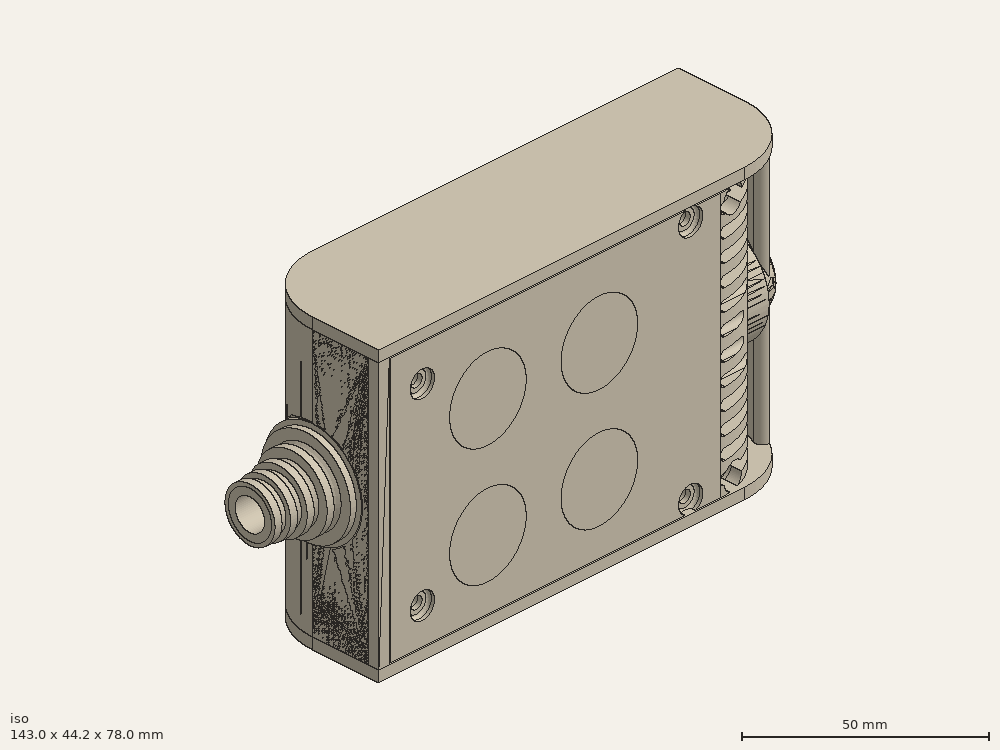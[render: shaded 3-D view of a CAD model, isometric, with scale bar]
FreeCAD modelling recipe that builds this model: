
FCSTD DOCUMENT  (FreeCAD 0.19R0.19.2)
Label: enclosure_135
License: All rights reserved
LicenseURL: http://en.wikipedia.org/wiki/All_rights_reserved
objects: Part::Feature×90, Part::Revolution×90, Part::MultiFuse×66, Sketcher::SketchObject×48, Part::Extrusion×36, Part::Cut×31, Part::Fillet×27, Part::Cylinder×24, Part::Box×17, App::MeasureDistance×4
note: 429 computed .brp shape members not serialized (recipe doc carries the construction recipe); baked Part::Feature solids carry a one-line shape summary decoded from their .brp

FEATURE [Sketcher::SketchObject] Sketch  label="topSketch"
  FullyConstrained = true
  sketch-geometry (20):
    g0: LineSegment StartX=5.21097e-06 StartY=3 StartZ=0 EndX=5.21097e-06 EndY=19 EndZ=0
    g1: ArcOfCircle CenterX=19 CenterY=19 CenterZ=0 NormalX=0 NormalY=0 NormalZ=1 AngleXU=0 Radius=19 StartAngle=1.5708 EndAngle=3.14159
    g2: ArcOfCircle CenterX=19 CenterY=19 CenterZ=0 NormalX=0 NormalY=0 NormalZ=1 AngleXU=0 Radius=16 StartAngle=1.5708 EndAngle=3.14159
    g3: LineSegment StartX=114 StartY=35 StartZ=0 EndX=19 EndY=35 EndZ=0
    g4: LineSegment StartX=5.21097e-06 StartY=3 StartZ=0 EndX=5.21097e-06 EndY=0 EndZ=0
    g5: LineSegment StartX=3 StartY=0 StartZ=0 EndX=5.21097e-06 EndY=0 EndZ=0
    g6: LineSegment StartX=3 StartY=19 StartZ=0 EndX=3 EndY=0 EndZ=0
    g7: LineSegment StartX=19 StartY=38 StartZ=0 EndX=124 EndY=38 EndZ=0
    g8: Circle CenterX=119 CenterY=35 CenterZ=0 NormalX=0 NormalY=0 NormalZ=1 AngleXU=0 Radius=1
    g9: Circle CenterX=121 CenterY=35 CenterZ=0 NormalX=0 NormalY=0 NormalZ=1 AngleXU=0 Radius=1
    g10: Circle CenterX=121 CenterY=33 CenterZ=0 NormalX=0 NormalY=0 NormalZ=1 AngleXU=0 Radius=1
    g11: BSplineCurve PolesCount=3 KnotsCount=2 Degree=2 IsPeriodic=0
    g12: GeomPoint X=119 Y=35 Z=0
    g13: GeomPoint X=121 Y=33 Z=0
    g14: LineSegment StartX=119 StartY=35 StartZ=0 EndX=114 EndY=35 EndZ=0
    g15: ArcOfCircle CenterX=105 CenterY=19 CenterZ=0 NormalX=0 NormalY=0 NormalZ=1 AngleXU=0 Radius=19 StartAngle=5.7297 EndAngle=6.28319
    g16: ArcOfCircle CenterX=105 CenterY=19 CenterZ=0 NormalX=0 NormalY=0 NormalZ=1 AngleXU=0 Radius=16 StartAngle=5.60905 EndAngle=6.28319
    g17: LineSegment StartX=121 StartY=33 StartZ=0 EndX=121 EndY=19 EndZ=0
    g18: LineSegment StartX=124 StartY=38 StartZ=0 EndX=124 EndY=19 EndZ=0
    g19: LineSegment StartX=117.5 StartY=9.01251 StartZ=0 EndX=121.163 EndY=9.0125 EndZ=0
  constraints (46):
    c: Vertical(g0)
    c: Block(g0)
    c: Coincident(g1,g0)
    c: Block(g1)
    c: Coincident(g2,g1)
    c: Block(g2)
    c: Coincident(g3,g2)
    c: Horizontal(g3)
    c: Tangent(g3,g2)
    c: Coincident(g4,g0)
    c: Distance(g4) = 3
    c: Vertical(g4)
    c: Coincident(g5,g4)
    c: Horizontal(g5)
    c: Coincident(g6,g2)
    c: Coincident(g6,g5)
    c: Vertical(g6)
    c: Horizontal(g7)
    c: Distance(g7) = 105
    c: Coincident(g7,g1)
    c: Block(g3)
    c: Weight(g8) = 1
    c: Equal(g8,g9)
    c: Equal(g8,g10)
    c: InternalAlignment(g8,g11)
    c: InternalAlignment(g9,g11)
    c: InternalAlignment(g10,g11)
    c: InternalAlignment(g12,g11)
    c: InternalAlignment(g13,g11)
    c: Block(g11)
    c: Coincident(g14,g11)
    c: Coincident(g14,g3)
    c: Horizontal(g14)
    c: Block(g15)
    c: Coincident(g16,g15)
    c: Block(g16)
    c: Coincident(g17,g11)
    c: Coincident(g17,g16)
    c: Vertical(g17)
    c: Distance(g17) = 14
    c: Coincident(g18,g7)
    c: Coincident(g18,g15)
    c: Vertical(g18)
    c: Distance(g18) = 19
    c: Coincident(g19,g16)
    c: Coincident(g19,g15)
FEATURE [Sketcher::SketchObject] Sketch001  label="bottomSketch"
  FullyConstrained = true
  sketch-geometry (32):
    g0: LineSegment StartX=3.3 StartY=-6.03275e-07 StartZ=0 EndX=98 EndY=-6.03275e-07 EndZ=0
    g1: ArcOfCircle CenterX=98 CenterY=19 CenterZ=0 NormalX=0 NormalY=0 NormalZ=1 AngleXU=0 Radius=19 StartAngle=4.71239 EndAngle=5.71103
    g2: LineSegment StartX=6.3 StartY=8 StartZ=0 EndX=3.3 EndY=8 EndZ=0
    g3: LineSegment StartX=3.3 StartY=8 StartZ=0 EndX=3.3 EndY=-6.03275e-07 EndZ=0
    g4: ArcOfCircle CenterX=8.3 CenterY=5 CenterZ=0 NormalX=0 NormalY=0 NormalZ=1 AngleXU=0 Radius=2 StartAngle=3.14159 EndAngle=4.71239
    g5: LineSegment StartX=6.3 StartY=8 StartZ=0 EndX=6.3 EndY=5 EndZ=0
    g6: ArcOfCircle CenterX=98 CenterY=19 CenterZ=0 NormalX=0 NormalY=0 NormalZ=1 AngleXU=0 Radius=12.7 StartAngle=4.71239 EndAngle=6.28319
    g7: LineSegment StartX=94.7 StartY=3 StartZ=0 EndX=8.3 EndY=3 EndZ=0
    g8-g12: Circle x5 (B-spline internal-alignment scaffolding for g13; pole/knot coordinates omitted)
    g13: BSplineCurve PolesCount=5 KnotsCount=3 Degree=3 IsPeriodic=0
    g14: GeomPoint X=98 Y=6.3 Z=0
    g15: GeomPoint X=96.3938 Y=4.71946 Z=0
    g16: GeomPoint X=94.7 Y=3 Z=0
    g17-g23: Circle x7 (B-spline internal-alignment scaffolding for g24; pole/knot coordinates omitted)
    g24: BSplineCurve PolesCount=7 KnotsCount=5 Degree=3 IsPeriodic=0
    g25-g29: GeomPoint x5 (B-spline internal-alignment scaffolding for g24; pole/knot coordinates omitted)
    g30: ArcOfCircle CenterX=98 CenterY=19 CenterZ=0 NormalX=0 NormalY=0 NormalZ=1 AngleXU=0 Radius=15.7 StartAngle=5.81226 EndAngle=6.28319
    g31: LineSegment StartX=110.7 StartY=19 StartZ=0 EndX=113.7 EndY=19 EndZ=0
  constraints (41):
    c: Horizontal(g0)
    c: Coincident(g1,g0)
    c: Block(g1)
    c: Horizontal(g2)
    c: Distance(g2) = 3
    c: Coincident(g3,g2)
    c: Vertical(g3)
    c: Coincident(g3,g0)
    c: Block(g4)
    c: Block(g2)
    c: Coincident(g5,g2)
    c: Coincident(g5,g4)
    c: Vertical(g5)
    c: Coincident(g6,g1)
    c: Block(g6)
    c: Coincident(g7,g4)
    c: Horizontal(g7)
    c: Block(g0)
    c: Block(g7)
    c: Block(g3)
    c: Coincident(g13,g6)
    c: Weight(g8) = 1
    c: Equal(g8, g9-g12) x4
    c: Coincident(g13,g7)
    c: InternalAlignment(g8-g12 -> g13) x5
    c: InternalAlignment(g14,g13)
    c: InternalAlignment(g15,g13)
    c: InternalAlignment(g16,g13)
    c: Block(g13)
    c: Weight(g17) = 1
    c: Equal(g17, g18-g23) x6
    c: Coincident(g24,g1)
    c: InternalAlignment(g17-g23 -> g24) x7
    c: InternalAlignment(g25-g29 -> g24) x5
    c: Block(g24)
    c: Coincident(g30,g24)
    c: Coincident(g31,g6)
    c: Coincident(g31,g30)
    c: Horizontal(g31)
    c: Block(g31)
    c: Block(g30)
FEATURE [Part::Extrusion] Extrude  label="top"
  Base = -> Sketch
  Dir = (0,0,1)
  DirMode = 2
  FaceMakerClass = Part::FaceMakerBullseye
  LengthFwd = 72
  LengthRev = 0
  Solid = true
  Symmetric = false
FEATURE [Part::Extrusion] Extrude001  label="bottom"
  Base = -> Sketch001
  Dir = (0,0,1)
  DirMode = 2
  FaceMakerClass = Part::FaceMakerBullseye
  LengthFwd = 71.4
  LengthRev = 0
  Placement = pos=(0,0,0.3) rot=(0,0,1;0rad)
  Solid = true
  Symmetric = false
FEATURE [Sketcher::SketchObject] Sketch002  label="topSketch001"
  FullyConstrained = true
  sketch-geometry (6):
    g0: ArcOfCircle CenterX=19 CenterY=19 CenterZ=0 NormalX=0 NormalY=0 NormalZ=1 AngleXU=0 Radius=19 StartAngle=1.5708 EndAngle=3.14159
    g1: LineSegment StartX=5.22862e-06 StartY=19 StartZ=0 EndX=5.22862e-06 EndY=1.19904e-11 EndZ=0
    g2: LineSegment StartX=19 StartY=38 StartZ=0 EndX=124 EndY=38 EndZ=0
    g3: LineSegment StartX=5.22862e-06 StartY=1.19904e-11 StartZ=0 EndX=105 EndY=1.19904e-11 EndZ=0
    g4: ArcOfCircle CenterX=105 CenterY=19 CenterZ=0 NormalX=0 NormalY=0 NormalZ=1 AngleXU=0 Radius=19 StartAngle=4.71239 EndAngle=6.28319
    g5: LineSegment StartX=124 StartY=38 StartZ=0 EndX=124 EndY=19 EndZ=0
  constraints (16):
    c: Block(g0)
    c: Coincident(g1,g0)
    c: Vertical(g1)
    c: Horizontal(g2)
    c: Distance(g2) = 105
    c: Coincident(g2,g0)
    c: Distance(g1) = 19
    c: Coincident(g3,g1)
    c: Horizontal(g3)
    c: Distance(g3) = 105
    c: Block(g4)
    c: Coincident(g4,g3)
    c: Coincident(g5,g2)
    c: Coincident(g5,g4)
    c: Vertical(g5)
    c: Distance(g5) = 19
FEATURE [Part::Extrusion] Extrude002  label="sideA"
  Base = -> Sketch002
  Dir = (0,0,1)
  DirMode = 2
  FaceMakerClass = Part::FaceMakerBullseye
  LengthFwd = 3
  LengthRev = 0
  Placement = pos=(0,0,-3) rot=(0,0,1;0rad)
  Solid = true
  Symmetric = false
FEATURE [Sketcher::SketchObject] Sketch003  label="topSketch002"
  FullyConstrained = true
  sketch-geometry (6):
    g0: LineSegment StartX=19 StartY=38 StartZ=0 EndX=117 EndY=38 EndZ=0
    g1: ArcOfCircle CenterX=19 CenterY=19 CenterZ=0 NormalX=0 NormalY=0 NormalZ=1 AngleXU=0 Radius=19 StartAngle=1.5708 EndAngle=3.14159
    g2: LineSegment StartX=117 StartY=38 StartZ=0 EndX=117 EndY=19 EndZ=0
    g3: LineSegment StartX=98 StartY=1.0161e-12 StartZ=0 EndX=5.22862e-06 EndY=1.0161e-12 EndZ=0
    g4: LineSegment StartX=5.22862e-06 StartY=19 StartZ=0 EndX=5.22862e-06 EndY=1.0161e-12 EndZ=0
    g5: ArcOfCircle CenterX=98 CenterY=19 CenterZ=0 NormalX=0 NormalY=0 NormalZ=1 AngleXU=0 Radius=19 StartAngle=4.71239 EndAngle=6.28319
  constraints (16):
    c: Horizontal(g0)
    c: Distance(g0) = 98
    c: Coincident(g1,g0)
    c: Block(g1)
    c: Coincident(g2,g0)
    c: Vertical(g2)
    c: Distance(g2) = 19
    c: Horizontal(g3)
    c: Coincident(g4,g1)
    c: Vertical(g4)
    c: Coincident(g3,g4)
    c: Block(g3)
    c: Coincident(g5,g2)
    c: Coincident(g5,g3)
    c: Block(g0)
    c: Block(g5)
FEATURE [Sketcher::SketchObject] Sketch004
  FullyConstrained = true
  MapMode = 3
  Placement = pos=(0,0,0) rot=(1,0,0;1.5708rad)
  Support = -> [Extrude]
  sketch-geometry (8):
    g0: Circle CenterX=80.351 CenterY=-67.6202 CenterZ=0 NormalX=0 NormalY=0 NormalZ=1 AngleXU=0 Radius=2
    g1: Circle CenterX=80.351 CenterY=-67.6202 CenterZ=0 NormalX=0 NormalY=0 NormalZ=1 AngleXU=0 Radius=3
    g2: Circle CenterX=80.351 CenterY=-4.92017 CenterZ=0 NormalX=0 NormalY=0 NormalZ=1 AngleXU=0 Radius=2
    g3: Circle CenterX=80.351 CenterY=-4.92017 CenterZ=0 NormalX=0 NormalY=0 NormalZ=1 AngleXU=0 Radius=3
    g4: Circle CenterX=23.851 CenterY=-4.92017 CenterZ=0 NormalX=0 NormalY=0 NormalZ=1 AngleXU=0 Radius=2
    g5: Circle CenterX=23.851 CenterY=-4.92017 CenterZ=0 NormalX=0 NormalY=0 NormalZ=1 AngleXU=0 Radius=3
    g6: Circle CenterX=23.851 CenterY=-67.6202 CenterZ=0 NormalX=0 NormalY=0 NormalZ=1 AngleXU=0 Radius=2
    g7: Circle CenterX=23.851 CenterY=-67.6202 CenterZ=0 NormalX=0 NormalY=0 NormalZ=1 AngleXU=0 Radius=3
  constraints (8):
    c: Block(g3)
    c: Block(g2)
    c: Block(g1)
    c: Block(g0)
    c: Block(g6)
    c: Block(g7)
    c: Block(g4)
    c: Block(g5)
FEATURE [Part::Extrusion] Extrude004
  Base = -> Sketch004
  Dir = (0,-1,2e-16)
  DirMode = 2
  FaceMakerClass = Part::FaceMakerBullseye
  LengthFwd = 6
  LengthRev = 0
  Placement = pos=(0,9,0) rot=(0,0,1;0rad)
  Solid = true
  Symmetric = false
FEATURE [Sketcher::SketchObject] Sketch005
  FullyConstrained = true
  MapMode = 3
  Placement = pos=(0,0,0) rot=(1,0,0;1.5708rad)
  Support = -> [Extrude]
  sketch-geometry (8):
    g0: Circle CenterX=80.351 CenterY=-67.6202 CenterZ=0 NormalX=0 NormalY=0 NormalZ=1 AngleXU=0 Radius=3
    g1: Circle CenterX=80.351 CenterY=-4.92017 CenterZ=0 NormalX=0 NormalY=0 NormalZ=1 AngleXU=0 Radius=3
    g2: Circle CenterX=23.851 CenterY=-4.92017 CenterZ=0 NormalX=0 NormalY=0 NormalZ=1 AngleXU=0 Radius=3
    g3: Circle CenterX=23.851 CenterY=-67.6202 CenterZ=0 NormalX=0 NormalY=0 NormalZ=1 AngleXU=0 Radius=3
    g4: Circle CenterX=23.851 CenterY=-67.6202 CenterZ=0 NormalX=0 NormalY=0 NormalZ=1 AngleXU=0 Radius=5
    g5: Circle CenterX=80.351 CenterY=-67.6202 CenterZ=0 NormalX=0 NormalY=0 NormalZ=1 AngleXU=0 Radius=5
    g6: Circle CenterX=23.851 CenterY=-4.92017 CenterZ=0 NormalX=0 NormalY=0 NormalZ=1 AngleXU=0 Radius=5
    g7: Circle CenterX=80.351 CenterY=-4.92017 CenterZ=0 NormalX=0 NormalY=0 NormalZ=1 AngleXU=0 Radius=5
  constraints (8):
    c: Block(g1)
    c: Block(g0)
    c: Block(g3)
    c: Block(g2)
    c: Block(g5)
    c: Block(g4)
    c: Block(g6)
    c: Block(g7)
FEATURE [Part::Extrusion] Extrude005
  Base = -> Sketch005
  Dir = (0,-1,2e-16)
  DirMode = 2
  FaceMakerClass = Part::FaceMakerBullseye
  LengthFwd = 2
  LengthRev = 0
  Solid = true
  Symmetric = false
FEATURE [Sketcher::SketchObject] Sketch006
  FullyConstrained = true
  MapMode = 3
  Placement = pos=(0,0,0) rot=(1,0,0;1.5708rad)
  sketch-geometry (8):
    g0: Circle CenterX=80.351 CenterY=-67.6202 CenterZ=0 NormalX=0 NormalY=0 NormalZ=1 AngleXU=0 Radius=3
    g1: Circle CenterX=80.351 CenterY=-4.92017 CenterZ=0 NormalX=0 NormalY=0 NormalZ=1 AngleXU=0 Radius=3
    g2: Circle CenterX=23.851 CenterY=-4.92017 CenterZ=0 NormalX=0 NormalY=0 NormalZ=1 AngleXU=0 Radius=3
    g3: Circle CenterX=23.851 CenterY=-67.6202 CenterZ=0 NormalX=0 NormalY=0 NormalZ=1 AngleXU=0 Radius=3
    g4: Circle CenterX=23.851 CenterY=-67.6202 CenterZ=0 NormalX=0 NormalY=0 NormalZ=1 AngleXU=0 Radius=5
    g5: Circle CenterX=80.351 CenterY=-67.6202 CenterZ=0 NormalX=0 NormalY=0 NormalZ=1 AngleXU=0 Radius=5
    g6: Circle CenterX=23.851 CenterY=-4.92017 CenterZ=0 NormalX=0 NormalY=0 NormalZ=1 AngleXU=0 Radius=5
    g7: Circle CenterX=80.351 CenterY=-4.92017 CenterZ=0 NormalX=0 NormalY=0 NormalZ=1 AngleXU=0 Radius=5
  constraints (8):
    c: Block(g1)
    c: Block(g0)
    c: Block(g3)
    c: Block(g2)
    c: Block(g5)
    c: Block(g4)
    c: Block(g6)
    c: Block(g7)
FEATURE [Part::Extrusion] Extrude007
  Base = -> Sketch006
  Dir = (0,-1,2e-16)
  DirMode = 2
  FaceMakerClass = Part::FaceMakerBullseye
  LengthFwd = 2
  LengthRev = 0
  Solid = true
  Symmetric = false
FEATURE [Part::Fillet] Fillet
  Base = -> Extrude007
  Edges = 4 edges r=1.99: [Edge6,Edge12,Edge18,Edge24]
FEATURE [Part::Cut] Cut
  Base = -> Extrude005
  Placement = pos=(0,5,0) rot=(0,0,1;0rad)
  Tool = -> Fillet
FEATURE [Part::MultiFuse] Fusion  label="pCBScrews"
  Placement = pos=(-2.5,0,72.3) rot=(0,0,1;0rad)
  Shapes = -> [Extrude004,Cut]
FEATURE [App::MeasureDistance] Distance  label="Distance: 0.69 mm"
  Distance = 0.685967
  P1 = (24.0138,2.9647,0.3)
  P2 = (23.8901,3,-0.373787)
FEATURE [App::MeasureDistance] Distance001  label="Distance: 0.53 mm"
  Distance = 0.533607
  P1 = (80.2939,3,72.2334)
  P2 = (80.281,2.99661,71.7)
FEATURE [Part::Fillet] Fillet001
  Base = -> Extrude001
  Edges = 1 edges r=2.4: [Edge17]
FEATURE [Part::Fillet] Fillet002  label="bottom001"
  Base = -> Fillet001
  Edges = 1 edges r=2.4: [Edge36]
FEATURE [Part::Fillet] Fillet003  label="top001"
  Base = -> Extrude
  Edges = 1 edges r=2: [Edge1]
FEATURE [Sketcher::SketchObject] Sketch007
  FullyConstrained = true
  sketch-geometry (16):
    g0: LineSegment StartX=4 StartY=0 StartZ=0 EndX=4 EndY=2.4 EndZ=0
    g1: LineSegment StartX=4 StartY=2.4 StartZ=0 EndX=7 EndY=2.4 EndZ=0
    g2: LineSegment StartX=4 StartY=0 StartZ=0 EndX=5.7 EndY=0 EndZ=0
    g3: LineSegment StartX=5.7 StartY=0 StartZ=0 EndX=5.7 EndY=-5.6 EndZ=0
    g4-g8: Circle x5 (B-spline internal-alignment scaffolding for g9; pole/knot coordinates omitted)
    g9: BSplineCurve PolesCount=5 KnotsCount=3 Degree=3 IsPeriodic=0
    g10: GeomPoint X=7 Y=2.4 Z=0
    g11: GeomPoint X=10.4582 Y=-1.55472 Z=0
    g12: GeomPoint X=14 Y=-5.6 Z=0
    g13: LineSegment StartX=14 StartY=-5.6 StartZ=0 EndX=14 EndY=-14.1 EndZ=0
    g14: LineSegment StartX=14 StartY=-14.1 StartZ=0 EndX=6.5 EndY=-14.1 EndZ=0
    g15: LineSegment StartX=5.7 StartY=-5.6 StartZ=0 EndX=6.5 EndY=-14.1 EndZ=0
  constraints (28):
    c: Distance(g0) = 2.4
    c: Vertical(g0)
    c: Block(g0)
    c: Coincident(g1,g0)
    c: Horizontal(g1)
    c: Distance(g1) = 3
    c: Coincident(g2,g0)
    c: Horizontal(g2)
    c: Distance(g2) = 1.7
    c: Coincident(g3,g2)
    c: Vertical(g3)
    c: Distance(g3) = 5.6
    c: Coincident(g9,g1)
    c: Weight(g4) = 1
    c: Equal(g4, g5-g8) x4
    c: InternalAlignment(g4-g8 -> g9) x5
    c: InternalAlignment(g10,g9)
    c: InternalAlignment(g11,g9)
    c: InternalAlignment(g12,g9)
    c: Block(g9)
    c: Coincident(g13,g9)
    c: Vertical(g13)
    c: Distance(g13) = 8.5
    c: Coincident(g14,g13)
    c: Horizontal(g14)
    c: Distance(g14) = 7.5
    c: Coincident(g15,g3)
    c: Coincident(g15,g14)
FEATURE [Part::Feature] Face
  shape: bbox 10 x 16.5 x 2e-07 mm, 1 faces, 0 solids (baked)
FEATURE [Part::Revolution] Revolve  label="plugHousing"
  Angle = 360
  Axis = (0,1,0)
  Base = (0,0,0)
  FaceMakerClass = Part::FaceMakerBullseye
  Placement = pos=(0,0,36.15) rot=(0,0,1;0rad)
  Solid = false
  Source = -> Face
  Symmetric = false
FEATURE [Part::Feature] Face001
  shape: bbox 10 x 16.5 x 2e-07 mm, 1 faces, 0 solids (baked)
FEATURE [Part::Revolution] Revolve001  label="plugHousing001"
  Angle = 360
  Axis = (0,1,0)
  Base = (0,0,0)
  FaceMakerClass = Part::FaceMakerBullseye
  Placement = pos=(0,0,36.15) rot=(0,0,1;0rad)
  Solid = false
  Source = -> Face001
  Symmetric = false
FEATURE [Part::MultiFuse] Fusion001  label="plugHousing002"
  Placement = pos=(0,0,0) rot=(0,0,1;1.5708rad)
  Shapes = -> [Revolve001,Revolve]
FEATURE [Part::Feature] Face002
  shape: bbox 10 x 16.5 x 2e-07 mm, 1 faces, 0 solids (baked)
FEATURE [Part::Revolution] Revolve003  label="plugHousing005"
  Angle = 360
  Axis = (0,1,0)
  Base = (0,0,0)
  FaceMakerClass = Part::FaceMakerBullseye
  Placement = pos=(0,0,36.15) rot=(0,0,1;0rad)
  Solid = false
  Source = -> Face002
  Symmetric = false
FEATURE [Part::Feature] Face003
  shape: bbox 10 x 16.5 x 2e-07 mm, 1 faces, 0 solids (baked)
FEATURE [Part::Revolution] Revolve002  label="plugHousing003"
  Angle = 360
  Axis = (0,1,0)
  Base = (0,0,0)
  FaceMakerClass = Part::FaceMakerBullseye
  Placement = pos=(0,0,36.15) rot=(0,0,1;0rad)
  Solid = false
  Source = -> Face003
  Symmetric = false
FEATURE [Part::MultiFuse] Fusion002  label="plugHousing004"
  Placement = pos=(0,0,0) rot=(0,0,1;1.5708rad)
  Shapes = -> [Revolve002,Revolve003]
FEATURE [Part::MultiFuse] Fusion003  label="plugHousing006"
  Placement = pos=(0,19,0) rot=(0,0,1;3.14159rad)
  Shapes = -> [Fusion002,Fusion001]
FEATURE [Part::Feature] Face004
  shape: bbox 10 x 16.5 x 2e-07 mm, 1 faces, 0 solids (baked)
FEATURE [Part::Revolution] Revolve006  label="plugHousing010"
  Angle = 360
  Axis = (0,1,0)
  Base = (0,0,0)
  FaceMakerClass = Part::FaceMakerBullseye
  Placement = pos=(0,0,36.15) rot=(0,0,1;0rad)
  Solid = false
  Source = -> Face004
  Symmetric = false
FEATURE [Part::Feature] Face005
  shape: bbox 10 x 16.5 x 2e-07 mm, 1 faces, 0 solids (baked)
FEATURE [Part::Revolution] Revolve007  label="plugHousing011"
  Angle = 360
  Axis = (0,1,0)
  Base = (0,0,0)
  FaceMakerClass = Part::FaceMakerBullseye
  Placement = pos=(0,0,36.15) rot=(0,0,1;0rad)
  Solid = false
  Source = -> Face005
  Symmetric = false
FEATURE [Part::Feature] Face006
  shape: bbox 10 x 16.5 x 2e-07 mm, 1 faces, 0 solids (baked)
FEATURE [Part::Revolution] Revolve004  label="plugHousing007"
  Angle = 360
  Axis = (0,1,0)
  Base = (0,0,0)
  FaceMakerClass = Part::FaceMakerBullseye
  Placement = pos=(0,0,36.15) rot=(0,0,1;0rad)
  Solid = false
  Source = -> Face006
  Symmetric = false
FEATURE [Part::MultiFuse] Fusion004  label="plugHousing009"
  Placement = pos=(0,0,0) rot=(0,0,1;1.5708rad)
  Shapes = -> [Revolve004,Revolve007]
FEATURE [Part::Feature] Face007
  shape: bbox 10 x 16.5 x 2e-07 mm, 1 faces, 0 solids (baked)
FEATURE [Part::Revolution] Revolve005  label="plugHousing008"
  Angle = 360
  Axis = (0,1,0)
  Base = (0,0,0)
  FaceMakerClass = Part::FaceMakerBullseye
  Placement = pos=(0,0,36.15) rot=(0,0,1;0rad)
  Solid = false
  Source = -> Face007
  Symmetric = false
FEATURE [Part::MultiFuse] Fusion005  label="plugHousing012"
  Placement = pos=(0,0,0) rot=(0,0,1;1.5708rad)
  Shapes = -> [Revolve006,Revolve005]
FEATURE [Part::MultiFuse] Fusion006  label="plugHousing013"
  Placement = pos=(0,19,0) rot=(0,0,1;3.14159rad)
  Shapes = -> [Fusion005,Fusion004]
FEATURE [Part::MultiFuse] Fusion007  label="plugHousing014"
  Placement = pos=(122.621,0,-0.15) rot=(0,0,1;0rad)
  Shapes = -> [Fusion003,Fusion006]
FEATURE [Part::Cylinder] Cylinder002
  Angle = 360
  AttacherType = Attacher::AttachEngine3D
  Height = 20
  Placement = pos=(0,0,36.15) rot=(0,0,1;0rad)
  Radius = 4
FEATURE [Part::Cylinder] Cylinder003
  Angle = 360
  AttacherType = Attacher::AttachEngine3D
  Height = 10
  Placement = pos=(0,0,36.15) rot=(0,0,1;0rad)
  Radius = 4
FEATURE [Part::MultiFuse] Fusion009  label="removeToCreateHoleForPlugHousing"
  Placement = pos=(70,19,36.15) rot=(0,1,0;1.5708rad)
  Shapes = -> [Cylinder002,Cylinder003]
FEATURE [Part::Cylinder] Cylinder004
  Angle = 360
  AttacherType = Attacher::AttachEngine3D
  Height = 20
  Placement = pos=(0,0,36.15) rot=(0,0,1;0rad)
  Radius = 4
FEATURE [Part::Cylinder] Cylinder005
  Angle = 360
  AttacherType = Attacher::AttachEngine3D
  Height = 10
  Placement = pos=(0,0,36.15) rot=(0,0,1;0rad)
  Radius = 4
FEATURE [Part::MultiFuse] Fusion010  label="removeToCreateHoleForPlugHousing001"
  Placement = pos=(70,19,36.15) rot=(0,1,0;1.5708rad)
  Shapes = -> [Cylinder004,Cylinder005]
FEATURE [Part::Cut] Cut001
  Base = -> Fillet003
  Tool = -> Fusion010
FEATURE [Part::Cut] Cut002  label="Bottom"
  Base = -> Fillet002
  Tool = -> Fusion009
FEATURE [Part::Feature] Face008
  shape: bbox 10 x 16.5 x 2e-07 mm, 1 faces, 0 solids (baked)
FEATURE [Part::Revolution] Revolve011  label="plugHousing021"
  Angle = 360
  Axis = (0,1,0)
  Base = (0,0,0)
  FaceMakerClass = Part::FaceMakerBullseye
  Placement = pos=(0,0,36.15) rot=(0,0,1;0rad)
  Solid = false
  Source = -> Face008
  Symmetric = false
FEATURE [Part::Feature] Face009
  shape: bbox 10 x 16.5 x 2e-07 mm, 1 faces, 0 solids (baked)
FEATURE [Part::Revolution] Revolve012  label="plugHousing022"
  Angle = 360
  Axis = (0,1,0)
  Base = (0,0,0)
  FaceMakerClass = Part::FaceMakerBullseye
  Placement = pos=(0,0,36.15) rot=(0,0,1;0rad)
  Solid = false
  Source = -> Face009
  Symmetric = false
FEATURE [Part::Feature] Face010 .. Face013  x4 (patterned run collapsed; names and placements below)
  shape: bbox 10 x 16.5 x 2e-07 mm, 1 faces, 0 solids (baked)
FEATURE [Part::Revolution] Revolve015  label="plugHousing027"
  Angle = 360
  Axis = (0,1,0)
  Base = (0,0,0)
  FaceMakerClass = Part::FaceMakerBullseye
  Placement = pos=(0,0,36.15) rot=(0,0,1;0rad)
  Solid = false
  Source = -> Face013
  Symmetric = false
FEATURE [Part::Feature] Face014
  shape: bbox 10 x 16.5 x 2e-07 mm, 1 faces, 0 solids (baked)
FEATURE [Part::Feature] Face015
  shape: bbox 10 x 16.5 x 2e-07 mm, 1 faces, 0 solids (baked)
FEATURE [Part::Feature] Face016
  shape: bbox 10 x 16.5 x 2e-07 mm, 1 faces, 0 solids (baked)
FEATURE [Part::Revolution] Revolve019  label="plugHousing033"
  Angle = 360
  Axis = (0,1,0)
  Base = (0,0,0)
  FaceMakerClass = Part::FaceMakerBullseye
  Placement = pos=(0,0,36.15) rot=(0,0,1;0rad)
  Solid = false
  Source = -> Face016
  Symmetric = false
FEATURE [Part::Feature] Face017
  shape: bbox 10 x 16.5 x 2e-07 mm, 1 faces, 0 solids (baked)
FEATURE [Part::Revolution] Revolve020  label="plugHousing034"
  Angle = 360
  Axis = (0,1,0)
  Base = (0,0,0)
  FaceMakerClass = Part::FaceMakerBullseye
  Placement = pos=(0,0,36.15) rot=(0,0,1;0rad)
  Solid = false
  Source = -> Face017
  Symmetric = false
FEATURE [Part::Feature] Face018
  shape: bbox 10 x 16.5 x 2e-07 mm, 1 faces, 0 solids (baked)
FEATURE [Part::Revolution] Revolve016  label="plugHousing030"
  Angle = 360
  Axis = (0,1,0)
  Base = (0,0,0)
  FaceMakerClass = Part::FaceMakerBullseye
  Placement = pos=(0,0,36.15) rot=(0,0,1;0rad)
  Solid = false
  Source = -> Face018
  Symmetric = false
FEATURE [Part::MultiFuse] Fusion020  label="plugHousing038"
  Placement = pos=(0,0,0) rot=(0,0,1;1.5708rad)
  Shapes = -> [Revolve016,Revolve020]
FEATURE [Part::Feature] Face019
  shape: bbox 10 x 16.5 x 2e-07 mm, 1 faces, 0 solids (baked)
FEATURE [Part::Feature] Face020
  shape: bbox 10 x 16.5 x 2e-07 mm, 1 faces, 0 solids (baked)
FEATURE [Part::Revolution] Revolve017  label="plugHousing031"
  Angle = 360
  Axis = (0,1,0)
  Base = (0,0,0)
  FaceMakerClass = Part::FaceMakerBullseye
  Placement = pos=(0,0,36.15) rot=(0,0,1;0rad)
  Solid = false
  Source = -> Face020
  Symmetric = false
FEATURE [Part::MultiFuse] Fusion021  label="plugHousing039"
  Placement = pos=(0,0,0) rot=(0,0,1;1.5708rad)
  Shapes = -> [Revolve019,Revolve017]
FEATURE [Part::MultiFuse] Fusion023  label="plugHousing041"
  Placement = pos=(0,19,0) rot=(0,0,1;3.14159rad)
  Shapes = -> [Fusion021,Fusion020]
FEATURE [Part::Revolution] Revolve022  label="plugHousing043"
  Angle = 360
  Axis = (0,1,0)
  Base = (0,0,0)
  FaceMakerClass = Part::FaceMakerBullseye
  Placement = pos=(0,0,36.15) rot=(0,0,1;0rad)
  Solid = false
  Source = -> Face019
  Symmetric = false
FEATURE [Part::Feature] Face021
  shape: bbox 10 x 16.5 x 2e-07 mm, 1 faces, 0 solids (baked)
FEATURE [Part::Revolution] Revolve023  label="plugHousing044"
  Angle = 360
  Axis = (0,1,0)
  Base = (0,0,0)
  FaceMakerClass = Part::FaceMakerBullseye
  Placement = pos=(0,0,36.15) rot=(0,0,1;0rad)
  Solid = false
  Source = -> Face021
  Symmetric = false
FEATURE [Part::Feature] Face022
  shape: bbox 10 x 16.5 x 2e-07 mm, 1 faces, 0 solids (baked)
FEATURE [Part::Revolution] Revolve018  label="plugHousing032"
  Angle = 360
  Axis = (0,1,0)
  Base = (0,0,0)
  FaceMakerClass = Part::FaceMakerBullseye
  Placement = pos=(0,0,36.15) rot=(0,0,1;0rad)
  Solid = false
  Source = -> Face022
  Symmetric = false
FEATURE [Part::MultiFuse] Fusion022  label="plugHousing040"
  Placement = pos=(0,0,0) rot=(0,0,1;1.5708rad)
  Shapes = -> [Revolve018,Revolve023]
FEATURE [Part::Feature] Face023
  shape: bbox 10 x 16.5 x 2e-07 mm, 1 faces, 0 solids (baked)
FEATURE [Part::Revolution] Revolve021  label="plugHousing035"
  Angle = 360
  Axis = (0,1,0)
  Base = (0,0,0)
  FaceMakerClass = Part::FaceMakerBullseye
  Placement = pos=(0,0,36.15) rot=(0,0,1;0rad)
  Solid = false
  Source = -> Face023
  Symmetric = false
FEATURE [Part::MultiFuse] Fusion018  label="plugHousing036"
  Placement = pos=(0,0,0) rot=(0,0,1;1.5708rad)
  Shapes = -> [Revolve022,Revolve021]
FEATURE [Part::MultiFuse] Fusion019  label="plugHousing037"
  Placement = pos=(0,19,0) rot=(0,0,1;3.14159rad)
  Shapes = -> [Fusion018,Fusion022]
FEATURE [Part::MultiFuse] Fusion024  label="plugHousing042"
  Placement = pos=(122.621,0,-0.15) rot=(0,0,1;0rad)
  Shapes = -> [Fusion023,Fusion019]
FEATURE [Part::Cylinder] Cylinder006
  Angle = 360
  AttacherType = Attacher::AttachEngine3D
  Height = 20
  Placement = pos=(0,0,36.15) rot=(0,0,1;0rad)
  Radius = 14.3
FEATURE [Part::Cylinder] Cylinder007
  Angle = 360
  AttacherType = Attacher::AttachEngine3D
  Height = 10
  Placement = pos=(0,0,36.15) rot=(0,0,1;0rad)
  Radius = 4
FEATURE [Part::MultiFuse] Fusion026  label="removeToCreteHoleForPlugHousing"
  Placement = pos=(70,19,36) rot=(0,1,0;1.5708rad)
  Shapes = -> [Cylinder006,Cylinder007]
FEATURE [Part::Box] Box001  label="Cube001"
  AttacherType = Attacher::AttachEngine3D
  Height = 28
  Length = 3
  Placement = pos=(110.7,19,22) rot=(0,0,1;0rad)
  Width = 15.7
FEATURE [Part::Cut] Cut003  label="top002"
  Base = -> Cut001
  Tool = -> Fusion007
FEATURE [Part::Revolution] Revolve008  label="plugHousing015"
  Angle = 360
  Axis = (0,1,0)
  Base = (0,0,0)
  FaceMakerClass = Part::FaceMakerBullseye
  Placement = pos=(0,0,36.15) rot=(0,0,1;0rad)
  Solid = false
  Source = -> Face010
  Symmetric = false
FEATURE [Part::MultiFuse] Fusion013  label="plugHousing020"
  Placement = pos=(0,0,0) rot=(0,0,1;1.5708rad)
  Shapes = -> [Revolve008,Revolve012]
FEATURE [Part::Cut] Cut004  label="top003"
  Base = -> Cut003
  Placement = pos=(1,0,0) rot=(0,0,1;0rad)
  Tool = -> Fusion026
FEATURE [Part::Cylinder] Cylinder008
  Angle = 360
  AttacherType = Attacher::AttachEngine3D
  Height = 20
  Placement = pos=(0,0,36.15) rot=(0,0,1;0rad)
  Radius = 10.3
FEATURE [Part::Cylinder] Cylinder009
  Angle = 360
  AttacherType = Attacher::AttachEngine3D
  Height = 10
  Placement = pos=(0,0,36.15) rot=(0,0,1;0rad)
  Radius = 4
FEATURE [Part::MultiFuse] Fusion027  label="removeToCreteHoleForPlugHousing001"
  Placement = pos=(70,19,36) rot=(0,1,0;1.5708rad)
  Shapes = -> [Cylinder008,Cylinder009]
FEATURE [Part::Cut] Cut005  label="plugHousingTab"
  Base = -> Box001
  Tool = -> Fusion027
FEATURE [Part::MultiFuse] Fusion028  label="plugHousing045"
  Shapes = -> [Fusion024,Cut005]
FEATURE [Part::Box] Box002  label="Cube002"
  AttacherType = Attacher::AttachEngine3D
  Height = 28.8
  Length = 3
  Placement = pos=(107.3,28,21.6) rot=(0,0,1;0rad)
  Width = 7
FEATURE [Part::Box] Box003  label="Cube003"
  AttacherType = Attacher::AttachEngine3D
  Height = 3
  Length = 6.4
  Placement = pos=(107.3,28,18.6) rot=(0,0,1;0rad)
  Width = 7
FEATURE [Part::Box] Box004  label="Cube004"
  AttacherType = Attacher::AttachEngine3D
  Height = 3
  Length = 6.4
  Placement = pos=(107.3,28,50.4) rot=(0,0,1;0rad)
  Width = 7
FEATURE [Part::MultiFuse] Fusion029  label="plugHousingBracketHolder"
  Shapes = -> [Box004,Box002,Box003]
FEATURE [Part::Cylinder] Cylinder010
  Angle = 360
  AttacherType = Attacher::AttachEngine3D
  Height = 20
  Placement = pos=(0,0,36.15) rot=(0,0,1;0rad)
  Radius = 14.3
FEATURE [Part::Cylinder] Cylinder011
  Angle = 360
  AttacherType = Attacher::AttachEngine3D
  Height = 10
  Placement = pos=(0,0,36.15) rot=(0,0,1;0rad)
  Radius = 4
FEATURE [Part::MultiFuse] Fusion030  label="removeToCreteHoleForPlugHousing002"
  Placement = pos=(70,19,36) rot=(0,1,0;1.5708rad)
  Shapes = -> [Cylinder010,Cylinder011]
FEATURE [Part::Cut] Cut006  label="plugHousingBracketHolder001"
  Base = -> Fusion029
  Tool = -> Fusion030
FEATURE [Part::Cylinder] Cylinder012
  Angle = 360
  AttacherType = Attacher::AttachEngine3D
  Height = 20
  Placement = pos=(0,0,36.15) rot=(0,0,1;0rad)
  Radius = 7
FEATURE [Part::Cylinder] Cylinder013
  Angle = 360
  AttacherType = Attacher::AttachEngine3D
  Height = 10
  Placement = pos=(0,0,36.15) rot=(0,0,1;0rad)
  Radius = 4
FEATURE [Part::MultiFuse] Fusion032  label="removeToCreteHoleForPlugHousing003"
  Placement = pos=(70,19,36) rot=(0,1,0;1.5708rad)
  Shapes = -> [Cylinder012,Cylinder013]
FEATURE [Part::Cut] Cut007  label="bottom002"
  Base = -> Cut002
  Tool = -> Fusion032
FEATURE [Sketcher::SketchObject] Sketch008
  FullyConstrained = true
  sketch-geometry (54):
    g0: LineSegment StartX=-4.2 StartY=0 StartZ=0 EndX=-6.2 EndY=0 EndZ=0
    g1: LineSegment StartX=-14 StartY=-18 StartZ=0 EndX=-14 EndY=-26.5 EndZ=0
    g2: LineSegment StartX=-4.2 StartY=0 StartZ=0 EndX=-4.2 EndY=-13.4877 EndZ=0
    g3: Circle CenterX=-4.2 CenterY=-13.4877 CenterZ=0 NormalX=0 NormalY=0 NormalZ=1 AngleXU=0 Radius=1
    g4: Circle CenterX=-4.2 CenterY=-26.5 CenterZ=0 NormalX=0 NormalY=0 NormalZ=1 AngleXU=0 Radius=1
    g5: Circle CenterX=-8.2 CenterY=-26.5 CenterZ=0 NormalX=0 NormalY=0 NormalZ=1 AngleXU=0 Radius=1
    g6: BSplineCurve PolesCount=3 KnotsCount=2 Degree=2 IsPeriodic=0
    g7: GeomPoint X=-4.2 Y=-13.4877 Z=0
    g8: GeomPoint X=-8.2 Y=-26.5 Z=0
    g9: LineSegment StartX=-14 StartY=-26.5 StartZ=0 EndX=-8.2 EndY=-26.5 EndZ=0
    g10: LineSegment StartX=-10.15 StartY=-12 StartZ=0 EndX=-10.15 EndY=-14 EndZ=0
    g11: LineSegment StartX=-12.8401 StartY=-16 StartZ=0 EndX=-10.1571 EndY=-16 EndZ=0
    g12: LineSegment StartX=-10.15 StartY=-14 StartZ=0 EndX=-8.70761 EndY=-14 EndZ=0
    g13: LineSegment StartX=-12.8401 StartY=-16 StartZ=0 EndX=-12.8401 EndY=-17.6958 EndZ=0
    g14: LineSegment StartX=-10.15 StartY=-12 StartZ=0 EndX=-7.79258 EndY=-12 EndZ=0
    g15: Circle CenterX=-6.2215 CenterY=-2 CenterZ=0 NormalX=0 NormalY=0 NormalZ=1 AngleXU=0 Radius=1
    g16: Circle CenterX=-6.22762 CenterY=-2.58724 CenterZ=0 NormalX=0 NormalY=0 NormalZ=1 AngleXU=0 Radius=1
    g17: Circle CenterX=-6.32538 CenterY=-4 CenterZ=0 NormalX=0 NormalY=0 NormalZ=1 AngleXU=0 Radius=1
    g18: BSplineCurve PolesCount=3 KnotsCount=2 Degree=2 IsPeriodic=0
    g19: GeomPoint X=-6.2215 Y=-2 Z=0
    g20: GeomPoint X=-6.32538 Y=-4 Z=0
    g21: Circle CenterX=-6.48644 CenterY=-5.99526 CenterZ=0 NormalX=0 NormalY=0 NormalZ=1 AngleXU=0 Radius=1
    g22: Circle CenterX=-6.58486 CenterY=-6.99526 CenterZ=0 NormalX=0 NormalY=0 NormalZ=1 AngleXU=0 Radius=1
    g23: Circle CenterX=-6.77343 CenterY=-8 CenterZ=0 NormalX=0 NormalY=0 NormalZ=1 AngleXU=0 Radius=1
    g24: BSplineCurve PolesCount=3 KnotsCount=2 Degree=2 IsPeriodic=0
    g25: GeomPoint X=-6.48644 Y=-5.99526 Z=0
    g26: GeomPoint X=-6.77343 Y=-8 Z=0
    g27: Circle CenterX=-7.19003 CenterY=-10 CenterZ=0 NormalX=0 NormalY=0 NormalZ=1 AngleXU=0 Radius=1
    g28: Circle CenterX=-7.44407 CenterY=-11.0915 CenterZ=0 NormalX=0 NormalY=0 NormalZ=1 AngleXU=0 Radius=1
    g29: Circle CenterX=-7.79258 CenterY=-12 CenterZ=0 NormalX=0 NormalY=0 NormalZ=1 AngleXU=0 Radius=1
    g30: BSplineCurve PolesCount=3 KnotsCount=2 Degree=2 IsPeriodic=0
    g31: GeomPoint X=-7.19003 Y=-10 Z=0
    g32: GeomPoint X=-7.79258 Y=-12 Z=0
    g33: Circle CenterX=-8.70761 CenterY=-14 CenterZ=0 NormalX=0 NormalY=0 NormalZ=1 AngleXU=0 Radius=1
    g34: Circle CenterX=-9.33087 CenterY=-15.1837 CenterZ=0 NormalX=0 NormalY=0 NormalZ=1 AngleXU=0 Radius=1
    g35: Circle CenterX=-10.1571 CenterY=-16 CenterZ=0 NormalX=0 NormalY=0 NormalZ=1 AngleXU=0 Radius=1
    g36: BSplineCurve PolesCount=3 KnotsCount=2 Degree=2 IsPeriodic=0
    g37: GeomPoint X=-8.70761 Y=-14 Z=0
    g38: GeomPoint X=-10.1571 Y=-16 Z=0
    g39: Circle CenterX=-12.8401 CenterY=-17.6958 CenterZ=0 NormalX=0 NormalY=0 NormalZ=1 AngleXU=0 Radius=1
    g40: Circle CenterX=-13.3521 CenterY=-17.9027 CenterZ=0 NormalX=0 NormalY=0 NormalZ=1 AngleXU=0 Radius=1
    g41: Circle CenterX=-14 CenterY=-18 CenterZ=0 NormalX=0 NormalY=0 NormalZ=1 AngleXU=0 Radius=1
    g42: BSplineCurve PolesCount=3 KnotsCount=2 Degree=2 IsPeriodic=0
    g43: GeomPoint X=-12.8401 Y=-17.6958 Z=0
    g44: GeomPoint X=-14 Y=-18 Z=0
    g45: LineSegment StartX=-6.2 StartY=0 StartZ=0 EndX=-7.2 EndY=0 EndZ=0
    g46: LineSegment StartX=-7.2 StartY=0 StartZ=0 EndX=-7.2 EndY=-2 EndZ=0
    g47: LineSegment StartX=-7.2 StartY=-2 StartZ=0 EndX=-6.2215 EndY=-2 EndZ=0
    g48: LineSegment StartX=-6.32538 StartY=-4 StartZ=0 EndX=-7.65538 EndY=-4 EndZ=0
    g49: LineSegment StartX=-7.65538 StartY=-4 StartZ=0 EndX=-7.65538 EndY=-5.99526 EndZ=0
    g50: LineSegment StartX=-7.65538 StartY=-5.99526 StartZ=0 EndX=-6.48644 EndY=-5.99526 EndZ=0
    g51: LineSegment StartX=-6.77343 StartY=-8 StartZ=0 EndX=-8.43343 EndY=-8 EndZ=0
    g52: LineSegment StartX=-8.43343 StartY=-8 StartZ=0 EndX=-8.43343 EndY=-10 EndZ=0
    g53: LineSegment StartX=-8.43343 StartY=-10 StartZ=0 EndX=-7.19003 EndY=-10 EndZ=0
  constraints (112):
    c: Horizontal(g0)
    c: Distance(g0) = 2
    c: Block(g0)
    c: Vertical(g1)
    c: Coincident(g2,g0)
    c: Vertical(g2)
    c: Block(g2)
    c: Coincident(g6,g2)
    c: Weight(g3) = 1
    c: Equal(g3,g4)
    c: Equal(g3,g5)
    c: InternalAlignment(g3,g6)
    c: InternalAlignment(g4,g6)
    c: InternalAlignment(g5,g6)
    c: InternalAlignment(g7,g6)
    c: InternalAlignment(g8,g6)
    c: Block(g6)
    c: Coincident(g9,g1)
    c: Coincident(g9,g6)
    c: Horizontal(g9)
    c: Vertical(g10)
    c: Block(g10)
    c: Horizontal(g11)
    c: Block(g11)
    c: Coincident(g12,g10)
    c: Horizontal(g12)
    c: Block(g12)
    c: Coincident(g13,g11)
    c: Vertical(g13)
    c: Block(g13)
    c: Coincident(g14,g10)
    c: Horizontal(g14)
    c: Block(g14)
    c: Block(g9)
    c: Block(g1)
    c: Weight(g15) = 1
    c: Equal(g15,g16)
    c: Equal(g15,g17)
    c: InternalAlignment(g15,g18)
    c: InternalAlignment(g16,g18)
    c: InternalAlignment(g17,g18)
    c: InternalAlignment(g19,g18)
    c: InternalAlignment(g20,g18)
    c: Weight(g21) = 1
    c: Equal(g21,g22)
    c: Equal(g21,g23)
    c: InternalAlignment(g21,g24)
    c: InternalAlignment(g22,g24)
    c: InternalAlignment(g23,g24)
    c: InternalAlignment(g25,g24)
    c: InternalAlignment(g26,g24)
    c: Weight(g27) = 1
    c: Equal(g27,g28)
    c: Equal(g27,g29)
    c: Coincident(g30,g14)
    c: InternalAlignment(g27,g30)
    c: InternalAlignment(g28,g30)
    c: InternalAlignment(g29,g30)
    c: InternalAlignment(g31,g30)
    c: InternalAlignment(g32,g30)
    c: Coincident(g36,g12)
    c: Weight(g33) = 1
    c: Equal(g33,g34)
    c: Equal(g33,g35)
    c: Coincident(g36,g11)
    c: InternalAlignment(g33,g36)
    c: InternalAlignment(g34,g36)
    c: InternalAlignment(g35,g36)
    c: InternalAlignment(g37,g36)
    c: InternalAlignment(g38,g36)
    c: Coincident(g42,g13)
    c: Weight(g39) = 1
    c: Equal(g39,g40)
    c: Equal(g39,g41)
    c: Coincident(g42,g1)
    c: InternalAlignment(g39,g42)
    c: InternalAlignment(g40,g42)
    c: InternalAlignment(g41,g42)
    c: InternalAlignment(g43,g42)
    c: InternalAlignment(g44,g42)
    c: Block(g18)
    c: Block(g24)
    c: Block(g30)
    c: Block(g36)
    c: Block(g42)
    c: Horizontal(g45)
    c: Coincident(g45,g0)
    c: Vertical(g46)
    c: Coincident(g46,g45)
    c: Coincident(g47,g46)
    c: Coincident(g47,g18)
    c: Horizontal(g47)
    c: Block(g46)
    c: Coincident(g48,g18)
    c: Horizontal(g48)
    c: Distance(g48) = 1.33
    c: Vertical(g49)
    c: Coincident(g49,g48)
    c: Coincident(g50,g49)
    c: Coincident(g50,g24)
    c: Horizontal(g50)
    c: Tangent(g50,g22)
    c: Horizontal(g51)
    c: Coincident(g51,g24)
    c: Block(g51)
    c: Vertical(g52)
    c: Block(g52)
    c: Coincident(g52,g51)
    c: Coincident(g53,g52)
    c: Coincident(g53,g30)
    c: Horizontal(g53)
    c: Distance(g1) = 8.5
FEATURE [Part::Feature] Face024
  shape: bbox 9.8 x 26.5 x 2e-07 mm, 1 faces, 0 solids (baked)
FEATURE [Part::Revolution] Revolve024
  Angle = 360
  Axis = (0,1,0)
  Base = (0,0,0)
  FaceMakerClass = Part::FaceMakerBullseye
  Placement = pos=(0,0,0) rot=(0,0,1;1.5708rad)
  Solid = false
  Source = -> Face024
  Symmetric = false
FEATURE [Part::Feature] Face025
  shape: bbox 9.8 x 26.5 x 2e-07 mm, 1 faces, 0 solids (baked)
FEATURE [Part::Revolution] Revolve025
  Angle = 360
  Axis = (0,1,0)
  Base = (0,0,0)
  FaceMakerClass = Part::FaceMakerBullseye
  Placement = pos=(0,0,0) rot=(0,0,1;1.5708rad)
  Solid = false
  Source = -> Face025
  Symmetric = false
FEATURE [Part::MultiFuse] Fusion033
  Placement = pos=(-18,19,36) rot=(0,0,1;0rad)
  Shapes = -> [Revolve025,Revolve024]
FEATURE [Part::Cylinder] Cylinder014
  Angle = 360
  AttacherType = Attacher::AttachEngine3D
  Height = 20
  Placement = pos=(0,0,36.15) rot=(0,0,1;0rad)
  Radius = 14.3
FEATURE [Part::Cylinder] Cylinder015
  Angle = 360
  AttacherType = Attacher::AttachEngine3D
  Height = 10
  Placement = pos=(0,0,36.15) rot=(0,0,1;0rad)
  Radius = 4
FEATURE [Part::MultiFuse] Fusion034  label="removeToCreteHoleForPlugHousing004"
  Placement = pos=(-42,19,36) rot=(0,1,0;1.5708rad)
  Shapes = -> [Cylinder014,Cylinder015]
FEATURE [Part::Cut] Cut008  label="top004"
  Base = -> Cut004
  Placement = pos=(-1,0,0) rot=(0,0,1;0rad)
  Tool = -> Fusion034
FEATURE [Part::Box] Box005  label="Cube005"
  AttacherType = Attacher::AttachEngine3D
  Height = 28
  Length = 3
  Placement = pos=(110.7,19,22) rot=(0,0,1;0rad)
  Width = 15.7
FEATURE [Part::Cylinder] Cylinder016
  Angle = 360
  AttacherType = Attacher::AttachEngine3D
  Height = 10
  Placement = pos=(0,0,36.15) rot=(0,0,1;0rad)
  Radius = 4
FEATURE [Part::Cylinder] Cylinder017
  Angle = 360
  AttacherType = Attacher::AttachEngine3D
  Height = 20
  Placement = pos=(0,0,36.15) rot=(0,0,1;0rad)
  Radius = 10.3
FEATURE [Part::MultiFuse] Fusion035  label="removeToCreteHoleForPlugHousing005"
  Placement = pos=(70,19,36) rot=(0,1,0;1.5708rad)
  Shapes = -> [Cylinder017,Cylinder016]
FEATURE [Part::Cut] Cut009  label="plugHousingTab001"
  Base = -> Box005
  Placement = pos=(-107.4,-14,0) rot=(0,0,1;0rad)
  Tool = -> Fusion035
FEATURE [Part::Box] Box006  label="Cube006"
  AttacherType = Attacher::AttachEngine3D
  Height = 28
  Length = 3
  Placement = pos=(110.7,19,22) rot=(0,0,1;0rad)
  Width = 15.7
FEATURE [Part::Cylinder] Cylinder018
  Angle = 360
  AttacherType = Attacher::AttachEngine3D
  Height = 10
  Placement = pos=(0,0,36.15) rot=(0,0,1;0rad)
  Radius = 4
FEATURE [Part::Cylinder] Cylinder019
  Angle = 360
  AttacherType = Attacher::AttachEngine3D
  Height = 20
  Placement = pos=(0,0,36.15) rot=(0,0,1;0rad)
  Radius = 10.3
FEATURE [Part::MultiFuse] Fusion036  label="removeToCreteHoleForPlugHousing006"
  Placement = pos=(70,19,36) rot=(0,1,0;1.5708rad)
  Shapes = -> [Cylinder019,Cylinder018]
FEATURE [Part::Cut] Cut010  label="plugHousingTab002"
  Base = -> Box006
  Placement = pos=(-107.4,-14,0) rot=(0,0,1;0rad)
  Tool = -> Fusion036
FEATURE [Part::MultiFuse] Fusion037
  Placement = pos=(9.6,23,0) rot=(0,0,1;3.14159rad)
  Shapes = -> [Cut009,Cut010]
FEATURE [Part::Box] Box  label="Cube"
  AttacherType = Attacher::AttachEngine3D
  Height = 10
  Length = 3
  Placement = pos=(3.3,4,12) rot=(0,0,1;0rad)
  Width = 10
FEATURE [Part::Fillet] Fillet004
  Base = -> Fusion028
  Edges = 1 edges r=2: [Edge25]
FEATURE [Part::Fillet] Fillet005  label="plugHousing046"
  Base = -> Fillet004
  Edges = 1 edges r=2: [Edge8]
FEATURE [Part::Fillet] Fillet006
  Base = -> Box
  Edges = 1 edges r=2: [Edge11]
FEATURE [Part::Box] Box007  label="Cube007"
  AttacherType = Attacher::AttachEngine3D
  Height = 10
  Length = 3
  Placement = pos=(3.3,4,50) rot=(0,0,1;0rad)
  Width = 10
FEATURE [Part::Fillet] Fillet007
  Base = -> Box007
  Edges = 1 edges r=2: [Edge12]
FEATURE [Part::Box] Box008  label="Cube008"
  AttacherType = Attacher::AttachEngine3D
  Height = 28
  Length = 4
  Placement = pos=(5,0,22) rot=(0,0,1;0rad)
  Width = 10
FEATURE [Part::Fillet] Fillet008
  Base = -> Box008
  Edges = 1 edges r=1: [Edge7]
FEATURE [Part::Fillet] Fillet009
  Base = -> Fillet008
  Edges = 1 edges r=2: [Edge5]
FEATURE [Part::Fillet] Fillet010
  Base = -> Fillet009
  Edges = 1 edges r=2: [Edge2]
FEATURE [Sketcher::SketchObject] Sketch009  label="topSketch003"
  FullyConstrained = true
  sketch-geometry (4):
    g0: LineSegment StartX=16.8446 StartY=31.512 StartZ=0 EndX=16.3251 EndY=34.4666 EndZ=0
    g1: ArcOfCircle CenterX=19 CenterY=19.2524 CenterZ=0 NormalX=0 NormalY=0 NormalZ=1 AngleXU=0 Radius=15.4476 StartAngle=1.74483 EndAngle=2.72717
    g2: ArcOfCircle CenterX=19 CenterY=19.2524 CenterZ=0 NormalX=0 NormalY=0 NormalZ=1 AngleXU=0 Radius=12.4476 StartAngle=1.74483 EndAngle=2.73189
    g3: LineSegment StartX=4.86004 StartY=25.4725 StartZ=0 EndX=7.58253 EndY=24.2107 EndZ=0
  constraints (7):
    c: Block(g0)
    c: Coincident(g1,g0)
    c: Coincident(g2,g0)
    c: Coincident(g3,g1)
    c: Coincident(g3,g2)
    c: Block(g1)
    c: Block(g2)
FEATURE [Part::Extrusion] Extrude008
  Base = -> Sketch009
  Dir = (0,0,1)
  DirMode = 2
  FaceMakerClass = Part::FaceMakerBullseye
  LengthFwd = 10
  LengthRev = 0
  Placement = pos=(0,0,31) rot=(0,0,1;0rad)
  Solid = true
  Symmetric = false
FEATURE [Part::Cylinder] Cylinder020
  Angle = 360
  AttacherType = Attacher::AttachEngine3D
  Height = 20
  Placement = pos=(0,0,36.15) rot=(0,0,1;0rad)
  Radius = 8.2
FEATURE [Part::Cylinder] Cylinder021
  Angle = 360
  AttacherType = Attacher::AttachEngine3D
  Height = 10
  Placement = pos=(0,0,36.15) rot=(0,0,1;0rad)
  Radius = 4
FEATURE [Part::MultiFuse] Fusion038  label="removeToCreteHoleForPlugHousing007"
  Placement = pos=(-42,19,36) rot=(0,1,0;1.5708rad)
  Shapes = -> [Cylinder020,Cylinder021]
FEATURE [Part::Cut] Cut011
  Base = -> Extrude008
  Tool = -> Fusion038
FEATURE [Part::Fillet] Fillet011
  Base = -> Cut011
  Edges = 1 edges r=2: [Edge1]
FEATURE [Part::Fillet] Fillet012
  Base = -> Fillet011
  Edges = 1 edges r=2.5: [Edge1]
FEATURE [Part::Fillet] Fillet013
  Base = -> Fillet012
  Edges = 1 edges r=2.5: [Edge2]
FEATURE [Part::Box] Box010  label="Cube010"
  AttacherType = Attacher::AttachEngine3D
  Height = 16
  Length = 8
  Placement = pos=(12.7,31.52,28) rot=(0,0,1;0rad)
  Width = 4
FEATURE [Sketcher::SketchObject] Sketch010  label="topSketch004"
  FullyConstrained = true
  sketch-geometry (4):
    g0: LineSegment StartX=16.8446 StartY=31.512 StartZ=0 EndX=16.3251 EndY=34.4666 EndZ=0
    g1: ArcOfCircle CenterX=19 CenterY=19.2524 CenterZ=0 NormalX=0 NormalY=0 NormalZ=1 AngleXU=0 Radius=15.4476 StartAngle=1.74483 EndAngle=2.72717
    g2: ArcOfCircle CenterX=19 CenterY=19.2524 CenterZ=0 NormalX=0 NormalY=0 NormalZ=1 AngleXU=0 Radius=12.4476 StartAngle=1.74483 EndAngle=2.73189
    g3: LineSegment StartX=4.86004 StartY=25.4725 StartZ=0 EndX=7.58253 EndY=24.2107 EndZ=0
  constraints (7):
    c: Block(g0)
    c: Coincident(g1,g0)
    c: Coincident(g2,g0)
    c: Coincident(g3,g1)
    c: Coincident(g3,g2)
    c: Block(g1)
    c: Block(g2)
FEATURE [Part::Cylinder] Cylinder022
  Angle = 360
  AttacherType = Attacher::AttachEngine3D
  Height = 10
  Placement = pos=(0,0,36.15) rot=(0,0,1;0rad)
  Radius = 4
FEATURE [Sketcher::SketchObject] Sketch011  label="topSketch005"
  FullyConstrained = true
  sketch-geometry (4):
    g0: LineSegment StartX=16.8446 StartY=31.512 StartZ=0 EndX=16.3251 EndY=34.4666 EndZ=0
    g1: ArcOfCircle CenterX=19 CenterY=19.2524 CenterZ=0 NormalX=0 NormalY=0 NormalZ=1 AngleXU=0 Radius=15.4476 StartAngle=1.74483 EndAngle=2.72717
    g2: ArcOfCircle CenterX=19 CenterY=19.2524 CenterZ=0 NormalX=0 NormalY=0 NormalZ=1 AngleXU=0 Radius=12.4476 StartAngle=1.74483 EndAngle=2.73189
    g3: LineSegment StartX=4.86004 StartY=25.4725 StartZ=0 EndX=7.58253 EndY=24.2107 EndZ=0
  constraints (7):
    c: Block(g0)
    c: Coincident(g1,g0)
    c: Coincident(g2,g0)
    c: Coincident(g3,g1)
    c: Coincident(g3,g2)
    c: Block(g1)
    c: Block(g2)
FEATURE [Part::Extrusion] Extrude010
  Base = -> Sketch011
  Dir = (0,0,1)
  DirMode = 2
  FaceMakerClass = Part::FaceMakerBullseye
  LengthFwd = 10.6
  LengthRev = 0
  Placement = pos=(0,0,31) rot=(0,0,1;0rad)
  Solid = true
  Symmetric = false
FEATURE [Part::Cylinder] Cylinder023
  Angle = 360
  AttacherType = Attacher::AttachEngine3D
  Height = 20
  Placement = pos=(0,0,36.15) rot=(0,0,1;0rad)
  Radius = 8.2
FEATURE [Part::MultiFuse] Fusion039  label="removeToCreteHoleForPlugHousing008"
  Placement = pos=(-42,19,36) rot=(0,1,0;1.5708rad)
  Shapes = -> [Cylinder023,Cylinder022]
FEATURE [Part::Cut] Cut012
  Base = -> Extrude010
  Placement = pos=(0,0,-0.3) rot=(0,0,1;0rad)
  Tool = -> Fusion039
FEATURE [Part::Cut] Cut013
  Base = -> Box010
  Tool = -> Cut012
FEATURE [Part::Fillet] Fillet014
  Base = -> Cut013
  Edges = 1 edges r=0.7: [Edge13]
FEATURE [Part::Fillet] Fillet015
  Base = -> Fillet014
  Edges = 1 edges r=0.7: [Edge13]
FEATURE [Part::Fillet] Fillet016
  Base = -> Fillet015
  Edges = 1 edges r=0.7: [Edge16]
FEATURE [Part::Fillet] Fillet017
  Base = -> Fillet016
  Edges = 1 edges r=0.7: [Edge11]
FEATURE [Part::Fillet] Fillet018
  Base = -> Fillet017
  Edges = 1 edges r=0.7: [Edge10]
FEATURE [Part::Fillet] Fillet019
  Base = -> Fillet018
  Edges = 1 edges r=1.2: [Edge5]
FEATURE [Part::Fillet] Fillet020
  Base = -> Fillet019
  Edges = 1 edges r=1.2: [Edge12]
FEATURE [Part::Fillet] Fillet021
  Base = -> Fillet020
  Edges = 1 edges r=2: [Edge1]
  Placement = pos=(0.3,0,0) rot=(0,0,1;0rad)
FEATURE [Part::MultiFuse] Fusion040  label="top005"
  Shapes = -> [Cut008,Fillet021]
FEATURE [Part::MultiFuse] Fusion041  label="wireHolder"
  Shapes = -> [Fusion033,Fillet013]
FEATURE [Part::MultiFuse] Fusion042
  Shapes = -> [Fillet007,Fusion041]
FEATURE [Part::MultiFuse] Fusion043  label="wireHolder001"
  Shapes = -> [Fusion042,Fillet010]
FEATURE [Part::MultiFuse] Fusion044  label="wireHolder002"
  Shapes = -> [Fillet006,Fusion037,Fusion043]
FEATURE [Part::Feature] Face026
  shape: bbox 11 x 6 x 2e-07 mm, 1 faces, 0 solids (baked)
FEATURE [Part::Revolution] Revolve026
  Angle = 360
  Axis = (0,1,0)
  Base = (0,0,0)
  FaceMakerClass = Part::FaceMakerBullseye
  Placement = pos=(30.3,-1,19.7) rot=(0,0,1;0rad)
  Solid = false
  Source = -> Face026
  Symmetric = false
FEATURE [Sketcher::SketchObject] Sketch013  label="topSketch006"
  FullyConstrained = true
  sketch-geometry (13):
    g0: LineSegment StartX=117 StartY=19 StartZ=0 EndX=117 EndY=38 EndZ=0
    g1: ArcOfCircle CenterX=98 CenterY=19 CenterZ=0 NormalX=0 NormalY=0 NormalZ=1 AngleXU=0 Radius=19 StartAngle=5.7297 EndAngle=6.28319
    g2: LineSegment StartX=0 StartY=3 StartZ=0 EndX=0 EndY=19 EndZ=0
    g3: LineSegment StartX=19 StartY=38 StartZ=0 EndX=117 EndY=38 EndZ=0
    g4: ArcOfCircle CenterX=19 CenterY=19 CenterZ=0 NormalX=0 NormalY=0 NormalZ=1 AngleXU=0 Radius=19 StartAngle=1.5708 EndAngle=3.14159
    g5: ArcOfCircle CenterX=19 CenterY=19 CenterZ=0 NormalX=0 NormalY=0 NormalZ=1 AngleXU=0 Radius=16 StartAngle=1.5708 EndAngle=3.14159
    g6: ArcOfCircle CenterX=98 CenterY=19 CenterZ=0 NormalX=0 NormalY=0 NormalZ=1 AngleXU=0 Radius=16 StartAngle=5.60905 EndAngle=6.28319
    g7: LineSegment StartX=114 StartY=19 StartZ=0 EndX=114 EndY=35 EndZ=0
    g8: LineSegment StartX=110.5 StartY=9.01251 StartZ=0 EndX=114.163 EndY=9.01251 EndZ=0
    g9: LineSegment StartX=114 StartY=35 StartZ=0 EndX=19 EndY=35 EndZ=0
    g10: LineSegment StartX=0 StartY=3 StartZ=0 EndX=0 EndY=0 EndZ=0
    g11: LineSegment StartX=3 StartY=0 StartZ=0 EndX=0 EndY=0 EndZ=0
    g12: LineSegment StartX=3 StartY=19 StartZ=0 EndX=3 EndY=0 EndZ=0
  constraints (33):
    c: Vertical(g0)
    c: Distance(g0) = 19
    c: Block(g0)
    c: Coincident(g1,g0)
    c: Block(g1)
    c: Vertical(g2)
    c: Block(g2)
    c: Coincident(g3,g0)
    c: Horizontal(g3)
    c: Distance(g3) = 98
    c: Coincident(g4,g3)
    c: Coincident(g4,g2)
    c: Block(g4)
    c: Coincident(g5,g4)
    c: Coincident(g6,g1)
    c: Block(g6)
    c: Block(g5)
    c: Coincident(g7,g6)
    c: Vertical(g7)
    c: Coincident(g8,g6)
    c: Coincident(g8,g1)
    c: Coincident(g9,g7)
    c: Coincident(g9,g5)
    c: Horizontal(g9)
    c: Tangent(g9,g5)
    c: Coincident(g10,g2)
    c: Distance(g10) = 3
    c: Vertical(g10)
    c: Coincident(g11,g10)
    c: Horizontal(g11)
    c: Coincident(g12,g5)
    c: Coincident(g12,g11)
    c: Vertical(g12)
FEATURE [Part::Extrusion] Extrude011  label="top006"
  Base = -> Sketch013
  Dir = (0,0,1)
  DirMode = 2
  FaceMakerClass = Part::FaceMakerBullseye
  LengthFwd = 72
  LengthRev = 0
  Solid = true
  Symmetric = false
FEATURE [Sketcher::SketchObject] Sketch014
  FullyConstrained = true
  MapMode = 3
  Placement = pos=(0,0,0) rot=(1,0,0;1.5708rad)
  Support = -> [Extrude011]
  sketch-geometry (8):
    g0: Circle CenterX=80.351 CenterY=-67.6202 CenterZ=0 NormalX=0 NormalY=0 NormalZ=1 AngleXU=0 Radius=2
    g1: Circle CenterX=80.351 CenterY=-67.6202 CenterZ=0 NormalX=0 NormalY=0 NormalZ=1 AngleXU=0 Radius=3
    g2: Circle CenterX=80.351 CenterY=-4.92017 CenterZ=0 NormalX=0 NormalY=0 NormalZ=1 AngleXU=0 Radius=2
    g3: Circle CenterX=80.351 CenterY=-4.92017 CenterZ=0 NormalX=0 NormalY=0 NormalZ=1 AngleXU=0 Radius=3
    g4: Circle CenterX=23.851 CenterY=-4.92017 CenterZ=0 NormalX=0 NormalY=0 NormalZ=1 AngleXU=0 Radius=2
    g5: Circle CenterX=23.851 CenterY=-4.92017 CenterZ=0 NormalX=0 NormalY=0 NormalZ=1 AngleXU=0 Radius=3
    g6: Circle CenterX=23.851 CenterY=-67.6202 CenterZ=0 NormalX=0 NormalY=0 NormalZ=1 AngleXU=0 Radius=2
    g7: Circle CenterX=23.851 CenterY=-67.6202 CenterZ=0 NormalX=0 NormalY=0 NormalZ=1 AngleXU=0 Radius=3
  constraints (8):
    c: Block(g3)
    c: Block(g2)
    c: Block(g1)
    c: Block(g0)
    c: Block(g6)
    c: Block(g7)
    c: Block(g4)
    c: Block(g5)
FEATURE [Part::Feature] Face027
  shape: bbox 11 x 6 x 2e-07 mm, 1 faces, 0 solids (baked)
FEATURE [Part::Revolution] Revolve027
  Angle = 360
  Axis = (0,1,0)
  Base = (0,0,0)
  FaceMakerClass = Part::FaceMakerBullseye
  Placement = pos=(30.3,-1,51.7) rot=(0,0,1;0rad)
  Solid = false
  Source = -> Face027
  Symmetric = false
FEATURE [Part::Feature] Face028
  shape: bbox 11 x 6 x 2e-07 mm, 1 faces, 0 solids (baked)
FEATURE [Part::Revolution] Revolve028
  Angle = 360
  Axis = (0,1,0)
  Base = (0,0,0)
  FaceMakerClass = Part::FaceMakerBullseye
  Placement = pos=(62.3,-1,19.7) rot=(0,0,1;0rad)
  Solid = false
  Source = -> Face028
  Symmetric = false
FEATURE [Part::Feature] Face029
  shape: bbox 11 x 6 x 2e-07 mm, 1 faces, 0 solids (baked)
FEATURE [Part::Revolution] Revolve029
  Angle = 360
  Axis = (0,1,0)
  Base = (0,0,0)
  FaceMakerClass = Part::FaceMakerBullseye
  Placement = pos=(62.3,-1,51.7) rot=(0,0,1;0rad)
  Solid = false
  Source = -> Face029
  Symmetric = false
FEATURE [Part::Feature] Wire
  shape: bbox 11 x 5.2 x 2e-07 mm, 0 faces, 0 solids (baked)
FEATURE [Part::Revolution] Revolve030
  Angle = 360
  Axis = (0,1,0)
  Base = (0,0,0)
  FaceMakerClass = Part::FaceMakerBullseye
  Placement = pos=(30.3,38,19.7) rot=(0,0,1;0rad)
  Solid = true
  Source = -> Wire
  Symmetric = false
FEATURE [Part::Feature] Wire001
  shape: bbox 11 x 5.2 x 2e-07 mm, 0 faces, 0 solids (baked)
FEATURE [Part::Revolution] Revolve031
  Angle = 360
  Axis = (0,1,0)
  Base = (0,0,0)
  FaceMakerClass = Part::FaceMakerBullseye
  Placement = pos=(30.3,38,51.7) rot=(0,0,1;0rad)
  Solid = true
  Source = -> Wire001
  Symmetric = false
FEATURE [Part::Feature] Wire002
  shape: bbox 11 x 5.2 x 2e-07 mm, 0 faces, 0 solids (baked)
FEATURE [Part::Revolution] Revolve032
  Angle = 360
  Axis = (0,1,0)
  Base = (0,0,0)
  FaceMakerClass = Part::FaceMakerBullseye
  Placement = pos=(62.3,38,51.7) rot=(0,0,1;0rad)
  Solid = true
  Source = -> Wire002
  Symmetric = false
FEATURE [Part::Feature] Wire003
  shape: bbox 11 x 5.2 x 2e-07 mm, 0 faces, 0 solids (baked)
FEATURE [Part::Revolution] Revolve033
  Angle = 360
  Axis = (0,1,0)
  Base = (0,0,0)
  FaceMakerClass = Part::FaceMakerBullseye
  Placement = pos=(62.3,38,19.7) rot=(0,0,1;0rad)
  Solid = true
  Source = -> Wire003
  Symmetric = false
FEATURE [Part::MultiFuse] Fusion045  label="altRandScrewHousing"
  Shapes = -> [Revolve029,Revolve027,Revolve028,Revolve026]
FEATURE [Part::MultiFuse] Fusion046  label="fanScrewHousing"
  Shapes = -> [Revolve033,Revolve032,Revolve031,Revolve030]
FEATURE [Sketcher::SketchObject] Sketch015
  FullyConstrained = true
  sketch-geometry (17):
    g0: Circle CenterX=-3.5 CenterY=23.5 CenterZ=0 NormalX=0 NormalY=0 NormalZ=1 AngleXU=0 Radius=1
    g1: Circle CenterX=-1 CenterY=15.25 CenterZ=0 NormalX=0 NormalY=0 NormalZ=1 AngleXU=0 Radius=1
    g2: Circle CenterX=-3.5 CenterY=7 CenterZ=0 NormalX=0 NormalY=0 NormalZ=1 AngleXU=0 Radius=1
    g3: BSplineCurve PolesCount=3 KnotsCount=2 Degree=2 IsPeriodic=0
    g4: GeomPoint X=-3.5 Y=23.5 Z=0
    g5: GeomPoint X=-3.5 Y=7 Z=0
    g6: Circle CenterX=-4.8 CenterY=30.5 CenterZ=0 NormalX=0 NormalY=0 NormalZ=1 AngleXU=0 Radius=1
    g7: Circle CenterX=-3.5 CenterY=30.5 CenterZ=0 NormalX=0 NormalY=0 NormalZ=1 AngleXU=0 Radius=1
    g8: Circle CenterX=-3.5 CenterY=29.2 CenterZ=0 NormalX=0 NormalY=0 NormalZ=1 AngleXU=0 Radius=1
    g9: BSplineCurve PolesCount=3 KnotsCount=2 Degree=2 IsPeriodic=0
    g10: GeomPoint X=-4.8 Y=30.5 Z=0
    g11: GeomPoint X=-3.5 Y=29.2 Z=0
    g12: LineSegment StartX=-3.5 StartY=29.2 StartZ=0 EndX=-3.5 EndY=23.5 EndZ=0
    g13: LineSegment StartX=-4.8 StartY=30.5 StartZ=0 EndX=0 EndY=30.5 EndZ=0
    g14: LineSegment StartX=-3.5 StartY=0.3 StartZ=0 EndX=0 EndY=0.3 EndZ=0
    g15: LineSegment StartX=-3.5 StartY=0.3 StartZ=0 EndX=-3.5 EndY=7 EndZ=0
    g16: LineSegment StartX=0 StartY=0.3 StartZ=0 EndX=0 EndY=30.5 EndZ=0
  constraints (33):
    c: Weight(g0) = 1
    c: Equal(g0,g1)
    c: Equal(g0,g2)
    c: InternalAlignment(g0,g3)
    c: InternalAlignment(g1,g3)
    c: InternalAlignment(g2,g3)
    c: InternalAlignment(g4,g3)
    c: InternalAlignment(g5,g3)
    c: Block(g3)
    c: Weight(g6) = 1
    c: Equal(g6,g7)
    c: Equal(g6,g8)
    c: InternalAlignment(g6,g9)
    c: InternalAlignment(g7,g9)
    c: InternalAlignment(g8,g9)
    c: InternalAlignment(g10,g9)
    c: InternalAlignment(g11,g9)
    c: Block(g9)
    c: Coincident(g12,g9)
    c: Coincident(g12,g3)
    c: Vertical(g12)
    c: Coincident(g13,g9)
    c: Horizontal(g13)
    c: Distance(g13) = 4.8
    c: Horizontal(g14)
    c: Block(g14)
    c: Coincident(g15,g14)
    c: Coincident(g15,g3)
    c: Vertical(g15)
    c: Coincident(g16,g14)
    c: Coincident(g16,g13)
    c: Vertical(g16)
    c: Tangent(g16,g1)
FEATURE [Sketcher::SketchObject] Sketch016
  FullyConstrained = true
  sketch-geometry (16):
    g0: Circle CenterX=-3.5 CenterY=23.5 CenterZ=0 NormalX=0 NormalY=0 NormalZ=1 AngleXU=0 Radius=1
    g1: Circle CenterX=-1 CenterY=15.25 CenterZ=0 NormalX=0 NormalY=0 NormalZ=1 AngleXU=0 Radius=1
    g2: Circle CenterX=-3.5 CenterY=7 CenterZ=0 NormalX=0 NormalY=0 NormalZ=1 AngleXU=0 Radius=1
    g3: BSplineCurve PolesCount=3 KnotsCount=2 Degree=2 IsPeriodic=0
    g4: GeomPoint X=-3.5 Y=23.5 Z=0
    g5: GeomPoint X=-3.5 Y=7 Z=0
    g6: LineSegment StartX=-3.5 StartY=28.2 StartZ=0 EndX=-3.5 EndY=23.5 EndZ=0
    g7: LineSegment StartX=0 StartY=29.5 StartZ=0 EndX=0 EndY=30 EndZ=0
    g8: LineSegment StartX=-3.5 StartY=28.2 StartZ=0 EndX=-3.5 EndY=30 EndZ=0
    g9: LineSegment StartX=0 StartY=30 StartZ=0 EndX=0 EndY=30.5 EndZ=0
    g10: LineSegment StartX=0 StartY=30.5 StartZ=0 EndX=-3.5 EndY=30.5 EndZ=0
    g11: LineSegment StartX=-3.5 StartY=30.5 StartZ=0 EndX=-3.5 EndY=30 EndZ=0
    g12: LineSegment StartX=0 StartY=29.5 StartZ=0 EndX=0 EndY=5 EndZ=0
    g13: LineSegment StartX=-3.5 StartY=0.3 StartZ=0 EndX=-3.5 EndY=7 EndZ=0
    g14: LineSegment StartX=-3.5 StartY=0.3 StartZ=0 EndX=0 EndY=0.3 EndZ=0
    g15: LineSegment StartX=0 StartY=5 StartZ=0 EndX=0 EndY=0.3 EndZ=0
  constraints (39):
    c: Weight(g0) = 1
    c: Equal(g0,g1)
    c: Equal(g0,g2)
    c: InternalAlignment(g0,g3)
    c: InternalAlignment(g1,g3)
    c: InternalAlignment(g2,g3)
    c: InternalAlignment(g4,g3)
    c: InternalAlignment(g5,g3)
    c: Block(g3)
    c: Coincident(g6,g3)
    c: Vertical(g6)
    c: Vertical(g7)
    c: Distance(g7) = 0.5
    c: Coincident(g8,g6)
    c: Vertical(g8)
    c: Block(g6)
    c: Block(g7)
    c: Vertical(g9)
    c: Equal(g7,g9) = 0.5
    c: Block(g9)
    c: Coincident(g9,g7)
    c: Horizontal(g10)
    c: Coincident(g10,g9)
    c: Coincident(g11,g10)
    c: Coincident(g11,g8)
    c: Vertical(g11)
    c: Block(g11)
    c: Coincident(g12,g7)
    c: Vertical(g12)
    c: Coincident(g13,g3)
    c: Vertical(g13)
    c: Distance(g13) = 6.7
    c: Coincident(g14,g13)
    c: Horizontal(g14)
    c: Block(g14)
    c: Coincident(g15,g12)
    c: Coincident(g15,g14)
    c: Vertical(g15)
    c: Block(g15)
FEATURE [Sketcher::SketchObject] Sketch017
  FullyConstrained = true
  sketch-geometry (11):
    g0: LineSegment StartX=-3.5 StartY=1e-16 StartZ=0 EndX=-1.6 EndY=1e-16 EndZ=0
    g1: LineSegment StartX=-1.6 StartY=1e-16 StartZ=0 EndX=-1.6 EndY=1.5 EndZ=0
    g2: LineSegment StartX=-3.5 StartY=1.5 StartZ=0 EndX=-1.6 EndY=1.5 EndZ=0
    g3: LineSegment StartX=-3.5 StartY=1e-16 StartZ=0 EndX=-4.8 EndY=1e-16 EndZ=0
    g4: Circle CenterX=-3.5 CenterY=1.3 CenterZ=0 NormalX=0 NormalY=0 NormalZ=1 AngleXU=0 Radius=1
    g5: Circle CenterX=-3.5 CenterY=1e-16 CenterZ=0 NormalX=0 NormalY=0 NormalZ=1 AngleXU=0 Radius=1
    g6: Circle CenterX=-4.8 CenterY=1e-16 CenterZ=0 NormalX=0 NormalY=0 NormalZ=1 AngleXU=0 Radius=1
    g7: BSplineCurve PolesCount=3 KnotsCount=2 Degree=2 IsPeriodic=0
    g8: GeomPoint X=-3.5 Y=1.3 Z=0
    g9: GeomPoint X=-4.8 Y=1e-16 Z=0
    g10: LineSegment StartX=-3.5 StartY=1.3 StartZ=0 EndX=-3.5 EndY=1.5 EndZ=0
  constraints (24):
    c: Horizontal(g0)
    c: Distance(g0) = 1.9
    c: Block(g0)
    c: Coincident(g1,g0)
    c: Vertical(g1)
    c: Coincident(g2,g1)
    c: Horizontal(g2)
    c: Coincident(g3,g0)
    c: Horizontal(g3)
    c: Distance(g3) = 1.3
    c: Weight(g4) = 1
    c: Equal(g4,g5)
    c: Coincident(g5,g0)
    c: Equal(g4,g6)
    c: Coincident(g7,g3)
    c: InternalAlignment(g4,g7)
    c: InternalAlignment(g5,g7)
    c: InternalAlignment(g6,g7)
    c: InternalAlignment(g8,g7)
    c: InternalAlignment(g9,g7)
    c: Coincident(g10,g7)
    c: Coincident(g10,g2)
    c: Vertical(g10)
    c: Block(g10)
FEATURE [Part::Feature] Face035
  shape: bbox 3.2 x 1.5 x 2e-07 mm, 1 faces, 0 solids (baked)
FEATURE [Part::Revolution] Revolve039  label="backCaseScrewRetainer"
  Angle = 360
  Axis = (0,1,0)
  Base = (0,0,0)
  FaceMakerClass = Part::FaceMakerBullseye
  Placement = pos=(12.5,3,62) rot=(0,0,1;0rad)
  Solid = false
  Source = -> Face035
  Symmetric = false
FEATURE [Part::Feature] Face036
  shape: bbox 3.2 x 1.5 x 2e-07 mm, 1 faces, 0 solids (baked)
FEATURE [Part::Feature] Face039
  shape: bbox 4.8 x 30.2 x 2e-07 mm, 1 faces, 0 solids (baked)
FEATURE [Part::Revolution] Revolve043  label="frontCaseScrewPost002"
  Angle = 360
  Axis = (0,1,0)
  Base = (0,0,0)
  FaceMakerClass = Part::FaceMakerBullseye
  Placement = pos=(89.5,4.5,3.5) rot=(0,0,1;0rad)
  Solid = false
  Source = -> Face039
  Symmetric = false
FEATURE [Part::Feature] Face042
  shape: bbox 4.8 x 30.2 x 2e-07 mm, 1 faces, 0 solids (baked)
FEATURE [Part::Revolution] Revolve046  label="frontCaseScrewPost003"
  Angle = 360
  Axis = (0,1,0)
  Base = (0,0,0)
  FaceMakerClass = Part::FaceMakerBullseye
  Placement = pos=(89.5,4.5,68.5) rot=(0,0,1;0rad)
  Solid = false
  Source = -> Face042
  Symmetric = false
FEATURE [Part::Feature] Face043
  shape: bbox 3.2 x 1.5 x 2e-07 mm, 1 faces, 0 solids (baked)
FEATURE [Part::Revolution] Revolve047  label="frontCaseScrewRetainer002"
  Angle = 360
  Axis = (0,1,0)
  Base = (0,0,0)
  FaceMakerClass = Part::FaceMakerBullseye
  Placement = pos=(89.5,3,68.5) rot=(0,0,1;0rad)
  Solid = false
  Source = -> Face043
  Symmetric = false
FEATURE [Part::Feature] Face044
  shape: bbox 3.2 x 1.5 x 2e-07 mm, 1 faces, 0 solids (baked)
FEATURE [Part::Revolution] Revolve048  label="frontCaseScrewRetainer003"
  Angle = 360
  Axis = (0,1,0)
  Base = (0,0,0)
  FaceMakerClass = Part::FaceMakerBullseye
  Placement = pos=(89.5,3,3.5) rot=(0,0,1;0rad)
  Solid = false
  Source = -> Face044
  Symmetric = false
FEATURE [App::MeasureDistance] Distance002  label="Distance: 1.67 mm"
  Distance = 1.66921
  P1 = (99.2361,4.7524,71.7)
  P2 = (99.2347,6.42161,71.7)
FEATURE [Sketcher::SketchObject] Sketch018
  FullyConstrained = true
  sketch-geometry (7):
    g0: LineSegment StartX=0 StartY=0 StartZ=0 EndX=0 EndY=6 EndZ=0
    g1: Circle CenterX=0 CenterY=0 CenterZ=0 NormalX=0 NormalY=0 NormalZ=1 AngleXU=0 Radius=1
    g2: Circle CenterX=8 CenterY=6 CenterZ=0 NormalX=0 NormalY=0 NormalZ=1 AngleXU=0 Radius=1
    g3: BSplineCurve PolesCount=3 KnotsCount=2 Degree=2 IsPeriodic=0
    g4: GeomPoint X=0 Y=0 Z=0
    g5: GeomPoint X=8 Y=6 Z=0
    g6: LineSegment StartX=0 StartY=6 StartZ=0 EndX=8 EndY=6 EndZ=0
  constraints (14):
    c: Coincident(g0,g-1)
    c: Distance(g0) = 6
    c: Vertical(g0)
    c: Coincident(g3,g0)
    c: Weight(g1) = 1
    c: Equal(g1,g2)
    c: InternalAlignment(g1,g3)
    c: InternalAlignment(g2,g3)
    c: InternalAlignment(g4,g3)
    c: InternalAlignment(g5,g3)
    c: Block(g3)
    c: Coincident(g6,g0)
    c: Coincident(g6,g3)
    c: Horizontal(g6)
FEATURE [Part::Extrusion] Extrude012  label="caseScrewPillarBracket"
  Base = -> Sketch018
  Dir = (0,0,1)
  DirMode = 2
  FaceMakerClass = Part::FaceMakerBullseye
  LengthFwd = 2.4
  LengthRev = 0
  Placement = pos=(15.76,29,8.8) rot=(0,1,0;0rad)
  Solid = true
  Symmetric = false
FEATURE [Sketcher::SketchObject] Sketch019
  FullyConstrained = true
  sketch-geometry (7):
    g0: LineSegment StartX=0 StartY=0 StartZ=0 EndX=0 EndY=6 EndZ=0
    g1: Circle CenterX=0 CenterY=0 CenterZ=0 NormalX=0 NormalY=0 NormalZ=1 AngleXU=0 Radius=1
    g2: Circle CenterX=8 CenterY=6 CenterZ=0 NormalX=0 NormalY=0 NormalZ=1 AngleXU=0 Radius=1
    g3: BSplineCurve PolesCount=3 KnotsCount=2 Degree=2 IsPeriodic=0
    g4: GeomPoint X=0 Y=0 Z=0
    g5: GeomPoint X=8 Y=6 Z=0
    g6: LineSegment StartX=0 StartY=6 StartZ=0 EndX=8 EndY=6 EndZ=0
  constraints (14):
    c: Coincident(g0,g-1)
    c: Distance(g0) = 6
    c: Vertical(g0)
    c: Coincident(g3,g0)
    c: Weight(g1) = 1
    c: Equal(g1,g2)
    c: InternalAlignment(g1,g3)
    c: InternalAlignment(g2,g3)
    c: InternalAlignment(g4,g3)
    c: InternalAlignment(g5,g3)
    c: Block(g3)
    c: Coincident(g6,g0)
    c: Coincident(g6,g3)
    c: Horizontal(g6)
FEATURE [Part::Extrusion] Extrude013  label="caseScrewPillarBracket001"
  Base = -> Sketch019
  Dir = (0,0,1)
  DirMode = 2
  FaceMakerClass = Part::FaceMakerBullseye
  LengthFwd = 2.4
  LengthRev = 0
  Placement = pos=(15.76,29,60.8) rot=(0,0,1;0rad)
  Solid = true
  Symmetric = false
FEATURE [Sketcher::SketchObject] Sketch020
  FullyConstrained = true
  sketch-geometry (7):
    g0: LineSegment StartX=0 StartY=0 StartZ=0 EndX=0 EndY=6 EndZ=0
    g1: Circle CenterX=0 CenterY=0 CenterZ=0 NormalX=0 NormalY=0 NormalZ=1 AngleXU=0 Radius=1
    g2: Circle CenterX=8 CenterY=6 CenterZ=0 NormalX=0 NormalY=0 NormalZ=1 AngleXU=0 Radius=1
    g3: BSplineCurve PolesCount=3 KnotsCount=2 Degree=2 IsPeriodic=0
    g4: GeomPoint X=0 Y=0 Z=0
    g5: GeomPoint X=8 Y=6 Z=0
    g6: LineSegment StartX=0 StartY=6 StartZ=0 EndX=8 EndY=6 EndZ=0
  constraints (14):
    c: Coincident(g0,g-1)
    c: Distance(g0) = 6
    c: Vertical(g0)
    c: Coincident(g3,g0)
    c: Weight(g1) = 1
    c: Equal(g1,g2)
    c: InternalAlignment(g1,g3)
    c: InternalAlignment(g2,g3)
    c: InternalAlignment(g4,g3)
    c: InternalAlignment(g5,g3)
    c: Block(g3)
    c: Coincident(g6,g0)
    c: Coincident(g6,g3)
    c: Horizontal(g6)
FEATURE [Part::Extrusion] Extrude014  label="caseScrewPillarBracket002"
  Base = -> Sketch020
  Dir = (0,0,1)
  DirMode = 2
  FaceMakerClass = Part::FaceMakerBullseye
  LengthFwd = 2.4
  LengthRev = 0
  Placement = pos=(13.7,29,13.26) rot=(0,-1,0;1.5708rad)
  Solid = true
  Symmetric = false
FEATURE [Sketcher::SketchObject] Sketch021
  FullyConstrained = true
  sketch-geometry (7):
    g0: LineSegment StartX=0 StartY=0 StartZ=0 EndX=0 EndY=6 EndZ=0
    g1: Circle CenterX=0 CenterY=0 CenterZ=0 NormalX=0 NormalY=0 NormalZ=1 AngleXU=0 Radius=1
    g2: Circle CenterX=8 CenterY=6 CenterZ=0 NormalX=0 NormalY=0 NormalZ=1 AngleXU=0 Radius=1
    g3: BSplineCurve PolesCount=3 KnotsCount=2 Degree=2 IsPeriodic=0
    g4: GeomPoint X=0 Y=0 Z=0
    g5: GeomPoint X=8 Y=6 Z=0
    g6: LineSegment StartX=0 StartY=6 StartZ=0 EndX=8 EndY=6 EndZ=0
  constraints (14):
    c: Coincident(g0,g-1)
    c: Distance(g0) = 6
    c: Vertical(g0)
    c: Coincident(g3,g0)
    c: Weight(g1) = 1
    c: Equal(g1,g2)
    c: InternalAlignment(g1,g3)
    c: InternalAlignment(g2,g3)
    c: InternalAlignment(g4,g3)
    c: InternalAlignment(g5,g3)
    c: Block(g3)
    c: Coincident(g6,g0)
    c: Coincident(g6,g3)
    c: Horizontal(g6)
FEATURE [Part::Extrusion] Extrude015  label="caseScrewPillarBracket003"
  Base = -> Sketch021
  Dir = (0,0,1)
  DirMode = 2
  FaceMakerClass = Part::FaceMakerBullseye
  LengthFwd = 2.4
  LengthRev = 0
  Placement = pos=(11.3,29,58.74) rot=(0,1,0;1.5708rad)
  Solid = true
  Symmetric = false
FEATURE [Sketcher::SketchObject] Sketch022
  FullyConstrained = true
  sketch-geometry (7):
    g0: LineSegment StartX=0 StartY=0 StartZ=0 EndX=0 EndY=6 EndZ=0
    g1: Circle CenterX=0 CenterY=0 CenterZ=0 NormalX=0 NormalY=0 NormalZ=1 AngleXU=0 Radius=1
    g2: Circle CenterX=8 CenterY=6 CenterZ=0 NormalX=0 NormalY=0 NormalZ=1 AngleXU=0 Radius=1
    g3: BSplineCurve PolesCount=3 KnotsCount=2 Degree=2 IsPeriodic=0
    g4: GeomPoint X=0 Y=0 Z=0
    g5: GeomPoint X=8 Y=6 Z=0
    g6: LineSegment StartX=0 StartY=6 StartZ=0 EndX=8 EndY=6 EndZ=0
  constraints (14):
    c: Coincident(g0,g-1)
    c: Distance(g0) = 6
    c: Vertical(g0)
    c: Coincident(g3,g0)
    c: Weight(g1) = 1
    c: Equal(g1,g2)
    c: InternalAlignment(g1,g3)
    c: InternalAlignment(g2,g3)
    c: InternalAlignment(g4,g3)
    c: InternalAlignment(g5,g3)
    c: Block(g3)
    c: Coincident(g6,g0)
    c: Coincident(g6,g3)
    c: Horizontal(g6)
FEATURE [Part::Extrusion] Extrude016  label="caseScrewPillarBracket004"
  Base = -> Sketch022
  Dir = (0,0,1)
  DirMode = 2
  FaceMakerClass = Part::FaceMakerBullseye
  LengthFwd = 2.4
  LengthRev = 0
  Placement = pos=(88.3,29,65.23) rot=(0,1,0;1.5708rad)
  Solid = true
  Symmetric = false
FEATURE [Sketcher::SketchObject] Sketch023
  FullyConstrained = true
  sketch-geometry (7):
    g0: LineSegment StartX=0 StartY=0 StartZ=0 EndX=0 EndY=6 EndZ=0
    g1: Circle CenterX=0 CenterY=0 CenterZ=0 NormalX=0 NormalY=0 NormalZ=1 AngleXU=0 Radius=1
    g2: Circle CenterX=8 CenterY=6 CenterZ=0 NormalX=0 NormalY=0 NormalZ=1 AngleXU=0 Radius=1
    g3: BSplineCurve PolesCount=3 KnotsCount=2 Degree=2 IsPeriodic=0
    g4: GeomPoint X=0 Y=0 Z=0
    g5: GeomPoint X=8 Y=6 Z=0
    g6: LineSegment StartX=0 StartY=6 StartZ=0 EndX=8 EndY=6 EndZ=0
  constraints (14):
    c: Coincident(g0,g-1)
    c: Distance(g0) = 6
    c: Vertical(g0)
    c: Coincident(g3,g0)
    c: Weight(g1) = 1
    c: Equal(g1,g2)
    c: InternalAlignment(g1,g3)
    c: InternalAlignment(g2,g3)
    c: InternalAlignment(g4,g3)
    c: InternalAlignment(g5,g3)
    c: Block(g3)
    c: Coincident(g6,g0)
    c: Coincident(g6,g3)
    c: Horizontal(g6)
FEATURE [Part::Extrusion] Extrude017  label="caseScrewPillarBracket005"
  Base = -> Sketch023
  Dir = (0,0,1)
  DirMode = 2
  FaceMakerClass = Part::FaceMakerBullseye
  LengthFwd = 2.4
  LengthRev = 0
  Placement = pos=(90.7,29,6.77) rot=(0,-1,0;1.5708rad)
  Solid = true
  Symmetric = false
FEATURE [Sketcher::SketchObject] Sketch024
  FullyConstrained = true
  sketch-geometry (7):
    g0: LineSegment StartX=0 StartY=0 StartZ=0 EndX=0 EndY=6 EndZ=0
    g1: Circle CenterX=0 CenterY=0 CenterZ=0 NormalX=0 NormalY=0 NormalZ=1 AngleXU=0 Radius=1
    g2: Circle CenterX=8 CenterY=6 CenterZ=0 NormalX=0 NormalY=0 NormalZ=1 AngleXU=0 Radius=1
    g3: BSplineCurve PolesCount=3 KnotsCount=2 Degree=2 IsPeriodic=0
    g4: GeomPoint X=0 Y=0 Z=0
    g5: GeomPoint X=8 Y=6 Z=0
    g6: LineSegment StartX=0 StartY=6 StartZ=0 EndX=8 EndY=6 EndZ=0
  constraints (14):
    c: Coincident(g0,g-1)
    c: Distance(g0) = 6
    c: Vertical(g0)
    c: Coincident(g3,g0)
    c: Weight(g1) = 1
    c: Equal(g1,g2)
    c: InternalAlignment(g1,g3)
    c: InternalAlignment(g2,g3)
    c: InternalAlignment(g4,g3)
    c: InternalAlignment(g5,g3)
    c: Block(g3)
    c: Coincident(g6,g0)
    c: Coincident(g6,g3)
    c: Horizontal(g6)
FEATURE [Part::Extrusion] Extrude018  label="caseScrewPillarBracket006"
  Base = -> Sketch024
  Dir = (0,0,1)
  DirMode = 2
  FaceMakerClass = Part::FaceMakerBullseye
  LengthFwd = 2.4
  LengthRev = 0
  Placement = pos=(103.7,29,6.77) rot=(0,-1,0;1.5708rad)
  Solid = true
  Symmetric = false
FEATURE [Sketcher::SketchObject] Sketch025
  FullyConstrained = true
  sketch-geometry (7):
    g0: LineSegment StartX=0 StartY=0 StartZ=0 EndX=0 EndY=6 EndZ=0
    g1: Circle CenterX=0 CenterY=0 CenterZ=0 NormalX=0 NormalY=0 NormalZ=1 AngleXU=0 Radius=1
    g2: Circle CenterX=8 CenterY=6 CenterZ=0 NormalX=0 NormalY=0 NormalZ=1 AngleXU=0 Radius=1
    g3: BSplineCurve PolesCount=3 KnotsCount=2 Degree=2 IsPeriodic=0
    g4: GeomPoint X=0 Y=0 Z=0
    g5: GeomPoint X=8 Y=6 Z=0
    g6: LineSegment StartX=0 StartY=6 StartZ=0 EndX=8 EndY=6 EndZ=0
  constraints (14):
    c: Coincident(g0,g-1)
    c: Distance(g0) = 6
    c: Vertical(g0)
    c: Coincident(g3,g0)
    c: Weight(g1) = 1
    c: Equal(g1,g2)
    c: InternalAlignment(g1,g3)
    c: InternalAlignment(g2,g3)
    c: InternalAlignment(g4,g3)
    c: InternalAlignment(g5,g3)
    c: Block(g3)
    c: Coincident(g6,g0)
    c: Coincident(g6,g3)
    c: Horizontal(g6)
FEATURE [Part::Extrusion] Extrude019  label="caseScrewPillarBracket007"
  Base = -> Sketch025
  Dir = (0,0,1)
  DirMode = 2
  FaceMakerClass = Part::FaceMakerBullseye
  LengthFwd = 2.4
  LengthRev = 0
  Placement = pos=(101.3,29,65.23) rot=(0,1,0;1.5708rad)
  Solid = true
  Symmetric = false
FEATURE [Part::Box] Box011  label="frontCaseScrewPillarBracket"
  AttacherType = Attacher::AttachEngine3D
  Height = 2.4
  Length = 16
  Placement = pos=(87,28,2.3) rot=(0,0,1;0rad)
  Width = 7
FEATURE [Part::Box] Box012  label="frontCaseScrewPillarBracket001"
  AttacherType = Attacher::AttachEngine3D
  Height = 2.4
  Length = 16
  Placement = pos=(87,28,67.3) rot=(0,0,1;0rad)
  Width = 7
FEATURE [Sketcher::SketchObject] Sketch026
  FullyConstrained = true
  sketch-geometry (17):
    g0: Circle CenterX=-3.5 CenterY=23.5 CenterZ=0 NormalX=0 NormalY=0 NormalZ=1 AngleXU=0 Radius=1
    g1: Circle CenterX=-1 CenterY=15.25 CenterZ=0 NormalX=0 NormalY=0 NormalZ=1 AngleXU=0 Radius=1
    g2: Circle CenterX=-3.5 CenterY=7 CenterZ=0 NormalX=0 NormalY=0 NormalZ=1 AngleXU=0 Radius=1
    g3: BSplineCurve PolesCount=3 KnotsCount=2 Degree=2 IsPeriodic=0
    g4: GeomPoint X=-3.5 Y=23.5 Z=0
    g5: GeomPoint X=-3.5 Y=7 Z=0
    g6: Circle CenterX=-4.8 CenterY=30.5 CenterZ=0 NormalX=0 NormalY=0 NormalZ=1 AngleXU=0 Radius=1
    g7: Circle CenterX=-3.5 CenterY=30.5 CenterZ=0 NormalX=0 NormalY=0 NormalZ=1 AngleXU=0 Radius=1
    g8: Circle CenterX=-3.5 CenterY=29.2 CenterZ=0 NormalX=0 NormalY=0 NormalZ=1 AngleXU=0 Radius=1
    g9: BSplineCurve PolesCount=3 KnotsCount=2 Degree=2 IsPeriodic=0
    g10: GeomPoint X=-4.8 Y=30.5 Z=0
    g11: GeomPoint X=-3.5 Y=29.2 Z=0
    g12: LineSegment StartX=-3.5 StartY=29.2 StartZ=0 EndX=-3.5 EndY=23.5 EndZ=0
    g13: LineSegment StartX=-4.8 StartY=30.5 StartZ=0 EndX=0 EndY=30.5 EndZ=0
    g14: LineSegment StartX=-3.5 StartY=5 StartZ=0 EndX=-3.5 EndY=7 EndZ=0
    g15: LineSegment StartX=0 StartY=5 StartZ=0 EndX=0 EndY=30.5 EndZ=0
    g16: LineSegment StartX=-3.5 StartY=5 StartZ=0 EndX=0 EndY=5 EndZ=0
  constraints (33):
    c: Weight(g0) = 1
    c: Equal(g0,g1)
    c: Equal(g0,g2)
    c: InternalAlignment(g0,g3)
    c: InternalAlignment(g1,g3)
    c: InternalAlignment(g2,g3)
    c: InternalAlignment(g4,g3)
    c: InternalAlignment(g5,g3)
    c: Block(g3)
    c: Weight(g6) = 1
    c: Equal(g6,g7)
    c: Equal(g6,g8)
    c: InternalAlignment(g6,g9)
    c: InternalAlignment(g7,g9)
    c: InternalAlignment(g8,g9)
    c: InternalAlignment(g10,g9)
    c: InternalAlignment(g11,g9)
    c: Block(g9)
    c: Coincident(g12,g9)
    c: Coincident(g12,g3)
    c: Vertical(g12)
    c: Coincident(g13,g9)
    c: Horizontal(g13)
    c: Distance(g13) = 4.8
    c: Coincident(g14,g3)
    c: Vertical(g14)
    c: Coincident(g15,g13)
    c: Vertical(g15)
    c: Tangent(g15,g1)
    c: Distance(g14) = 2
    c: Coincident(g16,g14)
    c: Horizontal(g16)
    c: Coincident(g15,g16)
FEATURE [Part::Feature] Face050
  shape: bbox 4.8 x 25.5 x 2e-07 mm, 1 faces, 0 solids (baked)
FEATURE [Part::Revolution] Revolve054  label="moreFrontCaseScrewPost001"
  Angle = 360
  Axis = (0,1,0)
  Base = (0,0,0)
  FaceMakerClass = Part::FaceMakerBullseye
  Placement = pos=(102.5,4.5,3.5) rot=(0,0,1;0rad)
  Solid = false
  Source = -> Face050
  Symmetric = false
FEATURE [Part::Feature] Face051
  shape: bbox 4.8 x 25.5 x 2e-07 mm, 1 faces, 0 solids (baked)
FEATURE [Part::Revolution] Revolve055  label="moreFrontCaseScrewPost002"
  Angle = 360
  Axis = (0,1,0)
  Base = (0,0,0)
  FaceMakerClass = Part::FaceMakerBullseye
  Placement = pos=(102.5,4.5,68.5) rot=(0,0,1;0rad)
  Solid = false
  Source = -> Face051
  Symmetric = false
FEATURE [Sketcher::SketchObject] Sketch027
  FullyConstrained = true
  sketch-geometry (10):
    g0: LineSegment StartX=-1.6 StartY=4.7 StartZ=0 EndX=-1.6 EndY=1.7 EndZ=0
    g1: LineSegment StartX=-3.5 StartY=4.7 StartZ=0 EndX=-1.6 EndY=4.7 EndZ=0
    g2: LineSegment StartX=-1.6 StartY=1.7 StartZ=0 EndX=-1.6 EndY=1.5 EndZ=0
    g3: LineSegment StartX=-1.6 StartY=1.5 StartZ=0 EndX=-5.2 EndY=1.5 EndZ=0
    g4: Circle CenterX=-3.5 CenterY=4.7 CenterZ=0 NormalX=0 NormalY=0 NormalZ=1 AngleXU=0 Radius=1
    g5: Circle CenterX=-3.59627 CenterY=2.99743 CenterZ=0 NormalX=0 NormalY=0 NormalZ=1 AngleXU=0 Radius=1
    g6: Circle CenterX=-5.2 CenterY=1.5 CenterZ=0 NormalX=0 NormalY=0 NormalZ=1 AngleXU=0 Radius=1
    g7: BSplineCurve PolesCount=3 KnotsCount=2 Degree=2 IsPeriodic=0
    g8: GeomPoint X=-3.5 Y=4.7 Z=0
    g9: GeomPoint X=-5.2 Y=1.5 Z=0
  constraints (23):
    c: Vertical(g0)
    c: Distance(g0) = 3
    c: Coincident(g1,g0)
    c: Horizontal(g1)
    c: Block(g0)
    c: Block(g1)
    c: Coincident(g2,g0)
    c: Vertical(g2)
    c: Distance(g2) = 0.2
    c: Coincident(g3,g2)
    c: Horizontal(g3)
    c: Block(g3)
    c: Coincident(g7,g1)
    c: Weight(g4) = 1
    c: Equal(g4,g5)
    c: Equal(g4,g6)
    c: Coincident(g7,g3)
    c: InternalAlignment(g4,g7)
    c: InternalAlignment(g5,g7)
    c: InternalAlignment(g6,g7)
    c: InternalAlignment(g8,g7)
    c: InternalAlignment(g9,g7)
    c: Block(g7)
FEATURE [Sketcher::SketchObject] Sketch028
  FullyConstrained = true
  sketch-geometry (18):
    g0: LineSegment StartX=0 StartY=3e-16 StartZ=0 EndX=0 EndY=1.7 EndZ=0
    g1: LineSegment StartX=-3.5 StartY=0 StartZ=0 EndX=-3.5 EndY=0.9 EndZ=0
    g2: Circle CenterX=-2.7 CenterY=1.7 CenterZ=0 NormalX=0 NormalY=0 NormalZ=1 AngleXU=0 Radius=1
    g3: Circle CenterX=-3.5 CenterY=1.7 CenterZ=0 NormalX=0 NormalY=0 NormalZ=1 AngleXU=0 Radius=1
    g4: Circle CenterX=-3.5 CenterY=0.9 CenterZ=0 NormalX=0 NormalY=0 NormalZ=1 AngleXU=0 Radius=1
    g5: BSplineCurve PolesCount=3 KnotsCount=2 Degree=2 IsPeriodic=0
    g6: GeomPoint X=-2.7 Y=1.7 Z=0
    g7: GeomPoint X=-3.5 Y=0.9 Z=0
    g8: LineSegment StartX=-3.5 StartY=0 StartZ=0 EndX=-3.5 EndY=-7 EndZ=0
    g9: LineSegment StartX=0 StartY=3e-16 StartZ=0 EndX=0 EndY=-7 EndZ=0
    g10: LineSegment StartX=-3.5 StartY=-7 StartZ=0 EndX=0 EndY=-7 EndZ=0
    g11: LineSegment StartX=-2.7 StartY=1.7 StartZ=0 EndX=-1.6 EndY=1.7 EndZ=0
    g12: LineSegment StartX=0 StartY=1.7 StartZ=0 EndX=0 EndY=4.5 EndZ=0
    g13: LineSegment StartX=0 StartY=4.5 StartZ=0 EndX=0 EndY=10.8 EndZ=0
    g14: LineSegment StartX=0 StartY=10.8 StartZ=0 EndX=-2 EndY=10.8 EndZ=0
    g15: LineSegment StartX=-1.6 StartY=4.7 StartZ=0 EndX=-1.6 EndY=1.7 EndZ=0
    g16: LineSegment StartX=-1.6 StartY=4.7 StartZ=0 EndX=-2 EndY=4.7 EndZ=0
    g17: LineSegment StartX=-2 StartY=4.7 StartZ=0 EndX=-2 EndY=10.8 EndZ=0
  constraints (44):
    c: Vertical(g0)
    c: Vertical(g1)
    c: Distance(g1) = 0.9
    c: Block(g0)
    c: Distance(g0) = 1.7
    c: Weight(g2) = 1
    c: Equal(g2,g3)
    c: Equal(g2,g4)
    c: Coincident(g5,g1)
    c: InternalAlignment(g2,g5)
    c: InternalAlignment(g3,g5)
    c: InternalAlignment(g4,g5)
    c: InternalAlignment(g6,g5)
    c: InternalAlignment(g7,g5)
    c: Block(g5)
    c: Coincident(g8,g1)
    c: Vertical(g8)
    c: Distance(g8) = 7
    c: Vertical(g9)
    c: Equal(g8,g9) = 7
    c: Coincident(g9,g0)
    c: Coincident(g10,g8)
    c: Coincident(g10,g9)
    c: Horizontal(g10)
    c: Coincident(g11,g5)
    c: Horizontal(g11)
    c: Coincident(g12,g0)
    c: Vertical(g12)
    c: Distance(g12) = 2.8
    c: Coincident(g13,g12)
    c: Vertical(g13)
    c: Distance(g13) = 6.3
    c: Coincident(g14,g13)
    c: Horizontal(g14)
    c: Distance(g14) = 2
    c: Vertical(g15)
    c: Distance(g15) = 3
    c: Block(g11)
    c: Coincident(g15,g11)
    c: Coincident(g16,g15)
    c: Horizontal(g16)
    c: Coincident(g17,g16)
    c: Coincident(g17,g14)
    c: Vertical(g17)
FEATURE [Part::Revolution] Revolve040  label="backCaseScrewRetainer001"
  Angle = 360
  Axis = (0,1,0)
  Base = (0,0,0)
  FaceMakerClass = Part::FaceMakerBullseye
  Placement = pos=(12.5,3,10) rot=(0,0,1;0rad)
  Solid = false
  Source = -> Face036
  Symmetric = false
FEATURE [Part::Feature] Face055
  shape: bbox 3.5 x 30.2 x 2e-07 mm, 1 faces, 0 solids (baked)
FEATURE [Part::Revolution] Revolve059  label="backCaseScrewPost"
  Angle = 360
  Axis = (0,1,0)
  Base = (0,0,0)
  FaceMakerClass = Part::FaceMakerBullseye
  Placement = pos=(12.5,4.5,10) rot=(0,0,1;0rad)
  Solid = false
  Source = -> Face055
  Symmetric = false
FEATURE [Part::Feature] Face056
  shape: bbox 3.5 x 30.2 x 2e-07 mm, 1 faces, 0 solids (baked)
FEATURE [Part::Revolution] Revolve060  label="backCaseScrewPost001"
  Angle = 360
  Axis = (0,1,0)
  Base = (0,0,0)
  FaceMakerClass = Part::FaceMakerBullseye
  Placement = pos=(12.5,4.5,62) rot=(0,0,1;0rad)
  Solid = false
  Source = -> Face056
  Symmetric = false
FEATURE [Part::Feature] Face057
  shape: bbox 3.5 x 17.8 x 2e-07 mm, 1 faces, 0 solids (baked)
FEATURE [Part::Revolution] Revolve061  label="removeToCreateScrewAndThreadedInsertHole"
  Angle = 360
  Axis = (0,1,0)
  Base = (0,0,0)
  FaceMakerClass = Part::FaceMakerBullseye
  Placement = pos=(12.5,0,10) rot=(0,0,1;0rad)
  Solid = false
  Source = -> Face057
  Symmetric = false
FEATURE [Part::Feature] Face058
  shape: bbox 3.5 x 17.8 x 2e-07 mm, 1 faces, 0 solids (baked)
FEATURE [Part::Revolution] Revolve062  label="removeToCreateScrewAndThreadedInsertHole001"
  Angle = 360
  Axis = (0,1,0)
  Base = (0,0,0)
  FaceMakerClass = Part::FaceMakerBullseye
  Placement = pos=(12.5,0,62) rot=(0,0,1;0rad)
  Solid = false
  Source = -> Face058
  Symmetric = false
FEATURE [Part::Feature] Face059
  shape: bbox 3.5 x 17.8 x 2e-07 mm, 1 faces, 0 solids (baked)
FEATURE [Part::Revolution] Revolve063  label="removeToCreateScrewAndThreadedInsertHole002"
  Angle = 360
  Axis = (0,1,0)
  Base = (0,0,0)
  FaceMakerClass = Part::FaceMakerBullseye
  Placement = pos=(89.5,0,68.5) rot=(0,0,1;0rad)
  Solid = false
  Source = -> Face059
  Symmetric = false
FEATURE [Part::Feature] Face060
  shape: bbox 3.5 x 17.8 x 2e-07 mm, 1 faces, 0 solids (baked)
FEATURE [Part::Revolution] Revolve064  label="removeToCreateScrewAndThreadedInsertHole003"
  Angle = 360
  Axis = (0,1,0)
  Base = (0,0,0)
  FaceMakerClass = Part::FaceMakerBullseye
  Placement = pos=(89.5,0,3.5) rot=(0,0,1;0rad)
  Solid = false
  Source = -> Face060
  Symmetric = false
FEATURE [Part::Feature] Face061
  shape: bbox 3.5 x 17.8 x 2e-07 mm, 1 faces, 0 solids (baked)
FEATURE [Part::Revolution] Revolve065  label="removeToCreateScrewAndThreadedInsertHole004"
  Angle = 360
  Axis = (0,1,0)
  Base = (0,0,0)
  FaceMakerClass = Part::FaceMakerBullseye
  Placement = pos=(102.5,4.7,3.5) rot=(0,0,1;0rad)
  Solid = false
  Source = -> Face061
  Symmetric = false
FEATURE [Part::Feature] Face062
  shape: bbox 3.5 x 17.8 x 2e-07 mm, 1 faces, 0 solids (baked)
FEATURE [Part::Revolution] Revolve066  label="removeToCreateScrewAndThreadedInsertHole005"
  Angle = 360
  Axis = (0,1,0)
  Base = (0,0,0)
  FaceMakerClass = Part::FaceMakerBullseye
  Placement = pos=(102.5,4.7,68.5) rot=(0,0,1;0rad)
  Solid = false
  Source = -> Face062
  Symmetric = false
FEATURE [Part::MultiFuse] Fusion047  label="makeHoles"
  Shapes = -> [Revolve066,Revolve065,Revolve064,Revolve063,Revolve062,Revolve061]
FEATURE [Part::Feature] Face063
  shape: bbox 3.6 x 3.2 x 2e-07 mm, 1 faces, 0 solids (baked)
FEATURE [Part::Revolution] Revolve067  label="moreFrontCaseScrewRetainer002"
  Angle = 360
  Axis = (0,1,0)
  Base = (0,0,0)
  FaceMakerClass = Part::FaceMakerBullseye
  Placement = pos=(102.5,4.5,68.5) rot=(0,0,1;0rad)
  Solid = false
  Source = -> Face063
  Symmetric = false
FEATURE [Part::Feature] Face064
  shape: bbox 3.6 x 3.2 x 2e-07 mm, 1 faces, 0 solids (baked)
FEATURE [Part::Revolution] Revolve068  label="moreFrontCaseScrewRetainer003"
  Angle = 360
  Axis = (0,1,0)
  Base = (0,0,0)
  FaceMakerClass = Part::FaceMakerBullseye
  Placement = pos=(102.5,4.5,3.5) rot=(0,0,1;0rad)
  Solid = false
  Source = -> Face064
  Symmetric = false
FEATURE [Part::Feature] Face065
  shape: bbox 3.5 x 17.8 x 2e-07 mm, 1 faces, 0 solids (baked)
FEATURE [Part::Revolution] Revolve069  label="removeToCreateScrewAndThreadedInsertHole006"
  Angle = 360
  Axis = (0,1,0)
  Base = (0,0,0)
  FaceMakerClass = Part::FaceMakerBullseye
  Placement = pos=(12.5,0,10) rot=(0,0,1;0rad)
  Solid = false
  Source = -> Face065
  Symmetric = false
FEATURE [Part::Feature] Face066
  shape: bbox 3.5 x 17.8 x 2e-07 mm, 1 faces, 0 solids (baked)
FEATURE [Part::Revolution] Revolve070  label="removeToCreateScrewAndThreadedInsertHole007"
  Angle = 360
  Axis = (0,1,0)
  Base = (0,0,0)
  FaceMakerClass = Part::FaceMakerBullseye
  Placement = pos=(12.5,0,62) rot=(0,0,1;0rad)
  Solid = false
  Source = -> Face066
  Symmetric = false
FEATURE [Part::Feature] Face067
  shape: bbox 3.5 x 17.8 x 2e-07 mm, 1 faces, 0 solids (baked)
FEATURE [Part::Revolution] Revolve071  label="removeToCreateScrewAndThreadedInsertHole008"
  Angle = 360
  Axis = (0,1,0)
  Base = (0,0,0)
  FaceMakerClass = Part::FaceMakerBullseye
  Placement = pos=(89.5,0,68.5) rot=(0,0,1;0rad)
  Solid = false
  Source = -> Face067
  Symmetric = false
FEATURE [Part::Feature] Face068
  shape: bbox 3.5 x 17.8 x 2e-07 mm, 1 faces, 0 solids (baked)
FEATURE [Part::Revolution] Revolve072  label="removeToCreateScrewAndThreadedInsertHole009"
  Angle = 360
  Axis = (0,1,0)
  Base = (0,0,0)
  FaceMakerClass = Part::FaceMakerBullseye
  Placement = pos=(89.5,0,3.5) rot=(0,0,1;0rad)
  Solid = false
  Source = -> Face068
  Symmetric = false
FEATURE [Part::Feature] Face069
  shape: bbox 3.5 x 17.8 x 2e-07 mm, 1 faces, 0 solids (baked)
FEATURE [Part::Feature] Face070
  shape: bbox 3.5 x 17.8 x 2e-07 mm, 1 faces, 0 solids (baked)
FEATURE [Part::Revolution] Revolve073  label="removeToCreateScrewAndThreadedInsertHole010"
  Angle = 360
  Axis = (0,1,0)
  Base = (0,0,0)
  FaceMakerClass = Part::FaceMakerBullseye
  Placement = pos=(102.5,4.7,3.5) rot=(0,0,1;0rad)
  Solid = false
  Source = -> Face069
  Symmetric = false
FEATURE [Part::Revolution] Revolve074  label="removeToCreateScrewAndThreadedInsertHole011"
  Angle = 360
  Axis = (0,1,0)
  Base = (0,0,0)
  FaceMakerClass = Part::FaceMakerBullseye
  Placement = pos=(102.5,4.7,68.5) rot=(0,0,1;0rad)
  Solid = false
  Source = -> Face070
  Symmetric = false
FEATURE [Part::MultiFuse] Fusion048  label="makeHoles001"
  Shapes = -> [Revolve074,Revolve073,Revolve072,Revolve071,Revolve070,Revolve069]
FEATURE [Part::MultiFuse] Fusion049  label="caseScrewRetainers"
  Shapes = -> [Revolve067,Revolve068,Revolve048,Revolve047,Revolve039,Revolve040]
FEATURE [Part::Cut] Cut015  label="caseScrewRetainers001"
  Base = -> Fusion049
  Tool = -> Fusion048
FEATURE [Part::MultiFuse] Fusion050  label="casePillars"
  Shapes = -> [Revolve055,Revolve054,Revolve043,Revolve046,Revolve059,Revolve060]
FEATURE [Part::Feature] Face071 .. Face076  x6 (patterned run collapsed; names and placements below)
  shape: bbox 3.5 x 17.8 x 2e-07 mm, 1 faces, 0 solids (baked)
FEATURE [Part::Revolution] Revolve075  label="removeToCreateScrewAndThreadedInsertHole012"
  Angle = 360
  Axis = (0,1,0)
  Base = (0,0,0)
  FaceMakerClass = Part::FaceMakerBullseye
  Placement = pos=(12.5,0,10) rot=(0,0,1;0rad)
  Solid = false
  Source = -> Face071
  Symmetric = false
FEATURE [Part::Revolution] Revolve076  label="removeToCreateScrewAndThreadedInsertHole013"
  Angle = 360
  Axis = (0,1,0)
  Base = (0,0,0)
  FaceMakerClass = Part::FaceMakerBullseye
  Placement = pos=(12.5,0,62) rot=(0,0,1;0rad)
  Solid = false
  Source = -> Face072
  Symmetric = false
FEATURE [Part::Revolution] Revolve077  label="removeToCreateScrewAndThreadedInsertHole014"
  Angle = 360
  Axis = (0,1,0)
  Base = (0,0,0)
  FaceMakerClass = Part::FaceMakerBullseye
  Placement = pos=(89.5,0,68.5) rot=(0,0,1;0rad)
  Solid = false
  Source = -> Face073
  Symmetric = false
FEATURE [Part::Revolution] Revolve078  label="removeToCreateScrewAndThreadedInsertHole015"
  Angle = 360
  Axis = (0,1,0)
  Base = (0,0,0)
  FaceMakerClass = Part::FaceMakerBullseye
  Placement = pos=(89.5,0,3.5) rot=(0,0,1;0rad)
  Solid = false
  Source = -> Face074
  Symmetric = false
FEATURE [Part::Revolution] Revolve079  label="removeToCreateScrewAndThreadedInsertHole016"
  Angle = 360
  Axis = (0,1,0)
  Base = (0,0,0)
  FaceMakerClass = Part::FaceMakerBullseye
  Placement = pos=(102.5,4.7,3.5) rot=(0,0,1;0rad)
  Solid = false
  Source = -> Face075
  Symmetric = false
FEATURE [Part::Revolution] Revolve080  label="removeToCreateScrewAndThreadedInsertHole017"
  Angle = 360
  Axis = (0,1,0)
  Base = (0,0,0)
  FaceMakerClass = Part::FaceMakerBullseye
  Placement = pos=(102.5,4.7,68.5) rot=(0,0,1;0rad)
  Solid = false
  Source = -> Face076
  Symmetric = false
FEATURE [Part::MultiFuse] Fusion051  label="makeHoles002"
  Shapes = -> [Revolve080,Revolve079,Revolve078,Revolve077,Revolve076,Revolve075]
FEATURE [Part::Cut] Cut016  label="caesPillars"
  Base = -> Fusion050
  Tool = -> Fusion051
FEATURE [Part::Revolution] Revolve009  label="plugHousing016"
  Angle = 360
  Axis = (0,1,0)
  Base = (0,0,0)
  FaceMakerClass = Part::FaceMakerBullseye
  Placement = pos=(0,0,36.15) rot=(0,0,1;0rad)
  Solid = false
  Source = -> Face012
  Symmetric = false
FEATURE [Part::MultiFuse] Fusion014  label="plugHousing023"
  Placement = pos=(0,0,0) rot=(0,0,1;1.5708rad)
  Shapes = -> [Revolve011,Revolve009]
FEATURE [Part::Revolution] Revolve010  label="plugHousing017"
  Angle = 360
  Axis = (0,1,0)
  Base = (0,0,0)
  FaceMakerClass = Part::FaceMakerBullseye
  Placement = pos=(0,0,36.15) rot=(0,0,1;0rad)
  Solid = false
  Source = -> Face014
  Symmetric = false
FEATURE [Part::MultiFuse] Fusion015  label="plugHousing024"
  Placement = pos=(0,0,0) rot=(0,0,1;1.5708rad)
  Shapes = -> [Revolve010,Revolve015]
FEATURE [Part::Revolution] Revolve014  label="plugHousing026"
  Angle = 360
  Axis = (0,1,0)
  Base = (0,0,0)
  FaceMakerClass = Part::FaceMakerBullseye
  Placement = pos=(0,0,36.15) rot=(0,0,1;0rad)
  Solid = false
  Source = -> Face011
  Symmetric = false
FEATURE [Part::Revolution] Revolve013  label="plugHousing025"
  Angle = 360
  Axis = (0,1,0)
  Base = (0,0,0)
  FaceMakerClass = Part::FaceMakerBullseye
  Placement = pos=(0,0,36.15) rot=(0,0,1;0rad)
  Solid = false
  Source = -> Face015
  Symmetric = false
FEATURE [Part::MultiFuse] Fusion016  label="plugHousing028"
  Placement = pos=(0,19,0) rot=(0,0,1;3.14159rad)
  Shapes = -> [Fusion014,Fusion013]
FEATURE [Part::MultiFuse] Fusion011  label="plugHousing018"
  Placement = pos=(0,0,0) rot=(0,0,1;1.5708rad)
  Shapes = -> [Revolve014,Revolve013]
FEATURE [Part::MultiFuse] Fusion012  label="plugHousing019"
  Placement = pos=(0,19,0) rot=(0,0,1;3.14159rad)
  Shapes = -> [Fusion011,Fusion015]
FEATURE [Part::MultiFuse] Fusion017  label="plugHousing029"
  Placement = pos=(122.621,0,-0.15) rot=(0,0,1;0rad)
  Shapes = -> [Fusion016,Fusion012]
FEATURE [Part::MultiFuse] Fusion052  label="casePillarRetainers"
  Shapes = -> [Extrude012,Extrude013,Extrude014,Extrude015,Extrude016,Extrude017,Extrude018,Extrude019,Box011,Box012]
FEATURE [Part::Feature] Face077
  shape: bbox 3.5 x 17.8 x 2e-07 mm, 1 faces, 0 solids (baked)
FEATURE [Part::Revolution] Revolve081  label="removeToCreateScrewAndThreadedInsertHole018"
  Angle = 360
  Axis = (0,1,0)
  Base = (0,0,0)
  FaceMakerClass = Part::FaceMakerBullseye
  Placement = pos=(62.3,30.3,19.7) rot=(0,0,1;0rad)
  Solid = false
  Source = -> Face077
  Symmetric = false
FEATURE [Part::Feature] Face078
  shape: bbox 3.5 x 17.8 x 2e-07 mm, 1 faces, 0 solids (baked)
FEATURE [Part::Revolution] Revolve082  label="removeToCreateScrewAndThreadedInsertHole019"
  Angle = 360
  Axis = (0,1,0)
  Base = (0,0,0)
  FaceMakerClass = Part::FaceMakerBullseye
  Placement = pos=(62.3,30.3,51.7) rot=(0,0,1;0rad)
  Solid = false
  Source = -> Face078
  Symmetric = false
FEATURE [Part::Feature] Face079
  shape: bbox 3.5 x 17.8 x 2e-07 mm, 1 faces, 0 solids (baked)
FEATURE [Part::Revolution] Revolve083  label="removeToCreateScrewAndThreadedInsertHole020"
  Angle = 360
  Axis = (0,1,0)
  Base = (0,0,0)
  FaceMakerClass = Part::FaceMakerBullseye
  Placement = pos=(30.3,30.3,19.7) rot=(0,0,1;0rad)
  Solid = false
  Source = -> Face079
  Symmetric = false
FEATURE [Part::Feature] Face080
  shape: bbox 3.5 x 17.8 x 2e-07 mm, 1 faces, 0 solids (baked)
FEATURE [Part::Revolution] Revolve084  label="removeToCreateScrewAndThreadedInsertHole021"
  Angle = 360
  Axis = (0,1,0)
  Base = (0,0,0)
  FaceMakerClass = Part::FaceMakerBullseye
  Placement = pos=(30.3,30.3,51.7) rot=(0,0,1;0rad)
  Solid = false
  Source = -> Face080
  Symmetric = false
FEATURE [Part::MultiFuse] Fusion053  label="createThreadedInsertHolesForFan"
  Shapes = -> [Revolve081,Revolve082,Revolve083,Revolve084]
FEATURE [Part::Cut] Cut017  label="fanScrewHousing001"
  Base = -> Fusion046
  Tool = -> Fusion053
FEATURE [Part::Feature] Face081
  shape: bbox 3.5 x 17.8 x 2e-07 mm, 1 faces, 0 solids (baked)
FEATURE [Part::Revolution] Revolve085  label="removeToCreateScrewAndThreadedInsertHole022"
  Angle = 360
  Axis = (0,1,0)
  Base = (0,0,0)
  FaceMakerClass = Part::FaceMakerBullseye
  Placement = pos=(62.3,30.3,19.7) rot=(0,0,1;0rad)
  Solid = false
  Source = -> Face081
  Symmetric = false
FEATURE [Part::Feature] Face082
  shape: bbox 3.5 x 17.8 x 2e-07 mm, 1 faces, 0 solids (baked)
FEATURE [Part::Revolution] Revolve086  label="removeToCreateScrewAndThreadedInsertHole023"
  Angle = 360
  Axis = (0,1,0)
  Base = (0,0,0)
  FaceMakerClass = Part::FaceMakerBullseye
  Placement = pos=(62.3,30.3,51.7) rot=(0,0,1;0rad)
  Solid = false
  Source = -> Face082
  Symmetric = false
FEATURE [Part::Feature] Face083
  shape: bbox 3.5 x 17.8 x 2e-07 mm, 1 faces, 0 solids (baked)
FEATURE [Part::Revolution] Revolve087  label="removeToCreateScrewAndThreadedInsertHole024"
  Angle = 360
  Axis = (0,1,0)
  Base = (0,0,0)
  FaceMakerClass = Part::FaceMakerBullseye
  Placement = pos=(30.3,30.3,19.7) rot=(0,0,1;0rad)
  Solid = false
  Source = -> Face083
  Symmetric = false
FEATURE [Part::Feature] Face084
  shape: bbox 3.5 x 17.8 x 2e-07 mm, 1 faces, 0 solids (baked)
FEATURE [Part::Revolution] Revolve088  label="removeToCreateScrewAndThreadedInsertHole025"
  Angle = 360
  Axis = (0,1,0)
  Base = (0,0,0)
  FaceMakerClass = Part::FaceMakerBullseye
  Placement = pos=(30.3,30.3,51.7) rot=(0,0,1;0rad)
  Solid = false
  Source = -> Face084
  Symmetric = false
FEATURE [Part::MultiFuse] Fusion054  label="createThreadedInsertHolesForFan001"
  Shapes = -> [Revolve085,Revolve086,Revolve087,Revolve088]
FEATURE [Part::Cut] Cut018  label="top007"
  Base = -> Fusion040
  Tool = -> Fusion054
FEATURE [Sketcher::SketchObject] Sketch029
  FullyConstrained = false
  Placement = pos=(0,0,0) rot=(1,0,0;1.5708rad)
  sketch-geometry (24):
    g0: ArcOfCircle CenterX=-4 CenterY=-10.5 CenterZ=0 NormalX=0 NormalY=0 NormalZ=1 AngleXU=0 Radius=1.5 StartAngle=6e-16 EndAngle=3.14159
    g1: ArcOfCircle CenterX=-34.2 CenterY=-10.5 CenterZ=0 NormalX=0 NormalY=0 NormalZ=1 AngleXU=0 Radius=1.5 StartAngle=0 EndAngle=3.14159
    g2: ArcOfCircle CenterX=-34.2 CenterY=-27.7 CenterZ=0 NormalX=0 NormalY=0 NormalZ=1 AngleXU=0 Radius=1.5 StartAngle=3.14159 EndAngle=6.28319
    g3: ArcOfCircle CenterX=-4 CenterY=-27.7 CenterZ=0 NormalX=0 NormalY=0 NormalZ=1 AngleXU=0 Radius=1.5 StartAngle=3.1416 EndAngle=6.28319
    g4: ArcOfCircle CenterX=-10 CenterY=-4.3 CenterZ=0 NormalX=0 NormalY=0 NormalZ=1 AngleXU=0 Radius=1.5 StartAngle=2e-16 EndAngle=3.14159
    g5: ArcOfCircle CenterX=-16.1 CenterY=-1.8 CenterZ=0 NormalX=0 NormalY=0 NormalZ=1 AngleXU=0 Radius=1.5 StartAngle=5e-16 EndAngle=3.14159
    g6: ArcOfCircle CenterX=-22.1 CenterY=-1.8 CenterZ=0 NormalX=0 NormalY=0 NormalZ=1 AngleXU=0 Radius=1.5 StartAngle=5e-16 EndAngle=3.14159
    g7: ArcOfCircle CenterX=-28.2 CenterY=-4.3 CenterZ=0 NormalX=0 NormalY=0 NormalZ=1 AngleXU=0 Radius=1.5 StartAngle=2e-16 EndAngle=3.14159
    g8: ArcOfCircle CenterX=-10 CenterY=-33.9 CenterZ=0 NormalX=0 NormalY=0 NormalZ=1 AngleXU=0 Radius=1.5 StartAngle=3.14159 EndAngle=6.28319
    g9: ArcOfCircle CenterX=-16.1 CenterY=-36.4 CenterZ=0 NormalX=0 NormalY=0 NormalZ=1 AngleXU=0 Radius=1.5 StartAngle=3.14159 EndAngle=6.28319
    g10: ArcOfCircle CenterX=-22.1 CenterY=-36.4 CenterZ=0 NormalX=0 NormalY=0 NormalZ=1 AngleXU=0 Radius=1.5 StartAngle=3.14159 EndAngle=6.28319
    g11: ArcOfCircle CenterX=-28.2 CenterY=-33.9 CenterZ=0 NormalX=0 NormalY=0 NormalZ=1 AngleXU=0 Radius=1.5 StartAngle=3.14159 EndAngle=6.28319
    g12: LineSegment StartX=-35.7 StartY=-10.5 StartZ=0 EndX=-35.7 EndY=-27.7 EndZ=0
    g13: LineSegment StartX=-32.7 StartY=-10.5 StartZ=0 EndX=-32.7 EndY=-27.7 EndZ=0
    g14: LineSegment StartX=-29.7 StartY=-33.9 StartZ=0 EndX=-29.7 EndY=-4.3 EndZ=0
    g15: LineSegment StartX=-26.7 StartY=-33.9 StartZ=0 EndX=-26.7 EndY=-4.3 EndZ=0
    g16: LineSegment StartX=-2.5 StartY=-10.5 StartZ=0 EndX=-2.5 EndY=-27.7 EndZ=0
    g17: LineSegment StartX=-8.5 StartY=-4.3 StartZ=0 EndX=-8.5 EndY=-33.9 EndZ=0
    g18: LineSegment StartX=-5.5 StartY=-10.5 StartZ=0 EndX=-5.5 EndY=-27.7 EndZ=0
    g19: LineSegment StartX=-11.5 StartY=-4.3 StartZ=0 EndX=-11.5 EndY=-33.9 EndZ=0
    g20: LineSegment StartX=-14.6 StartY=-1.8 StartZ=0 EndX=-14.6 EndY=-36.4 EndZ=0
    g21: LineSegment StartX=-17.6 StartY=-1.8 StartZ=0 EndX=-17.6 EndY=-36.4 EndZ=0
    g22: LineSegment StartX=-20.6 StartY=-36.4 StartZ=0 EndX=-20.6 EndY=-1.8 EndZ=0
    g23: LineSegment StartX=-23.6 StartY=-1.8 StartZ=0 EndX=-23.6 EndY=-36.4 EndZ=0
  constraints (48):
    c: Block(g0)
    c: Block(g1)
    c: Block(g2)
    c: Block(g3)
    c: Block(g4)
    c: Block(g5)
    c: Block(g6)
    c: Block(g7)
    c: Block(g8)
    c: Block(g9)
    c: Block(g10)
    c: Block(g11)
    c: Coincident(g12,g1)
    c: Coincident(g12,g2)
    c: Vertical(g12)
    c: Coincident(g13,g1)
    c: Coincident(g13,g2)
    c: Vertical(g13)
    c: Coincident(g14,g11)
    c: Coincident(g14,g7)
    c: Vertical(g14)
    c: Coincident(g15,g11)
    c: Coincident(g15,g7)
    c: Vertical(g15)
    c: Coincident(g16,g0)
    c: Coincident(g16,g3)
    c: Vertical(g16)
    c: Coincident(g17,g4)
    c: Coincident(g17,g8)
    c: Vertical(g17)
    c: Coincident(g18,g0)
    c: Coincident(g18,g3)
    c: Vertical(g18)
    c: Coincident(g19,g4)
    c: Coincident(g19,g8)
    c: Vertical(g19)
    c: Coincident(g20,g5)
    c: Coincident(g20,g9)
    c: Vertical(g20)
    c: Coincident(g21,g5)
    c: Coincident(g21,g9)
    c: Vertical(g21)
    c: Coincident(g22,g10)
    c: Coincident(g22,g6)
    c: Vertical(g22)
    c: Coincident(g23,g6)
    c: Coincident(g23,g10)
    c: Vertical(g23)
FEATURE [Part::Extrusion] Extrude020  label="removeToCreateFanGrillHoles"
  Base = -> Sketch029
  Dir = (0,-1,6e-16)
  DirMode = 2
  FaceMakerClass = Part::FaceMakerBullseye
  LengthFwd = 10
  LengthRev = 0
  Placement = pos=(65.4,44,54.82) rot=(0,0,1;0rad)
  Solid = true
  Symmetric = false
FEATURE [Part::MultiFuse] Fusion055  label="top008"
  Shapes = -> [Cut017,Cut018]
FEATURE [Part::Cut] Cut019  label="top009"
  Base = -> Fusion055
  Tool = -> Extrude020
FEATURE [App::MeasureDistance] Distance003  label="Distance: 71.95 mm"
  Distance = 71.9513
  P1 = (117,38,72)
  P2 = (117,38,0.0487319)
FEATURE [Sketcher::SketchObject] Sketch030
  FullyConstrained = true
  Placement = pos=(117,19,0) rot=(0.57735,0.57735,0.57735;2.0944rad)
  sketch-geometry (48):
    g0: LineSegment StartX=-49.19 StartY=69.25 StartZ=0 EndX=-49.19 EndY=66.25 EndZ=0
    g1: LineSegment StartX=-49.19 StartY=63.5 StartZ=0 EndX=-49.19 EndY=60.5 EndZ=0
    g2: LineSegment StartX=-49.19 StartY=57.75 StartZ=0 EndX=-49.19 EndY=54.75 EndZ=0
    g3: LineSegment StartX=-49.19 StartY=52 StartZ=0 EndX=-49.19 EndY=49 EndZ=0
    g4: LineSegment StartX=-49.19 StartY=46.25 StartZ=0 EndX=-49.19 EndY=43.25 EndZ=0
    g5: LineSegment StartX=-49.19 StartY=40.5 StartZ=0 EndX=-49.19 EndY=37.5 EndZ=0
    g6: LineSegment StartX=-49.19 StartY=34.5 StartZ=0 EndX=-49.19 EndY=31.5 EndZ=0
    g7: LineSegment StartX=-49.19 StartY=28.75 StartZ=0 EndX=-49.19 EndY=25.75 EndZ=0
    g8: LineSegment StartX=-49.19 StartY=23 StartZ=0 EndX=-49.19 EndY=20 EndZ=0
    g9: LineSegment StartX=-49.19 StartY=17.25 StartZ=0 EndX=-49.19 EndY=14.25 EndZ=0
    g10: LineSegment StartX=-49.19 StartY=11.5 StartZ=0 EndX=-49.19 EndY=8.5 EndZ=0
    g11: LineSegment StartX=-49.19 StartY=5.75 StartZ=0 EndX=-49.19 EndY=2.75 EndZ=0
    g12: ArcOfCircle CenterX=-1.5 CenterY=67.75 CenterZ=0 NormalX=0 NormalY=0 NormalZ=1 AngleXU=0 Radius=1.5 StartAngle=4.71239 EndAngle=7.85398
    g13: ArcOfCircle CenterX=-1.5 CenterY=62 CenterZ=0 NormalX=0 NormalY=0 NormalZ=1 AngleXU=0 Radius=1.5 StartAngle=4.71239 EndAngle=7.85398
    g14: ArcOfCircle CenterX=-1.5 CenterY=56.25 CenterZ=0 NormalX=0 NormalY=0 NormalZ=1 AngleXU=0 Radius=1.5 StartAngle=4.71239 EndAngle=7.85398
    g15: ArcOfCircle CenterX=-11.49 CenterY=50.5 CenterZ=0 NormalX=0 NormalY=0 NormalZ=1 AngleXU=0 Radius=1.5 StartAngle=4.71239 EndAngle=7.85398
    g16: ArcOfCircle CenterX=-16.28 CenterY=44.75 CenterZ=0 NormalX=0 NormalY=0 NormalZ=1 AngleXU=0 Radius=1.5 StartAngle=4.71239 EndAngle=7.85398
    g17: ArcOfCircle CenterX=-18.2337 CenterY=39 CenterZ=0 NormalX=0 NormalY=0 NormalZ=1 AngleXU=0 Radius=1.5 StartAngle=4.71485 EndAngle=7.85398
    g18: ArcOfCircle CenterX=-16.2837 CenterY=27.25 CenterZ=0 NormalX=0 NormalY=0 NormalZ=1 AngleXU=0 Radius=1.5 StartAngle=4.71485 EndAngle=7.85398
    g19: ArcOfCircle CenterX=-18.2337 CenterY=33 CenterZ=0 NormalX=0 NormalY=0 NormalZ=1 AngleXU=0 Radius=1.5 StartAngle=4.71485 EndAngle=7.85398
    g20: ArcOfCircle CenterX=-11.49 CenterY=21.5 CenterZ=0 NormalX=0 NormalY=0 NormalZ=1 AngleXU=0 Radius=1.5 StartAngle=4.71239 EndAngle=7.85398
    g21: ArcOfCircle CenterX=-1.5 CenterY=4.25 CenterZ=0 NormalX=0 NormalY=0 NormalZ=1 AngleXU=0 Radius=1.5 StartAngle=4.71239 EndAngle=7.85398
    g22: ArcOfCircle CenterX=-1.5 CenterY=10 CenterZ=0 NormalX=0 NormalY=0 NormalZ=1 AngleXU=0 Radius=1.5 StartAngle=4.71239 EndAngle=7.85398
    g23: ArcOfCircle CenterX=-1.5 CenterY=15.75 CenterZ=0 NormalX=0 NormalY=0 NormalZ=1 AngleXU=0 Radius=1.5 StartAngle=4.71239 EndAngle=7.85398
    g24: LineSegment StartX=-49.19 StartY=69.25 StartZ=0 EndX=-1.5 EndY=69.25 EndZ=0
    g25: LineSegment StartX=-49.19 StartY=66.25 StartZ=0 EndX=-1.5 EndY=66.25 EndZ=0
    g26: LineSegment StartX=-49.19 StartY=63.5 StartZ=0 EndX=-1.5 EndY=63.5 EndZ=0
    g27: LineSegment StartX=-49.19 StartY=60.5 StartZ=0 EndX=-1.5 EndY=60.5 EndZ=0
    g28: LineSegment StartX=-49.19 StartY=57.75 StartZ=0 EndX=-1.5 EndY=57.75 EndZ=0
    g29: LineSegment StartX=-49.19 StartY=54.75 StartZ=0 EndX=-1.5 EndY=54.75 EndZ=0
    g30: LineSegment StartX=-49.19 StartY=52 StartZ=0 EndX=-11.49 EndY=52 EndZ=0
    g31: LineSegment StartX=-49.19 StartY=49 StartZ=0 EndX=-11.49 EndY=49 EndZ=0
    g32: LineSegment StartX=-49.19 StartY=46.25 StartZ=0 EndX=-16.28 EndY=46.25 EndZ=0
    g33: LineSegment StartX=-49.19 StartY=43.25 StartZ=0 EndX=-16.28 EndY=43.25 EndZ=0
    g34: LineSegment StartX=-49.19 StartY=40.5 StartZ=0 EndX=-18.2337 EndY=40.5 EndZ=0
    g35: LineSegment StartX=-49.19 StartY=37.5 StartZ=0 EndX=-18.23 EndY=37.5 EndZ=0
    g36: LineSegment StartX=-49.19 StartY=34.5 StartZ=0 EndX=-18.2337 EndY=34.5 EndZ=0
    g37: LineSegment StartX=-49.19 StartY=31.5 StartZ=0 EndX=-18.23 EndY=31.5 EndZ=0
    g38: LineSegment StartX=-49.19 StartY=28.75 StartZ=0 EndX=-16.2837 EndY=28.75 EndZ=0
    g39: LineSegment StartX=-49.19 StartY=25.75 StartZ=0 EndX=-16.28 EndY=25.75 EndZ=0
    g40: LineSegment StartX=-49.19 StartY=23 StartZ=0 EndX=-11.49 EndY=23 EndZ=0
    g41: LineSegment StartX=-49.19 StartY=20 StartZ=0 EndX=-11.49 EndY=20 EndZ=0
    g42: LineSegment StartX=-49.19 StartY=17.25 StartZ=0 EndX=-1.5 EndY=17.25 EndZ=0
    g43: LineSegment StartX=-49.19 StartY=14.25 StartZ=0 EndX=-1.5 EndY=14.25 EndZ=0
    g44: LineSegment StartX=-49.19 StartY=11.5 StartZ=0 EndX=-1.5 EndY=11.5 EndZ=0
    g45: LineSegment StartX=-49.19 StartY=8.5 StartZ=0 EndX=-1.5 EndY=8.5 EndZ=0
    g46: LineSegment StartX=-49.19 StartY=5.75 StartZ=0 EndX=-1.5 EndY=5.75 EndZ=0
    g47: LineSegment StartX=-49.19 StartY=2.75 StartZ=0 EndX=-1.5 EndY=2.75 EndZ=0
  constraints (120):
    c: Vertical(g0)
    c: Distance(g0) = 3
    c: Block(g0)
    c: Vertical(g1)
    c: Distance(g1) = 3
    c: Vertical(g2)
    c: Equal(g0,g2) = 3
    c: Block(g2)
    c: Vertical(g3)
    c: Equal(g1,g3) = 3
    c: Vertical(g4)
    c: Equal(g0,g4) = 3
    c: Block(g4)
    c: Vertical(g5)
    c: Equal(g1,g5) = 3
    c: Vertical(g6)
    c: Equal(g0,g6) = 3
    c: Block(g6)
    c: Vertical(g7)
    c: Equal(g1,g7) = 3
    c: Vertical(g8)
    c: Equal(g0,g8) = 3
    c: Block(g8)
    c: Vertical(g9)
    c: Equal(g1,g9) = 3
    c: Vertical(g10)
    c: Equal(g0,g10) = 3
    c: Block(g10)
    c: Vertical(g11)
    c: Equal(g1,g11) = 3
    c: Block(g12)
    c: Block(g13)
    c: Block(g14)
    c: Block(g15)
    c: Block(g16)
    c: Block(g17)
    c: Block(g18)
    c: Block(g19)
    c: Block(g20)
    c: Block(g21)
    c: Block(g22)
    c: Block(g23)
    c: Block(g11)
    c: Block(g9)
    c: Block(g7)
    c: Block(g5)
    c: Block(g3)
    c: Block(g1)
    c: Coincident(g24,g0)
    c: Coincident(g24,g12)
    c: Horizontal(g24)
    c: Coincident(g25,g0)
    c: Coincident(g25,g12)
    c: Horizontal(g25)
    c: Coincident(g26,g1)
    c: Coincident(g26,g13)
    c: Horizontal(g26)
    c: Coincident(g27,g1)
    c: Coincident(g27,g13)
    c: Horizontal(g27)
    c: Coincident(g28,g2)
    c: Coincident(g28,g14)
    c: Horizontal(g28)
    c: Coincident(g29,g2)
    c: Coincident(g29,g14)
    c: Horizontal(g29)
    c: Coincident(g30,g3)
    c: Coincident(g30,g15)
    c: Horizontal(g30)
    c: Coincident(g31,g3)
    c: Coincident(g31,g15)
    c: Horizontal(g31)
    c: Coincident(g32,g4)
    c: Coincident(g32,g16)
    c: Horizontal(g32)
    c: Coincident(g33,g4)
    c: Coincident(g33,g16)
    c: Horizontal(g33)
    c: Coincident(g34,g5)
    c: Coincident(g34,g17)
    c: Horizontal(g34)
    c: Coincident(g35,g5)
    c: Coincident(g35,g17)
    c: Horizontal(g35)
    c: Coincident(g36,g6)
    c: Coincident(g36,g19)
    c: Horizontal(g36)
    c: Coincident(g37,g6)
    c: Coincident(g37,g19)
    c: Horizontal(g37)
    c: Coincident(g38,g7)
    c: Coincident(g38,g18)
    c: Horizontal(g38)
    c: Coincident(g39,g7)
    c: Coincident(g39,g18)
    c: Horizontal(g39)
    c: Coincident(g40,g8)
    c: Coincident(g40,g20)
    c: Horizontal(g40)
    c: Coincident(g41,g8)
    c: Coincident(g41,g20)
    c: Horizontal(g41)
    c: Coincident(g42,g9)
    c: Coincident(g42,g23)
    c: Horizontal(g42)
    c: Coincident(g43,g9)
    c: Coincident(g43,g23)
    c: Horizontal(g43)
    c: Coincident(g44,g10)
    c: Coincident(g44,g22)
    c: Horizontal(g44)
    c: Coincident(g45,g10)
    c: Coincident(g45,g22)
    c: Horizontal(g45)
    c: Coincident(g46,g11)
    c: Coincident(g46,g21)
    c: Horizontal(g46)
    c: Coincident(g47,g11)
    c: Coincident(g47,g21)
    c: Horizontal(g47)
FEATURE [Sketcher::SketchObject] Sketch031
  FullyConstrained = true
  Placement = pos=(117,19,0) rot=(0.57735,0.57735,0.57735;2.0944rad)
  sketch-geometry (24):
    g0: ArcOfCircle CenterX=-49.19 CenterY=67.75 CenterZ=0 NormalX=0 NormalY=0 NormalZ=1 AngleXU=0 Radius=1.5 StartAngle=1.5708 EndAngle=4.71239
    g1: ArcOfCircle CenterX=-49.19 CenterY=62 CenterZ=0 NormalX=0 NormalY=0 NormalZ=1 AngleXU=0 Radius=1.5 StartAngle=1.5708 EndAngle=4.71239
    g2: ArcOfCircle CenterX=-49.19 CenterY=56.25 CenterZ=0 NormalX=0 NormalY=0 NormalZ=1 AngleXU=0 Radius=1.5 StartAngle=1.5708 EndAngle=4.71239
    g3: ArcOfCircle CenterX=-49.19 CenterY=50.5 CenterZ=0 NormalX=0 NormalY=0 NormalZ=1 AngleXU=0 Radius=1.5 StartAngle=1.5708 EndAngle=4.71239
    g4: ArcOfCircle CenterX=-49.19 CenterY=44.75 CenterZ=0 NormalX=0 NormalY=0 NormalZ=1 AngleXU=0 Radius=1.5 StartAngle=1.5708 EndAngle=4.71239
    g5: ArcOfCircle CenterX=-49.19 CenterY=39 CenterZ=0 NormalX=0 NormalY=0 NormalZ=1 AngleXU=0 Radius=1.5 StartAngle=1.5708 EndAngle=4.71239
    g6: ArcOfCircle CenterX=-49.19 CenterY=33 CenterZ=0 NormalX=0 NormalY=0 NormalZ=1 AngleXU=0 Radius=1.5 StartAngle=1.5708 EndAngle=4.71239
    g7: ArcOfCircle CenterX=-49.19 CenterY=27.25 CenterZ=0 NormalX=0 NormalY=0 NormalZ=1 AngleXU=0 Radius=1.5 StartAngle=1.5708 EndAngle=4.71239
    g8: ArcOfCircle CenterX=-49.19 CenterY=21.5 CenterZ=0 NormalX=0 NormalY=0 NormalZ=1 AngleXU=0 Radius=1.5 StartAngle=1.5708 EndAngle=4.71239
    g9: ArcOfCircle CenterX=-49.19 CenterY=15.75 CenterZ=0 NormalX=0 NormalY=0 NormalZ=1 AngleXU=0 Radius=1.5 StartAngle=1.5708 EndAngle=4.71239
    g10: ArcOfCircle CenterX=-49.19 CenterY=10 CenterZ=0 NormalX=0 NormalY=0 NormalZ=1 AngleXU=0 Radius=1.5 StartAngle=1.5708 EndAngle=4.71239
    g11: ArcOfCircle CenterX=-49.19 CenterY=4.25 CenterZ=0 NormalX=0 NormalY=0 NormalZ=1 AngleXU=0 Radius=1.5 StartAngle=1.5708 EndAngle=4.71239
    g12: LineSegment StartX=-49.19 StartY=69.25 StartZ=0 EndX=-49.19 EndY=66.25 EndZ=0
    g13: LineSegment StartX=-49.19 StartY=63.5 StartZ=0 EndX=-49.19 EndY=60.5 EndZ=0
    g14: LineSegment StartX=-49.19 StartY=57.75 StartZ=0 EndX=-49.19 EndY=54.75 EndZ=0
    g15: LineSegment StartX=-49.19 StartY=52 StartZ=0 EndX=-49.19 EndY=49 EndZ=0
    g16: LineSegment StartX=-49.19 StartY=46.25 StartZ=0 EndX=-49.19 EndY=43.25 EndZ=0
    g17: LineSegment StartX=-49.19 StartY=40.5 StartZ=0 EndX=-49.19 EndY=37.5 EndZ=0
    g18: LineSegment StartX=-49.19 StartY=34.5 StartZ=0 EndX=-49.19 EndY=31.5 EndZ=0
    g19: LineSegment StartX=-49.19 StartY=28.75 StartZ=0 EndX=-49.19 EndY=25.75 EndZ=0
    g20: LineSegment StartX=-49.19 StartY=23 StartZ=0 EndX=-49.19 EndY=20 EndZ=0
    g21: LineSegment StartX=-49.19 StartY=17.25 StartZ=0 EndX=-49.19 EndY=14.25 EndZ=0
    g22: LineSegment StartX=-49.19 StartY=11.5 StartZ=0 EndX=-49.19 EndY=8.5 EndZ=0
    g23: LineSegment StartX=-49.19 StartY=5.75 StartZ=0 EndX=-49.19 EndY=2.75 EndZ=0
  constraints (48):
    c: Block(g0)
    c: Block(g1)
    c: Block(g2)
    c: Block(g3)
    c: Block(g4)
    c: Block(g5)
    c: Block(g6)
    c: Block(g7)
    c: Block(g8)
    c: Block(g9)
    c: Block(g10)
    c: Block(g11)
    c: Coincident(g12,g0)
    c: Coincident(g12,g0)
    c: Vertical(g12)
    c: Vertical(g13)
    c: Coincident(g13,g1)
    c: Vertical(g14)
    c: Coincident(g14,g2)
    c: Vertical(g15)
    c: Coincident(g15,g3)
    c: Vertical(g16)
    c: Coincident(g16,g4)
    c: Vertical(g17)
    c: Coincident(g17,g5)
    c: Vertical(g18)
    c: Coincident(g18,g6)
    c: Vertical(g19)
    c: Coincident(g19,g7)
    c: Vertical(g20)
    c: Coincident(g20,g8)
    c: Vertical(g21)
    c: Coincident(g21,g9)
    c: Vertical(g22)
    c: Coincident(g22,g10)
    c: Vertical(g23)
    c: Coincident(g23,g11)
    c: Block(g23)
    c: Block(g22)
    c: Block(g21)
    c: Block(g20)
    c: Block(g13)
    c: Block(g14)
    c: Block(g15)
    c: Block(g16)
    c: Block(g17)
    c: Block(g18)
    c: Block(g19)
FEATURE [Part::Extrusion] Extrude022
  Base = -> Sketch030
  Dir = (1,-2e-16,2e-16)
  DirMode = 2
  FaceMakerClass = Part::FaceMakerBullseye
  LengthFwd = 19
  LengthRev = 0
  Placement = pos=(-19,0,0) rot=(0,0,1;0rad)
  Solid = true
  Symmetric = false
FEATURE [Part::Fillet] Fillet022
  Base = -> Extrude022
  Edges = 24 edges r=1.49: [Edge6,Edge11,Edge18,Edge23,Edge30,Edge35,Edge42,Edge47,Edge54,Edge59,Edge66,Edge71,Edge78,Edge83,Edge90,Edge95,Edge102,Edge107,Edge114,Edge119,Edge126,Edge131,Edge138,Edge143]
FEATURE [Part::Cut] Cut020  label="top010"
  Base = -> Cut019
  Tool = -> Fillet022
FEATURE [Sketcher::SketchObject] Sketch032
  FullyConstrained = true
  Placement = pos=(117,19,0) rot=(0.57735,0.57735,0.57735;2.0944rad)
  sketch-geometry (48):
    g0: LineSegment StartX=-49.19 StartY=69.25 StartZ=0 EndX=-49.19 EndY=66.25 EndZ=0
    g1: LineSegment StartX=-49.19 StartY=63.5 StartZ=0 EndX=-49.19 EndY=60.5 EndZ=0
    g2: LineSegment StartX=-49.19 StartY=57.75 StartZ=0 EndX=-49.19 EndY=54.75 EndZ=0
    g3: LineSegment StartX=-49.19 StartY=52 StartZ=0 EndX=-49.19 EndY=49 EndZ=0
    g4: LineSegment StartX=-49.19 StartY=46.25 StartZ=0 EndX=-49.19 EndY=43.25 EndZ=0
    g5: LineSegment StartX=-49.19 StartY=40.5 StartZ=0 EndX=-49.19 EndY=37.5 EndZ=0
    g6: LineSegment StartX=-49.19 StartY=34.5 StartZ=0 EndX=-49.19 EndY=31.5 EndZ=0
    g7: LineSegment StartX=-49.19 StartY=28.75 StartZ=0 EndX=-49.19 EndY=25.75 EndZ=0
    g8: LineSegment StartX=-49.19 StartY=23 StartZ=0 EndX=-49.19 EndY=20 EndZ=0
    g9: LineSegment StartX=-49.19 StartY=17.25 StartZ=0 EndX=-49.19 EndY=14.25 EndZ=0
    g10: LineSegment StartX=-49.19 StartY=11.5 StartZ=0 EndX=-49.19 EndY=8.5 EndZ=0
    g11: LineSegment StartX=-49.19 StartY=5.75 StartZ=0 EndX=-49.19 EndY=2.75 EndZ=0
    g12: ArcOfCircle CenterX=-1.5 CenterY=67.75 CenterZ=0 NormalX=0 NormalY=0 NormalZ=1 AngleXU=0 Radius=1.5 StartAngle=4.71239 EndAngle=7.85398
    g13: ArcOfCircle CenterX=-1.5 CenterY=62 CenterZ=0 NormalX=0 NormalY=0 NormalZ=1 AngleXU=0 Radius=1.5 StartAngle=4.71239 EndAngle=7.85398
    g14: ArcOfCircle CenterX=-1.5 CenterY=56.25 CenterZ=0 NormalX=0 NormalY=0 NormalZ=1 AngleXU=0 Radius=1.5 StartAngle=4.71239 EndAngle=7.85398
    g15: ArcOfCircle CenterX=-11.49 CenterY=50.5 CenterZ=0 NormalX=0 NormalY=0 NormalZ=1 AngleXU=0 Radius=1.5 StartAngle=4.71239 EndAngle=7.85398
    g16: ArcOfCircle CenterX=-16.28 CenterY=44.75 CenterZ=0 NormalX=0 NormalY=0 NormalZ=1 AngleXU=0 Radius=1.5 StartAngle=4.71239 EndAngle=7.85398
    g17: ArcOfCircle CenterX=-18.2337 CenterY=39 CenterZ=0 NormalX=0 NormalY=0 NormalZ=1 AngleXU=0 Radius=1.5 StartAngle=4.71485 EndAngle=7.85398
    g18: ArcOfCircle CenterX=-16.2837 CenterY=27.25 CenterZ=0 NormalX=0 NormalY=0 NormalZ=1 AngleXU=0 Radius=1.5 StartAngle=4.71485 EndAngle=7.85398
    g19: ArcOfCircle CenterX=-18.2337 CenterY=33 CenterZ=0 NormalX=0 NormalY=0 NormalZ=1 AngleXU=0 Radius=1.5 StartAngle=4.71485 EndAngle=7.85398
    g20: ArcOfCircle CenterX=-11.49 CenterY=21.5 CenterZ=0 NormalX=0 NormalY=0 NormalZ=1 AngleXU=0 Radius=1.5 StartAngle=4.71239 EndAngle=7.85398
    g21: ArcOfCircle CenterX=-1.5 CenterY=4.25 CenterZ=0 NormalX=0 NormalY=0 NormalZ=1 AngleXU=0 Radius=1.5 StartAngle=4.71239 EndAngle=7.85398
    g22: ArcOfCircle CenterX=-1.5 CenterY=10 CenterZ=0 NormalX=0 NormalY=0 NormalZ=1 AngleXU=0 Radius=1.5 StartAngle=4.71239 EndAngle=7.85398
    g23: ArcOfCircle CenterX=-1.5 CenterY=15.75 CenterZ=0 NormalX=0 NormalY=0 NormalZ=1 AngleXU=0 Radius=1.5 StartAngle=4.71239 EndAngle=7.85398
    g24: LineSegment StartX=-49.19 StartY=69.25 StartZ=0 EndX=-1.5 EndY=69.25 EndZ=0
    g25: LineSegment StartX=-49.19 StartY=66.25 StartZ=0 EndX=-1.5 EndY=66.25 EndZ=0
    g26: LineSegment StartX=-49.19 StartY=63.5 StartZ=0 EndX=-1.5 EndY=63.5 EndZ=0
    g27: LineSegment StartX=-49.19 StartY=60.5 StartZ=0 EndX=-1.5 EndY=60.5 EndZ=0
    g28: LineSegment StartX=-49.19 StartY=57.75 StartZ=0 EndX=-1.5 EndY=57.75 EndZ=0
    g29: LineSegment StartX=-49.19 StartY=54.75 StartZ=0 EndX=-1.5 EndY=54.75 EndZ=0
    g30: LineSegment StartX=-49.19 StartY=52 StartZ=0 EndX=-11.49 EndY=52 EndZ=0
    g31: LineSegment StartX=-49.19 StartY=49 StartZ=0 EndX=-11.49 EndY=49 EndZ=0
    g32: LineSegment StartX=-49.19 StartY=46.25 StartZ=0 EndX=-16.28 EndY=46.25 EndZ=0
    g33: LineSegment StartX=-49.19 StartY=43.25 StartZ=0 EndX=-16.28 EndY=43.25 EndZ=0
    g34: LineSegment StartX=-49.19 StartY=40.5 StartZ=0 EndX=-18.2337 EndY=40.5 EndZ=0
    g35: LineSegment StartX=-49.19 StartY=37.5 StartZ=0 EndX=-18.23 EndY=37.5 EndZ=0
    g36: LineSegment StartX=-49.19 StartY=34.5 StartZ=0 EndX=-18.2337 EndY=34.5 EndZ=0
    g37: LineSegment StartX=-49.19 StartY=31.5 StartZ=0 EndX=-18.23 EndY=31.5 EndZ=0
    g38: LineSegment StartX=-49.19 StartY=28.75 StartZ=0 EndX=-16.2837 EndY=28.75 EndZ=0
    g39: LineSegment StartX=-49.19 StartY=25.75 StartZ=0 EndX=-16.28 EndY=25.75 EndZ=0
    g40: LineSegment StartX=-49.19 StartY=23 StartZ=0 EndX=-11.49 EndY=23 EndZ=0
    g41: LineSegment StartX=-49.19 StartY=20 StartZ=0 EndX=-11.49 EndY=20 EndZ=0
    g42: LineSegment StartX=-49.19 StartY=17.25 StartZ=0 EndX=-1.5 EndY=17.25 EndZ=0
    g43: LineSegment StartX=-49.19 StartY=14.25 StartZ=0 EndX=-1.5 EndY=14.25 EndZ=0
    g44: LineSegment StartX=-49.19 StartY=11.5 StartZ=0 EndX=-1.5 EndY=11.5 EndZ=0
    g45: LineSegment StartX=-49.19 StartY=8.5 StartZ=0 EndX=-1.5 EndY=8.5 EndZ=0
    g46: LineSegment StartX=-49.19 StartY=5.75 StartZ=0 EndX=-1.5 EndY=5.75 EndZ=0
    g47: LineSegment StartX=-49.19 StartY=2.75 StartZ=0 EndX=-1.5 EndY=2.75 EndZ=0
  constraints (120):
    c: Vertical(g0)
    c: Distance(g0) = 3
    c: Block(g0)
    c: Vertical(g1)
    c: Distance(g1) = 3
    c: Vertical(g2)
    c: Equal(g0,g2) = 3
    c: Block(g2)
    c: Vertical(g3)
    c: Equal(g1,g3) = 3
    c: Vertical(g4)
    c: Equal(g0,g4) = 3
    c: Block(g4)
    c: Vertical(g5)
    c: Equal(g1,g5) = 3
    c: Vertical(g6)
    c: Equal(g0,g6) = 3
    c: Block(g6)
    c: Vertical(g7)
    c: Equal(g1,g7) = 3
    c: Vertical(g8)
    c: Equal(g0,g8) = 3
    c: Block(g8)
    c: Vertical(g9)
    c: Equal(g1,g9) = 3
    c: Vertical(g10)
    c: Equal(g0,g10) = 3
    c: Block(g10)
    c: Vertical(g11)
    c: Equal(g1,g11) = 3
    c: Block(g12)
    c: Block(g13)
    c: Block(g14)
    c: Block(g15)
    c: Block(g16)
    c: Block(g17)
    c: Block(g18)
    c: Block(g19)
    c: Block(g20)
    c: Block(g21)
    c: Block(g22)
    c: Block(g23)
    c: Block(g11)
    c: Block(g9)
    c: Block(g7)
    c: Block(g5)
    c: Block(g3)
    c: Block(g1)
    c: Coincident(g24,g0)
    c: Coincident(g24,g12)
    c: Horizontal(g24)
    c: Coincident(g25,g0)
    c: Coincident(g25,g12)
    c: Horizontal(g25)
    c: Coincident(g26,g1)
    c: Coincident(g26,g13)
    c: Horizontal(g26)
    c: Coincident(g27,g1)
    c: Coincident(g27,g13)
    c: Horizontal(g27)
    c: Coincident(g28,g2)
    c: Coincident(g28,g14)
    c: Horizontal(g28)
    c: Coincident(g29,g2)
    c: Coincident(g29,g14)
    c: Horizontal(g29)
    c: Coincident(g30,g3)
    c: Coincident(g30,g15)
    c: Horizontal(g30)
    c: Coincident(g31,g3)
    c: Coincident(g31,g15)
    c: Horizontal(g31)
    c: Coincident(g32,g4)
    c: Coincident(g32,g16)
    c: Horizontal(g32)
    c: Coincident(g33,g4)
    c: Coincident(g33,g16)
    c: Horizontal(g33)
    c: Coincident(g34,g5)
    c: Coincident(g34,g17)
    c: Horizontal(g34)
    c: Coincident(g35,g5)
    c: Coincident(g35,g17)
    c: Horizontal(g35)
    c: Coincident(g36,g6)
    c: Coincident(g36,g19)
    c: Horizontal(g36)
    c: Coincident(g37,g6)
    c: Coincident(g37,g19)
    c: Horizontal(g37)
    c: Coincident(g38,g7)
    c: Coincident(g38,g18)
    c: Horizontal(g38)
    c: Coincident(g39,g7)
    c: Coincident(g39,g18)
    c: Horizontal(g39)
    c: Coincident(g40,g8)
    c: Coincident(g40,g20)
    c: Horizontal(g40)
    c: Coincident(g41,g8)
    c: Coincident(g41,g20)
    c: Horizontal(g41)
    c: Coincident(g42,g9)
    c: Coincident(g42,g23)
    c: Horizontal(g42)
    c: Coincident(g43,g9)
    c: Coincident(g43,g23)
    c: Horizontal(g43)
    c: Coincident(g44,g10)
    c: Coincident(g44,g22)
    c: Horizontal(g44)
    c: Coincident(g45,g10)
    c: Coincident(g45,g22)
    c: Horizontal(g45)
    c: Coincident(g46,g11)
    c: Coincident(g46,g21)
    c: Horizontal(g46)
    c: Coincident(g47,g11)
    c: Coincident(g47,g21)
    c: Horizontal(g47)
FEATURE [Part::Extrusion] Extrude023
  Base = -> Sketch032
  Dir = (1,-2e-16,2e-16)
  DirMode = 2
  FaceMakerClass = Part::FaceMakerBullseye
  LengthFwd = 19
  LengthRev = 0
  Placement = pos=(-19,0,0) rot=(0,0,1;0rad)
  Solid = true
  Symmetric = false
FEATURE [Part::Fillet] Fillet023
  Base = -> Extrude023
  Edges = 24 edges r=1.49: [Edge6,Edge11,Edge18,Edge23,Edge30,Edge35,Edge42,Edge47,Edge54,Edge59,Edge66,Edge71,Edge78,Edge83,Edge90,Edge95,Edge102,Edge107,Edge114,Edge119,Edge126,Edge131,Edge138,Edge143]
  Placement = pos=(0,0.05,0) rot=(0,0,1;0rad)
FEATURE [Part::Cut] Cut014  label="bottom003"
  Base = -> Cut007
  Tool = -> Fusion047
FEATURE [Part::Cut] Cut021  label="bottom004"
  Base = -> Cut014
  Tool = -> Fillet023
FEATURE [Sketcher::SketchObject] Sketch033
  FullyConstrained = true
  Placement = pos=(117,19,0) rot=(0.57735,0.57735,0.57735;2.0944rad)
  sketch-geometry (8):
    g0: LineSegment StartX=-49.19 StartY=69.25 StartZ=0 EndX=-49.19 EndY=66.25 EndZ=0
    g1: LineSegment StartX=-49.19 StartY=5.75 StartZ=0 EndX=-49.19 EndY=2.75 EndZ=0
    g2: ArcOfCircle CenterX=-1.5 CenterY=67.75 CenterZ=0 NormalX=0 NormalY=0 NormalZ=1 AngleXU=0 Radius=1.5 StartAngle=4.71239 EndAngle=7.85398
    g3: ArcOfCircle CenterX=-1.5 CenterY=4.25 CenterZ=0 NormalX=0 NormalY=0 NormalZ=1 AngleXU=0 Radius=1.5 StartAngle=4.71239 EndAngle=7.85398
    g4: LineSegment StartX=-49.19 StartY=69.25 StartZ=0 EndX=-1.5 EndY=69.25 EndZ=0
    g5: LineSegment StartX=-49.19 StartY=66.25 StartZ=0 EndX=-1.5 EndY=66.25 EndZ=0
    g6: LineSegment StartX=-49.19 StartY=5.75 StartZ=0 EndX=-1.5 EndY=5.75 EndZ=0
    g7: LineSegment StartX=-49.19 StartY=2.75 StartZ=0 EndX=-1.5 EndY=2.75 EndZ=0
  constraints (19):
    c: Vertical(g0)
    c: Distance(g0) = 3
    c: Block(g0)
    c: Vertical(g1)
    c: Block(g2)
    c: Block(g3)
    c: Block(g1)
    c: Coincident(g4,g0)
    c: Coincident(g4,g2)
    c: Horizontal(g4)
    c: Coincident(g5,g0)
    c: Coincident(g5,g2)
    c: Horizontal(g5)
    c: Coincident(g6,g1)
    c: Coincident(g6,g3)
    c: Horizontal(g6)
    c: Coincident(g7,g1)
    c: Coincident(g7,g3)
    c: Horizontal(g7)
FEATURE [Sketcher::SketchObject] Sketch034
  FullyConstrained = true
  Placement = pos=(117,19,0) rot=(0.57735,0.57735,0.57735;2.0944rad)
  sketch-geometry (8):
    g0: LineSegment StartX=-49.19 StartY=63.5 StartZ=0 EndX=-49.19 EndY=60.5 EndZ=0
    g1: LineSegment StartX=-49.19 StartY=11.5 StartZ=0 EndX=-49.19 EndY=8.5 EndZ=0
    g2: ArcOfCircle CenterX=-1.5 CenterY=62 CenterZ=0 NormalX=0 NormalY=0 NormalZ=1 AngleXU=0 Radius=1.5 StartAngle=4.71239 EndAngle=7.85398
    g3: ArcOfCircle CenterX=-1.5 CenterY=10 CenterZ=0 NormalX=0 NormalY=0 NormalZ=1 AngleXU=0 Radius=1.5 StartAngle=4.71239 EndAngle=7.85398
    g4: LineSegment StartX=-49.19 StartY=63.5 StartZ=0 EndX=-1.5 EndY=63.5 EndZ=0
    g5: LineSegment StartX=-49.19 StartY=60.5 StartZ=0 EndX=-1.5 EndY=60.5 EndZ=0
    g6: LineSegment StartX=-49.19 StartY=11.5 StartZ=0 EndX=-1.5 EndY=11.5 EndZ=0
    g7: LineSegment StartX=-49.19 StartY=8.5 StartZ=0 EndX=-1.5 EndY=8.5 EndZ=0
  constraints (19):
    c: Vertical(g0)
    c: Distance(g0) = 3
    c: Vertical(g1)
    c: Block(g1)
    c: Block(g2)
    c: Block(g3)
    c: Block(g0)
    c: Coincident(g4,g0)
    c: Coincident(g4,g2)
    c: Horizontal(g4)
    c: Coincident(g5,g0)
    c: Coincident(g5,g2)
    c: Horizontal(g5)
    c: Coincident(g6,g1)
    c: Coincident(g6,g3)
    c: Horizontal(g6)
    c: Coincident(g7,g1)
    c: Coincident(g7,g3)
    c: Horizontal(g7)
FEATURE [Part::Extrusion] Extrude024
  Base = -> Sketch033
  Dir = (1,0,0)
  DirMode = 2
  FaceMakerClass = Part::FaceMakerBullseye
  LengthFwd = 10
  LengthRev = 0
  Solid = true
  Symmetric = false
FEATURE [Part::Extrusion] Extrude025
  Base = -> Sketch034
  Dir = (1,0,0)
  DirMode = 2
  FaceMakerClass = Part::FaceMakerBullseye
  LengthFwd = 10
  LengthRev = 0
  Solid = true
  Symmetric = false
FEATURE [Part::Fillet] Fillet024  label="removeFromtMoreFrontCaseScrewRetainers"
  Base = -> Extrude024
  Edges = 4 edges r=1.49: [Edge6,Edge11,Edge18,Edge23]
  Placement = pos=(-11,0,0) rot=(0,0,1;0rad)
FEATURE [Part::Fillet] Fillet025  label="removeFromtMoreFrontCaseScrewRetainers001"
  Base = -> Extrude025
  Edges = 4 edges r=1.49: [Edge6,Edge11,Edge18,Edge23]
  Placement = pos=(-19,0,0) rot=(0,0,1;0rad)
FEATURE [Part::Cut] Cut022
  Base = -> Cut015
  Tool = -> Fillet025
FEATURE [Part::Cut] Cut023  label="screwRetainers"
  Base = -> Cut022
  Tool = -> Fillet024
FEATURE [Part::MultiFuse] Fusion056  label="bottom005"
  Shapes = -> [Fusion044,Cut021]
FEATURE [Part::MultiFuse] Fusion057  label="casePillars001"
  Shapes = -> [Cut016,Fusion052]
FEATURE [Part::MultiFuse] Fusion058  label="bottom006"
  Shapes = -> [Fusion056,Cut023]
FEATURE [Part::MultiFuse] Fusion059  label="bottom007"
  Shapes = -> [Fusion058,Fillet005]
FEATURE [Part::MultiFuse] Fusion060  label="bottom008"
  Shapes = -> [Fusion059,Fusion]
FEATURE [Part::MultiFuse] Fusion061  label="top011"
  Shapes = -> [Cut006,Cut020]
FEATURE [Part::MultiFuse] Fusion062  label="top012"
  Shapes = -> [Fusion057,Fusion061]
FEATURE [Sketcher::SketchObject] Sketch035  label="topSketch007"
  FullyConstrained = true
  sketch-geometry (6):
    g0: LineSegment StartX=19 StartY=38 StartZ=0 EndX=117 EndY=38 EndZ=0
    g1: ArcOfCircle CenterX=19 CenterY=19 CenterZ=0 NormalX=0 NormalY=0 NormalZ=1 AngleXU=0 Radius=19 StartAngle=1.5708 EndAngle=3.14159
    g2: LineSegment StartX=117 StartY=38 StartZ=0 EndX=117 EndY=19 EndZ=0
    g3: LineSegment StartX=98 StartY=1.0161e-12 StartZ=0 EndX=5.22862e-06 EndY=1.0161e-12 EndZ=0
    g4: LineSegment StartX=5.22862e-06 StartY=19 StartZ=0 EndX=5.22862e-06 EndY=1.0161e-12 EndZ=0
    g5: ArcOfCircle CenterX=98 CenterY=19 CenterZ=0 NormalX=0 NormalY=0 NormalZ=1 AngleXU=0 Radius=19 StartAngle=4.71239 EndAngle=6.28319
  constraints (16):
    c: Horizontal(g0)
    c: Distance(g0) = 98
    c: Coincident(g1,g0)
    c: Block(g1)
    c: Coincident(g2,g0)
    c: Vertical(g2)
    c: Distance(g2) = 19
    c: Horizontal(g3)
    c: Coincident(g4,g1)
    c: Vertical(g4)
    c: Coincident(g3,g4)
    c: Block(g3)
    c: Coincident(g5,g2)
    c: Coincident(g5,g3)
    c: Block(g0)
    c: Block(g5)
FEATURE [Part::Extrusion] Extrude026  label="sideA001"
  Base = -> Sketch035
  Dir = (0,0,1)
  DirMode = 2
  FaceMakerClass = Part::FaceMakerBullseye
  LengthFwd = 3
  LengthRev = 0
  Placement = pos=(0,0,-2.7) rot=(0,0,1;0rad)
  Solid = true
  Symmetric = false
FEATURE [Sketcher::SketchObject] Sketch036  label="topSketch008"
  FullyConstrained = true
  sketch-geometry (6):
    g0: LineSegment StartX=19 StartY=38 StartZ=0 EndX=117 EndY=38 EndZ=0
    g1: ArcOfCircle CenterX=19 CenterY=19 CenterZ=0 NormalX=0 NormalY=0 NormalZ=1 AngleXU=0 Radius=19 StartAngle=1.5708 EndAngle=3.14159
    g2: LineSegment StartX=117 StartY=38 StartZ=0 EndX=117 EndY=19 EndZ=0
    g3: LineSegment StartX=98 StartY=1.0161e-12 StartZ=0 EndX=5.22862e-06 EndY=1.0161e-12 EndZ=0
    g4: LineSegment StartX=5.22862e-06 StartY=19 StartZ=0 EndX=5.22862e-06 EndY=1.0161e-12 EndZ=0
    g5: ArcOfCircle CenterX=98 CenterY=19 CenterZ=0 NormalX=0 NormalY=0 NormalZ=1 AngleXU=0 Radius=19 StartAngle=4.71239 EndAngle=6.28319
  constraints (16):
    c: Horizontal(g0)
    c: Distance(g0) = 98
    c: Coincident(g1,g0)
    c: Block(g1)
    c: Coincident(g2,g0)
    c: Vertical(g2)
    c: Distance(g2) = 19
    c: Horizontal(g3)
    c: Coincident(g4,g1)
    c: Vertical(g4)
    c: Coincident(g3,g4)
    c: Block(g3)
    c: Coincident(g5,g2)
    c: Coincident(g5,g3)
    c: Block(g0)
    c: Block(g5)
FEATURE [Part::Extrusion] Extrude027  label="sideB001"
  Base = -> Sketch036
  Dir = (0,0,1)
  DirMode = 2
  FaceMakerClass = Part::FaceMakerBullseye
  LengthFwd = 3
  LengthRev = 0
  Placement = pos=(0,0,71.7) rot=(0,0,1;0rad)
  Solid = true
  Symmetric = false
FEATURE [Part::MultiFuse] Fusion064  label="removeFromBottom"
  Shapes = -> [Extrude026,Extrude027]
FEATURE [Part::Cut] Cut024  label="bottom009"
  Base = -> Fusion060
  Tool = -> Fusion064
FEATURE [Sketcher::SketchObject] Sketch037  label="topSketch009"
  FullyConstrained = true
  sketch-geometry (6):
    g0: ArcOfCircle CenterX=19 CenterY=19 CenterZ=0 NormalX=0 NormalY=0 NormalZ=1 AngleXU=0 Radius=19 StartAngle=1.5708 EndAngle=3.14159
    g1: LineSegment StartX=5.22862e-06 StartY=19 StartZ=0 EndX=5.22862e-06 EndY=1.19904e-11 EndZ=0
    g2: LineSegment StartX=19 StartY=38 StartZ=0 EndX=124 EndY=38 EndZ=0
    g3: LineSegment StartX=5.22862e-06 StartY=1.19904e-11 StartZ=0 EndX=105 EndY=1.19904e-11 EndZ=0
    g4: ArcOfCircle CenterX=105 CenterY=19 CenterZ=0 NormalX=0 NormalY=0 NormalZ=1 AngleXU=0 Radius=19 StartAngle=4.71239 EndAngle=6.28319
    g5: LineSegment StartX=124 StartY=38 StartZ=0 EndX=124 EndY=19 EndZ=0
  constraints (16):
    c: Block(g0)
    c: Coincident(g1,g0)
    c: Vertical(g1)
    c: Horizontal(g2)
    c: Distance(g2) = 105
    c: Coincident(g2,g0)
    c: Distance(g1) = 19
    c: Coincident(g3,g1)
    c: Horizontal(g3)
    c: Distance(g3) = 105
    c: Block(g4)
    c: Coincident(g4,g3)
    c: Coincident(g5,g2)
    c: Coincident(g5,g4)
    c: Vertical(g5)
    c: Distance(g5) = 19
FEATURE [Part::Extrusion] Extrude028  label="sideB"
  Base = -> Sketch037
  Dir = (0,0,1)
  DirMode = 2
  FaceMakerClass = Part::FaceMakerBullseye
  LengthFwd = 3
  LengthRev = 0
  Placement = pos=(0,0,72) rot=(0,0,1;0rad)
  Solid = true
  Symmetric = false
FEATURE [Sketcher::SketchObject] Sketch038  label="topSketch010"
  FullyConstrained = true
  sketch-geometry (20):
    g0: LineSegment StartX=5.21097e-06 StartY=3 StartZ=0 EndX=5.21097e-06 EndY=19 EndZ=0
    g1: ArcOfCircle CenterX=19 CenterY=19 CenterZ=0 NormalX=0 NormalY=0 NormalZ=1 AngleXU=0 Radius=19 StartAngle=1.5708 EndAngle=3.14159
    g2: ArcOfCircle CenterX=19 CenterY=19 CenterZ=0 NormalX=0 NormalY=0 NormalZ=1 AngleXU=0 Radius=16 StartAngle=1.5708 EndAngle=3.14159
    g3: LineSegment StartX=114 StartY=35 StartZ=0 EndX=19 EndY=35 EndZ=0
    g4: LineSegment StartX=5.21097e-06 StartY=3 StartZ=0 EndX=5.21097e-06 EndY=0 EndZ=0
    g5: LineSegment StartX=3 StartY=0 StartZ=0 EndX=5.21097e-06 EndY=0 EndZ=0
    g6: LineSegment StartX=3 StartY=19 StartZ=0 EndX=3 EndY=0 EndZ=0
    g7: LineSegment StartX=19 StartY=38 StartZ=0 EndX=124 EndY=38 EndZ=0
    g8: Circle CenterX=119 CenterY=35 CenterZ=0 NormalX=0 NormalY=0 NormalZ=1 AngleXU=0 Radius=1
    g9: Circle CenterX=121 CenterY=35 CenterZ=0 NormalX=0 NormalY=0 NormalZ=1 AngleXU=0 Radius=1
    g10: Circle CenterX=121 CenterY=33 CenterZ=0 NormalX=0 NormalY=0 NormalZ=1 AngleXU=0 Radius=1
    g11: BSplineCurve PolesCount=3 KnotsCount=2 Degree=2 IsPeriodic=0
    g12: GeomPoint X=119 Y=35 Z=0
    g13: GeomPoint X=121 Y=33 Z=0
    g14: LineSegment StartX=119 StartY=35 StartZ=0 EndX=114 EndY=35 EndZ=0
    g15: ArcOfCircle CenterX=105 CenterY=19 CenterZ=0 NormalX=0 NormalY=0 NormalZ=1 AngleXU=0 Radius=19 StartAngle=5.7297 EndAngle=6.28319
    g16: ArcOfCircle CenterX=105 CenterY=19 CenterZ=0 NormalX=0 NormalY=0 NormalZ=1 AngleXU=0 Radius=16 StartAngle=5.60905 EndAngle=6.28319
    g17: LineSegment StartX=121 StartY=33 StartZ=0 EndX=121 EndY=19 EndZ=0
    g18: LineSegment StartX=124 StartY=38 StartZ=0 EndX=124 EndY=19 EndZ=0
    g19: LineSegment StartX=117.5 StartY=9.01251 StartZ=0 EndX=121.163 EndY=9.0125 EndZ=0
  constraints (46):
    c: Vertical(g0)
    c: Block(g0)
    c: Coincident(g1,g0)
    c: Block(g1)
    c: Coincident(g2,g1)
    c: Block(g2)
    c: Coincident(g3,g2)
    c: Horizontal(g3)
    c: Tangent(g3,g2)
    c: Coincident(g4,g0)
    c: Distance(g4) = 3
    c: Vertical(g4)
    c: Coincident(g5,g4)
    c: Horizontal(g5)
    c: Coincident(g6,g2)
    c: Coincident(g6,g5)
    c: Vertical(g6)
    c: Horizontal(g7)
    c: Distance(g7) = 105
    c: Coincident(g7,g1)
    c: Block(g3)
    c: Weight(g8) = 1
    c: Equal(g8,g9)
    c: Equal(g8,g10)
    c: InternalAlignment(g8,g11)
    c: InternalAlignment(g9,g11)
    c: InternalAlignment(g10,g11)
    c: InternalAlignment(g12,g11)
    c: InternalAlignment(g13,g11)
    c: Block(g11)
    c: Coincident(g14,g11)
    c: Coincident(g14,g3)
    c: Horizontal(g14)
    c: Block(g15)
    c: Coincident(g16,g15)
    c: Block(g16)
    c: Coincident(g17,g11)
    c: Coincident(g17,g16)
    c: Vertical(g17)
    c: Distance(g17) = 14
    c: Coincident(g18,g7)
    c: Coincident(g18,g15)
    c: Vertical(g18)
    c: Distance(g18) = 19
    c: Coincident(g19,g16)
    c: Coincident(g19,g15)
FEATURE [Part::Extrusion] Extrude029
  Base = -> Sketch038
  Dir = (0,0,1)
  DirMode = 2
  FaceMakerClass = Part::FaceMakerBullseye
  LengthFwd = 72
  LengthRev = 0
  Solid = true
  Symmetric = false
FEATURE [Part::Feature] Face085
  shape: bbox 4.8 x 25.5 x 2e-07 mm, 1 faces, 0 solids (baked)
FEATURE [Part::Revolution] Revolve089  label="moreFrontCaseScrewPost003"
  Angle = 360
  Axis = (0,1,0)
  Base = (0,0,0)
  FaceMakerClass = Part::FaceMakerBullseye
  Placement = pos=(109.5,4.5,3.5) rot=(0,0,1;0rad)
  Solid = false
  Source = -> Face085
  Symmetric = false
FEATURE [Part::Feature] Face086
  shape: bbox 4.8 x 25.5 x 2e-07 mm, 1 faces, 0 solids (baked)
FEATURE [Part::Revolution] Revolve090  label="moreFrontCaseScrewPost004"
  Angle = 360
  Axis = (0,1,0)
  Base = (0,0,0)
  FaceMakerClass = Part::FaceMakerBullseye
  Placement = pos=(109.5,4.5,68.5) rot=(0,0,1;0rad)
  Solid = false
  Source = -> Face086
  Symmetric = false
FEATURE [Part::Fillet] Fillet026  label="top013"
  Base = -> Extrude029
  Edges = 1 edges r=2: [Edge35]
FEATURE [Sketcher::SketchObject] Sketch039
  FullyConstrained = true
  sketch-geometry (7):
    g0: LineSegment StartX=0 StartY=0 StartZ=0 EndX=0 EndY=6 EndZ=0
    g1: Circle CenterX=0 CenterY=0 CenterZ=0 NormalX=0 NormalY=0 NormalZ=1 AngleXU=0 Radius=1
    g2: Circle CenterX=8 CenterY=6 CenterZ=0 NormalX=0 NormalY=0 NormalZ=1 AngleXU=0 Radius=1
    g3: BSplineCurve PolesCount=3 KnotsCount=2 Degree=2 IsPeriodic=0
    g4: GeomPoint X=0 Y=0 Z=0
    g5: GeomPoint X=8 Y=6 Z=0
    g6: LineSegment StartX=0 StartY=6 StartZ=0 EndX=8 EndY=6 EndZ=0
  constraints (14):
    c: Coincident(g0,g-1)
    c: Distance(g0) = 6
    c: Vertical(g0)
    c: Coincident(g3,g0)
    c: Weight(g1) = 1
    c: Equal(g1,g2)
    c: InternalAlignment(g1,g3)
    c: InternalAlignment(g2,g3)
    c: InternalAlignment(g4,g3)
    c: InternalAlignment(g5,g3)
    c: Block(g3)
    c: Coincident(g6,g0)
    c: Coincident(g6,g3)
    c: Horizontal(g6)
FEATURE [Sketcher::SketchObject] Sketch040
  FullyConstrained = true
  sketch-geometry (7):
    g0: LineSegment StartX=0 StartY=0 StartZ=0 EndX=0 EndY=6 EndZ=0
    g1: Circle CenterX=0 CenterY=0 CenterZ=0 NormalX=0 NormalY=0 NormalZ=1 AngleXU=0 Radius=1
    g2: Circle CenterX=8 CenterY=6 CenterZ=0 NormalX=0 NormalY=0 NormalZ=1 AngleXU=0 Radius=1
    g3: BSplineCurve PolesCount=3 KnotsCount=2 Degree=2 IsPeriodic=0
    g4: GeomPoint X=0 Y=0 Z=0
    g5: GeomPoint X=8 Y=6 Z=0
    g6: LineSegment StartX=0 StartY=6 StartZ=0 EndX=8 EndY=6 EndZ=0
  constraints (14):
    c: Coincident(g0,g-1)
    c: Distance(g0) = 6
    c: Vertical(g0)
    c: Coincident(g3,g0)
    c: Weight(g1) = 1
    c: Equal(g1,g2)
    c: InternalAlignment(g1,g3)
    c: InternalAlignment(g2,g3)
    c: InternalAlignment(g4,g3)
    c: InternalAlignment(g5,g3)
    c: Block(g3)
    c: Coincident(g6,g0)
    c: Coincident(g6,g3)
    c: Horizontal(g6)
FEATURE [Sketcher::SketchObject] Sketch041
  FullyConstrained = true
  sketch-geometry (7):
    g0: LineSegment StartX=0 StartY=0 StartZ=0 EndX=0 EndY=6 EndZ=0
    g1: Circle CenterX=0 CenterY=0 CenterZ=0 NormalX=0 NormalY=0 NormalZ=1 AngleXU=0 Radius=1
    g2: Circle CenterX=8 CenterY=6 CenterZ=0 NormalX=0 NormalY=0 NormalZ=1 AngleXU=0 Radius=1
    g3: BSplineCurve PolesCount=3 KnotsCount=2 Degree=2 IsPeriodic=0
    g4: GeomPoint X=0 Y=0 Z=0
    g5: GeomPoint X=8 Y=6 Z=0
    g6: LineSegment StartX=0 StartY=6 StartZ=0 EndX=8 EndY=6 EndZ=0
  constraints (14):
    c: Coincident(g0,g-1)
    c: Distance(g0) = 6
    c: Vertical(g0)
    c: Coincident(g3,g0)
    c: Weight(g1) = 1
    c: Equal(g1,g2)
    c: InternalAlignment(g1,g3)
    c: InternalAlignment(g2,g3)
    c: InternalAlignment(g4,g3)
    c: InternalAlignment(g5,g3)
    c: Block(g3)
    c: Coincident(g6,g0)
    c: Coincident(g6,g3)
    c: Horizontal(g6)
FEATURE [Sketcher::SketchObject] Sketch042
  FullyConstrained = true
  sketch-geometry (7):
    g0: LineSegment StartX=0 StartY=0 StartZ=0 EndX=0 EndY=6 EndZ=0
    g1: Circle CenterX=0 CenterY=0 CenterZ=0 NormalX=0 NormalY=0 NormalZ=1 AngleXU=0 Radius=1
    g2: Circle CenterX=8 CenterY=6 CenterZ=0 NormalX=0 NormalY=0 NormalZ=1 AngleXU=0 Radius=1
    g3: BSplineCurve PolesCount=3 KnotsCount=2 Degree=2 IsPeriodic=0
    g4: GeomPoint X=0 Y=0 Z=0
    g5: GeomPoint X=8 Y=6 Z=0
    g6: LineSegment StartX=0 StartY=6 StartZ=0 EndX=8 EndY=6 EndZ=0
  constraints (14):
    c: Coincident(g0,g-1)
    c: Distance(g0) = 6
    c: Vertical(g0)
    c: Coincident(g3,g0)
    c: Weight(g1) = 1
    c: Equal(g1,g2)
    c: InternalAlignment(g1,g3)
    c: InternalAlignment(g2,g3)
    c: InternalAlignment(g4,g3)
    c: InternalAlignment(g5,g3)
    c: Block(g3)
    c: Coincident(g6,g0)
    c: Coincident(g6,g3)
    c: Horizontal(g6)
FEATURE [Part::Extrusion] Extrude030  label="caseScrewPillarBracket008"
  Base = -> Sketch039
  Dir = (0,0,1)
  DirMode = 2
  FaceMakerClass = Part::FaceMakerBullseye
  LengthFwd = 2.4
  LengthRev = 0
  Placement = pos=(15.76,29,8.8) rot=(0,1,0;0rad)
  Solid = true
  Symmetric = false
FEATURE [Part::Extrusion] Extrude031  label="caseScrewPillarBracket009"
  Base = -> Sketch040
  Dir = (0,0,1)
  DirMode = 2
  FaceMakerClass = Part::FaceMakerBullseye
  LengthFwd = 2.4
  LengthRev = 0
  Placement = pos=(15.76,29,60.8) rot=(0,0,1;0rad)
  Solid = true
  Symmetric = false
FEATURE [Part::Extrusion] Extrude032  label="caseScrewPillarBracket010"
  Base = -> Sketch041
  Dir = (0,0,1)
  DirMode = 2
  FaceMakerClass = Part::FaceMakerBullseye
  LengthFwd = 2.4
  LengthRev = 0
  Placement = pos=(13.7,29,13.26) rot=(0,-1,0;1.5708rad)
  Solid = true
  Symmetric = false
FEATURE [Part::Extrusion] Extrude033  label="caseScrewPillarBracket011"
  Base = -> Sketch042
  Dir = (0,0,1)
  DirMode = 2
  FaceMakerClass = Part::FaceMakerBullseye
  LengthFwd = 2.4
  LengthRev = 0
  Placement = pos=(11.3,29,58.74) rot=(0,1,0;1.5708rad)
  Solid = true
  Symmetric = false
FEATURE [Sketcher::SketchObject] Sketch043
  FullyConstrained = true
  sketch-geometry (7):
    g0: LineSegment StartX=0 StartY=0 StartZ=0 EndX=0 EndY=6 EndZ=0
    g1: Circle CenterX=0 CenterY=0 CenterZ=0 NormalX=0 NormalY=0 NormalZ=1 AngleXU=0 Radius=1
    g2: Circle CenterX=8 CenterY=6 CenterZ=0 NormalX=0 NormalY=0 NormalZ=1 AngleXU=0 Radius=1
    g3: BSplineCurve PolesCount=3 KnotsCount=2 Degree=2 IsPeriodic=0
    g4: GeomPoint X=0 Y=0 Z=0
    g5: GeomPoint X=8 Y=6 Z=0
    g6: LineSegment StartX=0 StartY=6 StartZ=0 EndX=8 EndY=6 EndZ=0
  constraints (14):
    c: Coincident(g0,g-1)
    c: Distance(g0) = 6
    c: Vertical(g0)
    c: Coincident(g3,g0)
    c: Weight(g1) = 1
    c: Equal(g1,g2)
    c: InternalAlignment(g1,g3)
    c: InternalAlignment(g2,g3)
    c: InternalAlignment(g4,g3)
    c: InternalAlignment(g5,g3)
    c: Block(g3)
    c: Coincident(g6,g0)
    c: Coincident(g6,g3)
    c: Horizontal(g6)
FEATURE [Part::Extrusion] Extrude034  label="caseScrewPillarBracket012"
  Base = -> Sketch043
  Dir = (0,0,1)
  DirMode = 2
  FaceMakerClass = Part::FaceMakerBullseye
  LengthFwd = 2.4
  LengthRev = 0
  Placement = pos=(88.3,29,65.23) rot=(0,1,0;1.5708rad)
  Solid = true
  Symmetric = false
FEATURE [Sketcher::SketchObject] Sketch044
  FullyConstrained = true
  sketch-geometry (7):
    g0: LineSegment StartX=0 StartY=0 StartZ=0 EndX=0 EndY=6 EndZ=0
    g1: Circle CenterX=0 CenterY=0 CenterZ=0 NormalX=0 NormalY=0 NormalZ=1 AngleXU=0 Radius=1
    g2: Circle CenterX=8 CenterY=6 CenterZ=0 NormalX=0 NormalY=0 NormalZ=1 AngleXU=0 Radius=1
    g3: BSplineCurve PolesCount=3 KnotsCount=2 Degree=2 IsPeriodic=0
    g4: GeomPoint X=0 Y=0 Z=0
    g5: GeomPoint X=8 Y=6 Z=0
    g6: LineSegment StartX=0 StartY=6 StartZ=0 EndX=8 EndY=6 EndZ=0
  constraints (14):
    c: Coincident(g0,g-1)
    c: Distance(g0) = 6
    c: Vertical(g0)
    c: Coincident(g3,g0)
    c: Weight(g1) = 1
    c: Equal(g1,g2)
    c: InternalAlignment(g1,g3)
    c: InternalAlignment(g2,g3)
    c: InternalAlignment(g4,g3)
    c: InternalAlignment(g5,g3)
    c: Block(g3)
    c: Coincident(g6,g0)
    c: Coincident(g6,g3)
    c: Horizontal(g6)
FEATURE [Part::Extrusion] Extrude035  label="caseScrewPillarBracket013"
  Base = -> Sketch044
  Dir = (0,0,1)
  DirMode = 2
  FaceMakerClass = Part::FaceMakerBullseye
  LengthFwd = 2.4
  LengthRev = 0
  Placement = pos=(90.7,29,6.77) rot=(0,-1,0;1.5708rad)
  Solid = true
  Symmetric = false
FEATURE [Sketcher::SketchObject] Sketch045
  FullyConstrained = true
  sketch-geometry (7):
    g0: LineSegment StartX=0 StartY=0 StartZ=0 EndX=0 EndY=6 EndZ=0
    g1: Circle CenterX=0 CenterY=0 CenterZ=0 NormalX=0 NormalY=0 NormalZ=1 AngleXU=0 Radius=1
    g2: Circle CenterX=8 CenterY=6 CenterZ=0 NormalX=0 NormalY=0 NormalZ=1 AngleXU=0 Radius=1
    g3: BSplineCurve PolesCount=3 KnotsCount=2 Degree=2 IsPeriodic=0
    g4: GeomPoint X=0 Y=0 Z=0
    g5: GeomPoint X=8 Y=6 Z=0
    g6: LineSegment StartX=0 StartY=6 StartZ=0 EndX=8 EndY=6 EndZ=0
  constraints (14):
    c: Coincident(g0,g-1)
    c: Distance(g0) = 6
    c: Vertical(g0)
    c: Coincident(g3,g0)
    c: Weight(g1) = 1
    c: Equal(g1,g2)
    c: InternalAlignment(g1,g3)
    c: InternalAlignment(g2,g3)
    c: InternalAlignment(g4,g3)
    c: InternalAlignment(g5,g3)
    c: Block(g3)
    c: Coincident(g6,g0)
    c: Coincident(g6,g3)
    c: Horizontal(g6)
FEATURE [Sketcher::SketchObject] Sketch046
  FullyConstrained = true
  sketch-geometry (7):
    g0: LineSegment StartX=0 StartY=0 StartZ=0 EndX=0 EndY=6 EndZ=0
    g1: Circle CenterX=0 CenterY=0 CenterZ=0 NormalX=0 NormalY=0 NormalZ=1 AngleXU=0 Radius=1
    g2: Circle CenterX=8 CenterY=6 CenterZ=0 NormalX=0 NormalY=0 NormalZ=1 AngleXU=0 Radius=1
    g3: BSplineCurve PolesCount=3 KnotsCount=2 Degree=2 IsPeriodic=0
    g4: GeomPoint X=0 Y=0 Z=0
    g5: GeomPoint X=8 Y=6 Z=0
    g6: LineSegment StartX=0 StartY=6 StartZ=0 EndX=8 EndY=6 EndZ=0
  constraints (14):
    c: Coincident(g0,g-1)
    c: Distance(g0) = 6
    c: Vertical(g0)
    c: Coincident(g3,g0)
    c: Weight(g1) = 1
    c: Equal(g1,g2)
    c: InternalAlignment(g1,g3)
    c: InternalAlignment(g2,g3)
    c: InternalAlignment(g4,g3)
    c: InternalAlignment(g5,g3)
    c: Block(g3)
    c: Coincident(g6,g0)
    c: Coincident(g6,g3)
    c: Horizontal(g6)
FEATURE [Part::Extrusion] Extrude036  label="caseScrewPillarBracket014"
  Base = -> Sketch045
  Dir = (0,0,1)
  DirMode = 2
  FaceMakerClass = Part::FaceMakerBullseye
  LengthFwd = 2.4
  LengthRev = 0
  Placement = pos=(110.7,29,6.77) rot=(0,-1,0;1.5708rad)
  Solid = true
  Symmetric = false
FEATURE [Part::Extrusion] Extrude037  label="caseScrewPillarBracket015"
  Base = -> Sketch046
  Dir = (0,0,1)
  DirMode = 2
  FaceMakerClass = Part::FaceMakerBullseye
  LengthFwd = 2.4
  LengthRev = 0
  Placement = pos=(108.3,29,65.23) rot=(0,1,0;1.5708rad)
  Solid = true
  Symmetric = false
FEATURE [Part::Box] Box013  label="frontCaseScrewPillarBracket002"
  AttacherType = Attacher::AttachEngine3D
  Height = 2.4
  Length = 22
  Placement = pos=(87,28,2.3) rot=(0,0,1;0rad)
  Width = 7
FEATURE [Part::Box] Box014  label="frontCaseScrewPillarBracket003"
  AttacherType = Attacher::AttachEngine3D
  Height = 2.4
  Length = 22
  Placement = pos=(87,28,67.3) rot=(0,0,1;0rad)
  Width = 7
FEATURE [Part::Feature] Face087
  shape: bbox 4.8 x 30.2 x 2e-07 mm, 1 faces, 0 solids (baked)
FEATURE [Part::Revolution] Revolve091  label="frontCaseScrewPost004"
  Angle = 360
  Axis = (0,1,0)
  Base = (0,0,0)
  FaceMakerClass = Part::FaceMakerBullseye
  Placement = pos=(89.5,4.5,3.5) rot=(0,0,1;0rad)
  Solid = false
  Source = -> Face087
  Symmetric = false
FEATURE [Part::Feature] Face088
  shape: bbox 4.8 x 30.2 x 2e-07 mm, 1 faces, 0 solids (baked)
FEATURE [Part::Revolution] Revolve092  label="frontCaseScrewPost005"
  Angle = 360
  Axis = (0,1,0)
  Base = (0,0,0)
  FaceMakerClass = Part::FaceMakerBullseye
  Placement = pos=(89.5,4.5,68.5) rot=(0,0,1;0rad)
  Solid = false
  Source = -> Face088
  Symmetric = false
FEATURE [Part::Feature] Face089
  shape: bbox 3.5 x 30.2 x 2e-07 mm, 1 faces, 0 solids (baked)
FEATURE [Part::Revolution] Revolve093  label="backCaseScrewPost002"
  Angle = 360
  Axis = (0,1,0)
  Base = (0,0,0)
  FaceMakerClass = Part::FaceMakerBullseye
  Placement = pos=(12.5,4.5,10) rot=(0,0,1;0rad)
  Solid = false
  Source = -> Face089
  Symmetric = false
FEATURE [Part::Feature] Face090
  shape: bbox 3.5 x 30.2 x 2e-07 mm, 1 faces, 0 solids (baked)
FEATURE [Part::Revolution] Revolve094  label="backCaseScrewPost003"
  Angle = 360
  Axis = (0,1,0)
  Base = (0,0,0)
  FaceMakerClass = Part::FaceMakerBullseye
  Placement = pos=(12.5,4.5,62) rot=(0,0,1;0rad)
  Solid = false
  Source = -> Face090
  Symmetric = false
FEATURE [Part::Box] Box015  label="Cube011"
  AttacherType = Attacher::AttachEngine3D
  Height = 28.8
  Length = 3
  Placement = pos=(107.3,28,21.6) rot=(0,0,1;0rad)
  Width = 7
FEATURE [Part::Box] Box016  label="Cube012"
  AttacherType = Attacher::AttachEngine3D
  Height = 3
  Length = 7.4
  Placement = pos=(107.3,28,18.6) rot=(0,0,1;0rad)
  Width = 7
FEATURE [Part::Box] Box017  label="Cube013"
  AttacherType = Attacher::AttachEngine3D
  Height = 3
  Length = 7.4
  Placement = pos=(107.3,28,50.4) rot=(0,0,1;0rad)
  Width = 7
FEATURE [Part::Cylinder] Cylinder024
  Angle = 360
  AttacherType = Attacher::AttachEngine3D
  Height = 20
  Placement = pos=(0,0,36.15) rot=(0,0,1;0rad)
  Radius = 14.3
FEATURE [Part::Cylinder] Cylinder025
  Angle = 360
  AttacherType = Attacher::AttachEngine3D
  Height = 10
  Placement = pos=(0,0,36.15) rot=(0,0,1;0rad)
  Radius = 4
FEATURE [Part::MultiFuse] Fusion066  label="removeToCreteHoleForPlugHousing009"
  Placement = pos=(70,19,36) rot=(0,1,0;1.5708rad)
  Shapes = -> [Cylinder024,Cylinder025]
FEATURE [Part::MultiFuse] Fusion065  label="plugHousingBracketHolder002"
  Shapes = -> [Box017,Box015,Box016]
FEATURE [Part::Cut] Cut025  label="plugHousingBracketHolder003"
  Base = -> Fusion065
  Placement = pos=(7,0,0) rot=(0,0,1;0rad)
  Tool = -> Fusion066
FEATURE [Sketcher::SketchObject] Sketch047
  FullyConstrained = false
  Placement = pos=(0,0,0) rot=(1,0,0;1.5708rad)
  sketch-geometry (24):
    g0: ArcOfCircle CenterX=-4 CenterY=-10.5 CenterZ=0 NormalX=0 NormalY=0 NormalZ=1 AngleXU=0 Radius=1.5 StartAngle=6e-16 EndAngle=3.14159
    g1: ArcOfCircle CenterX=-34.2 CenterY=-10.5 CenterZ=0 NormalX=0 NormalY=0 NormalZ=1 AngleXU=0 Radius=1.5 StartAngle=0 EndAngle=3.14159
    g2: ArcOfCircle CenterX=-34.2 CenterY=-27.7 CenterZ=0 NormalX=0 NormalY=0 NormalZ=1 AngleXU=0 Radius=1.5 StartAngle=3.14159 EndAngle=6.28319
    g3: ArcOfCircle CenterX=-4 CenterY=-27.7 CenterZ=0 NormalX=0 NormalY=0 NormalZ=1 AngleXU=0 Radius=1.5 StartAngle=3.1416 EndAngle=6.28319
    g4: ArcOfCircle CenterX=-10 CenterY=-4.3 CenterZ=0 NormalX=0 NormalY=0 NormalZ=1 AngleXU=0 Radius=1.5 StartAngle=2e-16 EndAngle=3.14159
    g5: ArcOfCircle CenterX=-16.1 CenterY=-1.8 CenterZ=0 NormalX=0 NormalY=0 NormalZ=1 AngleXU=0 Radius=1.5 StartAngle=5e-16 EndAngle=3.14159
    g6: ArcOfCircle CenterX=-22.1 CenterY=-1.8 CenterZ=0 NormalX=0 NormalY=0 NormalZ=1 AngleXU=0 Radius=1.5 StartAngle=5e-16 EndAngle=3.14159
    g7: ArcOfCircle CenterX=-28.2 CenterY=-4.3 CenterZ=0 NormalX=0 NormalY=0 NormalZ=1 AngleXU=0 Radius=1.5 StartAngle=2e-16 EndAngle=3.14159
    g8: ArcOfCircle CenterX=-10 CenterY=-33.9 CenterZ=0 NormalX=0 NormalY=0 NormalZ=1 AngleXU=0 Radius=1.5 StartAngle=3.14159 EndAngle=6.28319
    g9: ArcOfCircle CenterX=-16.1 CenterY=-36.4 CenterZ=0 NormalX=0 NormalY=0 NormalZ=1 AngleXU=0 Radius=1.5 StartAngle=3.14159 EndAngle=6.28319
    g10: ArcOfCircle CenterX=-22.1 CenterY=-36.4 CenterZ=0 NormalX=0 NormalY=0 NormalZ=1 AngleXU=0 Radius=1.5 StartAngle=3.14159 EndAngle=6.28319
    g11: ArcOfCircle CenterX=-28.2 CenterY=-33.9 CenterZ=0 NormalX=0 NormalY=0 NormalZ=1 AngleXU=0 Radius=1.5 StartAngle=3.14159 EndAngle=6.28319
    g12: LineSegment StartX=-35.7 StartY=-10.5 StartZ=0 EndX=-35.7 EndY=-27.7 EndZ=0
    g13: LineSegment StartX=-32.7 StartY=-10.5 StartZ=0 EndX=-32.7 EndY=-27.7 EndZ=0
    g14: LineSegment StartX=-29.7 StartY=-33.9 StartZ=0 EndX=-29.7 EndY=-4.3 EndZ=0
    g15: LineSegment StartX=-26.7 StartY=-33.9 StartZ=0 EndX=-26.7 EndY=-4.3 EndZ=0
    g16: LineSegment StartX=-2.5 StartY=-10.5 StartZ=0 EndX=-2.5 EndY=-27.7 EndZ=0
    g17: LineSegment StartX=-8.5 StartY=-4.3 StartZ=0 EndX=-8.5 EndY=-33.9 EndZ=0
    g18: LineSegment StartX=-5.5 StartY=-10.5 StartZ=0 EndX=-5.5 EndY=-27.7 EndZ=0
    g19: LineSegment StartX=-11.5 StartY=-4.3 StartZ=0 EndX=-11.5 EndY=-33.9 EndZ=0
    g20: LineSegment StartX=-14.6 StartY=-1.8 StartZ=0 EndX=-14.6 EndY=-36.4 EndZ=0
    g21: LineSegment StartX=-17.6 StartY=-1.8 StartZ=0 EndX=-17.6 EndY=-36.4 EndZ=0
    g22: LineSegment StartX=-20.6 StartY=-36.4 StartZ=0 EndX=-20.6 EndY=-1.8 EndZ=0
    g23: LineSegment StartX=-23.6 StartY=-1.8 StartZ=0 EndX=-23.6 EndY=-36.4 EndZ=0
  constraints (48):
    c: Block(g0)
    c: Block(g1)
    c: Block(g2)
    c: Block(g3)
    c: Block(g4)
    c: Block(g5)
    c: Block(g6)
    c: Block(g7)
    c: Block(g8)
    c: Block(g9)
    c: Block(g10)
    c: Block(g11)
    c: Coincident(g12,g1)
    c: Coincident(g12,g2)
    c: Vertical(g12)
    c: Coincident(g13,g1)
    c: Coincident(g13,g2)
    c: Vertical(g13)
    c: Coincident(g14,g11)
    c: Coincident(g14,g7)
    c: Vertical(g14)
    c: Coincident(g15,g11)
    c: Coincident(g15,g7)
    c: Vertical(g15)
    c: Coincident(g16,g0)
    c: Coincident(g16,g3)
    c: Vertical(g16)
    c: Coincident(g17,g4)
    c: Coincident(g17,g8)
    c: Vertical(g17)
    c: Coincident(g18,g0)
    c: Coincident(g18,g3)
    c: Vertical(g18)
    c: Coincident(g19,g4)
    c: Coincident(g19,g8)
    c: Vertical(g19)
    c: Coincident(g20,g5)
    c: Coincident(g20,g9)
    c: Vertical(g20)
    c: Coincident(g21,g5)
    c: Coincident(g21,g9)
    c: Vertical(g21)
    c: Coincident(g22,g10)
    c: Coincident(g22,g6)
    c: Vertical(g22)
    c: Coincident(g23,g6)
    c: Coincident(g23,g10)
    c: Vertical(g23)
FEATURE [Part::Extrusion] Extrude038  label="removeToCreateFanGrillHoles001"
  Base = -> Sketch047
  Dir = (0,-1,6e-16)
  DirMode = 2
  FaceMakerClass = Part::FaceMakerBullseye
  LengthFwd = 10
  LengthRev = 0
  Placement = pos=(65.4,44,54.82) rot=(0,0,1;0rad)
  Solid = true
  Symmetric = false
FEATURE [Part::Feature] Wire004
  shape: bbox 11 x 5.2 x 2e-07 mm, 0 faces, 0 solids (baked)
FEATURE [Part::Revolution] Revolve095
  Angle = 360
  Axis = (0,1,0)
  Base = (0,0,0)
  FaceMakerClass = Part::FaceMakerBullseye
  Placement = pos=(30.3,38,19.7) rot=(0,0,1;0rad)
  Solid = true
  Source = -> Wire004
  Symmetric = false
FEATURE [Part::Feature] Wire005
  shape: bbox 11 x 5.2 x 2e-07 mm, 0 faces, 0 solids (baked)
FEATURE [Part::Revolution] Revolve096
  Angle = 360
  Axis = (0,1,0)
  Base = (0,0,0)
  FaceMakerClass = Part::FaceMakerBullseye
  Placement = pos=(30.3,38,51.7) rot=(0,0,1;0rad)
  Solid = true
  Source = -> Wire005
  Symmetric = false
FEATURE [Part::Feature] Wire006
  shape: bbox 11 x 5.2 x 2e-07 mm, 0 faces, 0 solids (baked)
FEATURE [Part::Revolution] Revolve097
  Angle = 360
  Axis = (0,1,0)
  Base = (0,0,0)
  FaceMakerClass = Part::FaceMakerBullseye
  Placement = pos=(62.3,38,51.7) rot=(0,0,1;0rad)
  Solid = true
  Source = -> Wire006
  Symmetric = false
FEATURE [Part::Feature] Wire007
  shape: bbox 11 x 5.2 x 2e-07 mm, 0 faces, 0 solids (baked)
FEATURE [Part::Revolution] Revolve098
  Angle = 360
  Axis = (0,1,0)
  Base = (0,0,0)
  FaceMakerClass = Part::FaceMakerBullseye
  Placement = pos=(62.3,38,19.7) rot=(0,0,1;0rad)
  Solid = true
  Source = -> Wire007
  Symmetric = false
FEATURE [Part::MultiFuse] Fusion067  label="fanScrewHousing002"
  Shapes = -> [Revolve098,Revolve097,Revolve096,Revolve095]
FEATURE [Part::Feature] Face091 .. Face094  x4 (patterned run collapsed; names and placements below)
  shape: bbox 3.5 x 17.8 x 2e-07 mm, 1 faces, 0 solids (baked)
FEATURE [Part::Revolution] Revolve099  label="removeToCreateScrewAndThreadedInsertHole026"
  Angle = 360
  Axis = (0,1,0)
  Base = (0,0,0)
  FaceMakerClass = Part::FaceMakerBullseye
  Placement = pos=(62.3,30.3,19.7) rot=(0,0,1;0rad)
  Solid = false
  Source = -> Face091
  Symmetric = false
FEATURE [Part::Revolution] Revolve100  label="removeToCreateScrewAndThreadedInsertHole027"
  Angle = 360
  Axis = (0,1,0)
  Base = (0,0,0)
  FaceMakerClass = Part::FaceMakerBullseye
  Placement = pos=(62.3,30.3,51.7) rot=(0,0,1;0rad)
  Solid = false
  Source = -> Face092
  Symmetric = false
FEATURE [Part::Revolution] Revolve101  label="removeToCreateScrewAndThreadedInsertHole028"
  Angle = 360
  Axis = (0,1,0)
  Base = (0,0,0)
  FaceMakerClass = Part::FaceMakerBullseye
  Placement = pos=(30.3,30.3,19.7) rot=(0,0,1;0rad)
  Solid = false
  Source = -> Face093
  Symmetric = false
FEATURE [Part::Revolution] Revolve102  label="removeToCreateScrewAndThreadedInsertHole029"
  Angle = 360
  Axis = (0,1,0)
  Base = (0,0,0)
  FaceMakerClass = Part::FaceMakerBullseye
  Placement = pos=(30.3,30.3,51.7) rot=(0,0,1;0rad)
  Solid = false
  Source = -> Face094
  Symmetric = false
FEATURE [Part::MultiFuse] Fusion068  label="createThreadedInsertHolesForFan002"
  Shapes = -> [Revolve099,Revolve100,Revolve101,Revolve102]
FEATURE [Part::Cut] Cut026  label="fanScrewHousing003"
  Base = -> Fusion067
  Tool = -> Fusion068
FEATURE [Sketcher::SketchObject] Sketch048
  FullyConstrained = false
  Placement = pos=(0,0,0) rot=(1,0,0;1.5708rad)
  sketch-geometry (24):
    g0: ArcOfCircle CenterX=-4 CenterY=-10.5 CenterZ=0 NormalX=0 NormalY=0 NormalZ=1 AngleXU=0 Radius=1.5 StartAngle=6e-16 EndAngle=3.14159
    g1: ArcOfCircle CenterX=-34.2 CenterY=-10.5 CenterZ=0 NormalX=0 NormalY=0 NormalZ=1 AngleXU=0 Radius=1.5 StartAngle=0 EndAngle=3.14159
    g2: ArcOfCircle CenterX=-34.2 CenterY=-27.7 CenterZ=0 NormalX=0 NormalY=0 NormalZ=1 AngleXU=0 Radius=1.5 StartAngle=3.14159 EndAngle=6.28319
    g3: ArcOfCircle CenterX=-4 CenterY=-27.7 CenterZ=0 NormalX=0 NormalY=0 NormalZ=1 AngleXU=0 Radius=1.5 StartAngle=3.1416 EndAngle=6.28319
    g4: ArcOfCircle CenterX=-10 CenterY=-4.3 CenterZ=0 NormalX=0 NormalY=0 NormalZ=1 AngleXU=0 Radius=1.5 StartAngle=2e-16 EndAngle=3.14159
    g5: ArcOfCircle CenterX=-16.1 CenterY=-1.8 CenterZ=0 NormalX=0 NormalY=0 NormalZ=1 AngleXU=0 Radius=1.5 StartAngle=5e-16 EndAngle=3.14159
    g6: ArcOfCircle CenterX=-22.1 CenterY=-1.8 CenterZ=0 NormalX=0 NormalY=0 NormalZ=1 AngleXU=0 Radius=1.5 StartAngle=5e-16 EndAngle=3.14159
    g7: ArcOfCircle CenterX=-28.2 CenterY=-4.3 CenterZ=0 NormalX=0 NormalY=0 NormalZ=1 AngleXU=0 Radius=1.5 StartAngle=2e-16 EndAngle=3.14159
    g8: ArcOfCircle CenterX=-10 CenterY=-33.9 CenterZ=0 NormalX=0 NormalY=0 NormalZ=1 AngleXU=0 Radius=1.5 StartAngle=3.14159 EndAngle=6.28319
    g9: ArcOfCircle CenterX=-16.1 CenterY=-36.4 CenterZ=0 NormalX=0 NormalY=0 NormalZ=1 AngleXU=0 Radius=1.5 StartAngle=3.14159 EndAngle=6.28319
    g10: ArcOfCircle CenterX=-22.1 CenterY=-36.4 CenterZ=0 NormalX=0 NormalY=0 NormalZ=1 AngleXU=0 Radius=1.5 StartAngle=3.14159 EndAngle=6.28319
    g11: ArcOfCircle CenterX=-28.2 CenterY=-33.9 CenterZ=0 NormalX=0 NormalY=0 NormalZ=1 AngleXU=0 Radius=1.5 StartAngle=3.14159 EndAngle=6.28319
    g12: LineSegment StartX=-35.7 StartY=-10.5 StartZ=0 EndX=-35.7 EndY=-27.7 EndZ=0
    g13: LineSegment StartX=-32.7 StartY=-10.5 StartZ=0 EndX=-32.7 EndY=-27.7 EndZ=0
    g14: LineSegment StartX=-29.7 StartY=-33.9 StartZ=0 EndX=-29.7 EndY=-4.3 EndZ=0
    g15: LineSegment StartX=-26.7 StartY=-33.9 StartZ=0 EndX=-26.7 EndY=-4.3 EndZ=0
    g16: LineSegment StartX=-2.5 StartY=-10.5 StartZ=0 EndX=-2.5 EndY=-27.7 EndZ=0
    g17: LineSegment StartX=-8.5 StartY=-4.3 StartZ=0 EndX=-8.5 EndY=-33.9 EndZ=0
    g18: LineSegment StartX=-5.5 StartY=-10.5 StartZ=0 EndX=-5.5 EndY=-27.7 EndZ=0
    g19: LineSegment StartX=-11.5 StartY=-4.3 StartZ=0 EndX=-11.5 EndY=-33.9 EndZ=0
    g20: LineSegment StartX=-14.6 StartY=-1.8 StartZ=0 EndX=-14.6 EndY=-36.4 EndZ=0
    g21: LineSegment StartX=-17.6 StartY=-1.8 StartZ=0 EndX=-17.6 EndY=-36.4 EndZ=0
    g22: LineSegment StartX=-20.6 StartY=-36.4 StartZ=0 EndX=-20.6 EndY=-1.8 EndZ=0
    g23: LineSegment StartX=-23.6 StartY=-1.8 StartZ=0 EndX=-23.6 EndY=-36.4 EndZ=0
  constraints (48):
    c: Block(g0)
    c: Block(g1)
    c: Block(g2)
    c: Block(g3)
    c: Block(g4)
    c: Block(g5)
    c: Block(g6)
    c: Block(g7)
    c: Block(g8)
    c: Block(g9)
    c: Block(g10)
    c: Block(g11)
    c: Coincident(g12,g1)
    c: Coincident(g12,g2)
    c: Vertical(g12)
    c: Coincident(g13,g1)
    c: Coincident(g13,g2)
    c: Vertical(g13)
    c: Coincident(g14,g11)
    c: Coincident(g14,g7)
    c: Vertical(g14)
    c: Coincident(g15,g11)
    c: Coincident(g15,g7)
    c: Vertical(g15)
    c: Coincident(g16,g0)
    c: Coincident(g16,g3)
    c: Vertical(g16)
    c: Coincident(g17,g4)
    c: Coincident(g17,g8)
    c: Vertical(g17)
    c: Coincident(g18,g0)
    c: Coincident(g18,g3)
    c: Vertical(g18)
    c: Coincident(g19,g4)
    c: Coincident(g19,g8)
    c: Vertical(g19)
    c: Coincident(g20,g5)
    c: Coincident(g20,g9)
    c: Vertical(g20)
    c: Coincident(g21,g5)
    c: Coincident(g21,g9)
    c: Vertical(g21)
    c: Coincident(g22,g10)
    c: Coincident(g22,g6)
    c: Vertical(g22)
    c: Coincident(g23,g6)
    c: Coincident(g23,g10)
    c: Vertical(g23)
FEATURE [Part::Extrusion] Extrude039  label="removeToCreateFanGrillHoles002"
  Base = -> Sketch048
  Dir = (0,-1,6e-16)
  DirMode = 2
  FaceMakerClass = Part::FaceMakerBullseye
  LengthFwd = 10
  LengthRev = 0
  Placement = pos=(65.4,44,54.82) rot=(0,0,1;0rad)
  Solid = true
  Symmetric = false
FEATURE [Part::Cut] Cut027  label="fanScrewHousing004"
  Base = -> Cut026
  Tool = -> Extrude038
FEATURE [Part::Cut] Cut028  label="top014"
  Base = -> Fillet026
  Tool = -> Extrude039
FEATURE [Part::Feature] Face095 .. Face098  x4 (patterned run collapsed; names and placements below)
  shape: bbox 3.5 x 17.8 x 2e-07 mm, 1 faces, 0 solids (baked)
FEATURE [Part::Revolution] Revolve103  label="removeToCreateScrewAndThreadedInsertHole030"
  Angle = 360
  Axis = (0,1,0)
  Base = (0,0,0)
  FaceMakerClass = Part::FaceMakerBullseye
  Placement = pos=(62.3,30.3,19.7) rot=(0,0,1;0rad)
  Solid = false
  Source = -> Face095
  Symmetric = false
FEATURE [Part::Revolution] Revolve104  label="removeToCreateScrewAndThreadedInsertHole031"
  Angle = 360
  Axis = (0,1,0)
  Base = (0,0,0)
  FaceMakerClass = Part::FaceMakerBullseye
  Placement = pos=(62.3,30.3,51.7) rot=(0,0,1;0rad)
  Solid = false
  Source = -> Face096
  Symmetric = false
FEATURE [Part::Revolution] Revolve105  label="removeToCreateScrewAndThreadedInsertHole032"
  Angle = 360
  Axis = (0,1,0)
  Base = (0,0,0)
  FaceMakerClass = Part::FaceMakerBullseye
  Placement = pos=(30.3,30.3,19.7) rot=(0,0,1;0rad)
  Solid = false
  Source = -> Face097
  Symmetric = false
FEATURE [Part::Revolution] Revolve106  label="removeToCreateScrewAndThreadedInsertHole033"
  Angle = 360
  Axis = (0,1,0)
  Base = (0,0,0)
  FaceMakerClass = Part::FaceMakerBullseye
  Placement = pos=(30.3,30.3,51.7) rot=(0,0,1;0rad)
  Solid = false
  Source = -> Face098
  Symmetric = false
FEATURE [Part::MultiFuse] Fusion069  label="createThreadedInsertHolesForFan003"
  Shapes = -> [Revolve103,Revolve104,Revolve105,Revolve106]
FEATURE [Part::Cut] Cut029  label="top015"
  Base = -> Cut028
  Tool = -> Fusion054
FEATURE [Part::Cut] Cut030  label="fanScrewHousing005"
  Base = -> Cut027
  Tool = -> Fusion069
